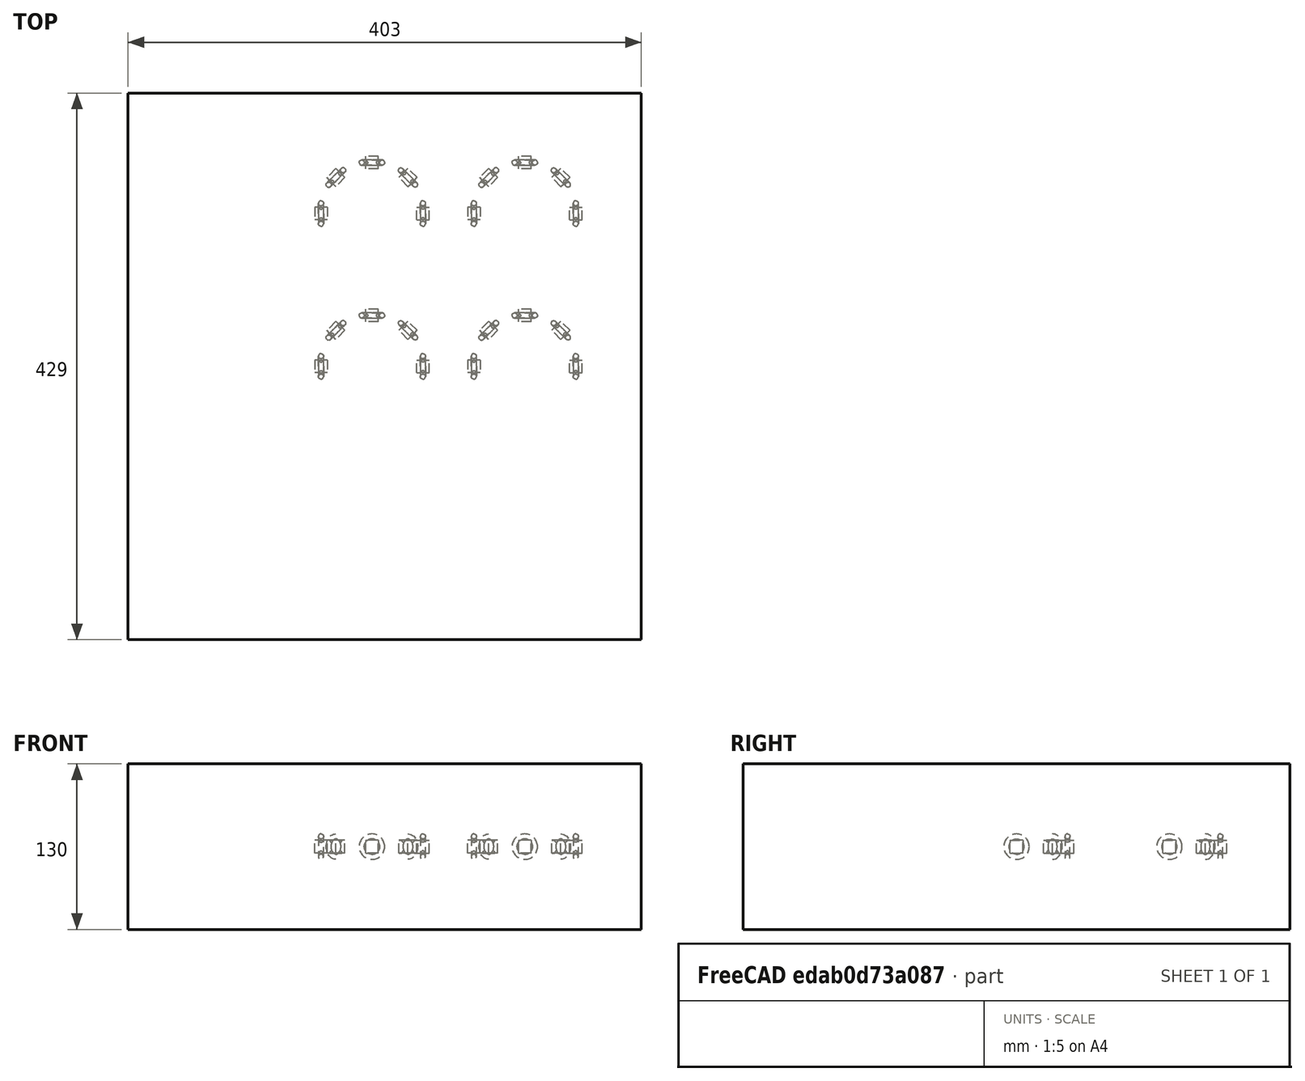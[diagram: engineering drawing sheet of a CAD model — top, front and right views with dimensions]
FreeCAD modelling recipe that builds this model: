
FCSTD DOCUMENT  (FreeCAD 1.0R39109 (Git))
Label: array-of-array-of-solid-offcenter
License: All rights reserved
objects: App::DocumentObjectGroupPython×1251, Part::FeaturePython×5, App::Part×2, Part::MultiFuse×1
note: 5 computed .brp shape members not serialized (recipe doc carries the construction recipe); baked Part::Feature solids carry a one-line shape summary decoded from their .brp

FEATURE [App::DocumentObjectGroupPython] HALFPI  # scripted group (container) (typed FeaturePython)
  name = HALFPI
  value = pi/2.
FEATURE [App::DocumentObjectGroupPython] PI  # scripted group (container) (typed FeaturePython)
  name = PI
  value = 1.*pi
FEATURE [App::DocumentObjectGroupPython] TWOPI  # scripted group (container) (typed FeaturePython)
  name = TWOPI
  value = 2.*pi
FEATURE [App::DocumentObjectGroupPython] Constants  # scripted group (container) (typed FeaturePython)
  Group = -> [HALFPI,PI,TWOPI]
FEATURE [App::DocumentObjectGroupPython] Variables  # scripted group (container) (typed FeaturePython)
FEATURE [App::DocumentObjectGroupPython] Quantities  # scripted group (container) (typed FeaturePython)
FEATURE [App::DocumentObjectGroupPython] Isotopes  # scripted group (container) (typed FeaturePython)
FEATURE [App::DocumentObjectGroupPython] Elements  # scripted group (container) (typed FeaturePython)
FEATURE [App::DocumentObjectGroupPython] Matrix  # scripted group (container) (typed FeaturePython)
FEATURE [App::DocumentObjectGroupPython] Surfaces  # scripted group (container) (typed FeaturePython)
FEATURE [App::DocumentObjectGroupPython] Opticals  # scripted group (container) (typed FeaturePython)
  Group = -> [Matrix,Surfaces]
FEATURE [App::DocumentObjectGroupPython] G4Isotopes  # scripted group (container) (typed FeaturePython)
FEATURE [App::DocumentObjectGroupPython] H_element  # scripted group (container) (typed FeaturePython)
  Z = 1
  atom_value = 1.008
  formula = H
  name = H_element
FEATURE [App::DocumentObjectGroupPython] He_element  # scripted group (container) (typed FeaturePython)
  Z = 2
  atom_value = 4.0026
  formula = He
  name = He_element
FEATURE [App::DocumentObjectGroupPython] Li_element  # scripted group (container) (typed FeaturePython)
  Z = 3
  atom_value = 6.94
  formula = Li
  name = Li_element
FEATURE [App::DocumentObjectGroupPython] Be_element  # scripted group (container) (typed FeaturePython)
  Z = 4
  atom_value = 9.01218
  formula = Be
  name = Be_element
FEATURE [App::DocumentObjectGroupPython] B_element  # scripted group (container) (typed FeaturePython)
  Z = 5
  atom_value = 10.81
  formula = B
  name = B_element
FEATURE [App::DocumentObjectGroupPython] C_element  # scripted group (container) (typed FeaturePython)
  Z = 6
  atom_value = 12.011
  formula = C
  name = C_element
FEATURE [App::DocumentObjectGroupPython] N_element  # scripted group (container) (typed FeaturePython)
  Z = 7
  atom_value = 14.007
  formula = N
  name = N_element
FEATURE [App::DocumentObjectGroupPython] O_element  # scripted group (container) (typed FeaturePython)
  Z = 8
  atom_value = 15.999
  formula = O
  name = O_element
FEATURE [App::DocumentObjectGroupPython] F_element  # scripted group (container) (typed FeaturePython)
  Z = 9
  atom_value = 18.9984
  formula = F
  name = F_element
FEATURE [App::DocumentObjectGroupPython] Ne_element  # scripted group (container) (typed FeaturePython)
  Z = 10
  atom_value = 20.1797
  formula = Ne
  name = Ne_element
FEATURE [App::DocumentObjectGroupPython] Na_element  # scripted group (container) (typed FeaturePython)
  Z = 11
  atom_value = 22.9898
  formula = Na
  name = Na_element
FEATURE [App::DocumentObjectGroupPython] Mg_element  # scripted group (container) (typed FeaturePython)
  Z = 12
  atom_value = 24.305
  formula = Mg
  name = Mg_element
FEATURE [App::DocumentObjectGroupPython] Al_element  # scripted group (container) (typed FeaturePython)
  Z = 13
  atom_value = 26.9815
  formula = Al
  name = Al_element
FEATURE [App::DocumentObjectGroupPython] Si_element  # scripted group (container) (typed FeaturePython)
  Z = 14
  atom_value = 28.085
  formula = Si
  name = Si_element
FEATURE [App::DocumentObjectGroupPython] P_element  # scripted group (container) (typed FeaturePython)
  Z = 15
  atom_value = 30.9738
  formula = P
  name = P_element
FEATURE [App::DocumentObjectGroupPython] S_element  # scripted group (container) (typed FeaturePython)
  Z = 16
  atom_value = 32.06
  formula = S
  name = S_element
FEATURE [App::DocumentObjectGroupPython] Cl_element  # scripted group (container) (typed FeaturePython)
  Z = 17
  atom_value = 35.45
  formula = Cl
  name = Cl_element
FEATURE [App::DocumentObjectGroupPython] Ar_element  # scripted group (container) (typed FeaturePython)
  Z = 18
  atom_value = 39.95
  formula = Ar
  name = Ar_element
FEATURE [App::DocumentObjectGroupPython] K_element  # scripted group (container) (typed FeaturePython)
  Z = 19
  atom_value = 39.0983
  formula = K
  name = K_element
FEATURE [App::DocumentObjectGroupPython] Ca_element  # scripted group (container) (typed FeaturePython)
  Z = 20
  atom_value = 40.078
  formula = Ca
  name = Ca_element
FEATURE [App::DocumentObjectGroupPython] Sc_element  # scripted group (container) (typed FeaturePython)
  Z = 21
  atom_value = 44.9559
  formula = Sc
  name = Sc_element
FEATURE [App::DocumentObjectGroupPython] Ti_element  # scripted group (container) (typed FeaturePython)
  Z = 22
  atom_value = 47.867
  formula = Ti
  name = Ti_element
FEATURE [App::DocumentObjectGroupPython] V_element  # scripted group (container) (typed FeaturePython)
  Z = 23
  atom_value = 50.9415
  formula = V
  name = V_element
FEATURE [App::DocumentObjectGroupPython] Cr_element  # scripted group (container) (typed FeaturePython)
  Z = 24
  atom_value = 51.9961
  formula = Cr
  name = Cr_element
FEATURE [App::DocumentObjectGroupPython] Mn_element  # scripted group (container) (typed FeaturePython)
  Z = 25
  atom_value = 54.938
  formula = Mn
  name = Mn_element
FEATURE [App::DocumentObjectGroupPython] Fe_element  # scripted group (container) (typed FeaturePython)
  Z = 26
  atom_value = 55.845
  formula = Fe
  name = Fe_element
FEATURE [App::DocumentObjectGroupPython] Co_element  # scripted group (container) (typed FeaturePython)
  Z = 27
  atom_value = 58.9332
  formula = Co
  name = Co_element
FEATURE [App::DocumentObjectGroupPython] Ni_element  # scripted group (container) (typed FeaturePython)
  Z = 28
  atom_value = 58.6934
  formula = Ni
  name = Ni_element
FEATURE [App::DocumentObjectGroupPython] Cu_element  # scripted group (container) (typed FeaturePython)
  Z = 29
  atom_value = 63.546
  formula = Cu
  name = Cu_element
FEATURE [App::DocumentObjectGroupPython] Zn_element  # scripted group (container) (typed FeaturePython)
  Z = 30
  atom_value = 65.38
  formula = Zn
  name = Zn_element
FEATURE [App::DocumentObjectGroupPython] Ga_element  # scripted group (container) (typed FeaturePython)
  Z = 31
  atom_value = 69.723
  formula = Ga
  name = Ga_element
FEATURE [App::DocumentObjectGroupPython] Ge_element  # scripted group (container) (typed FeaturePython)
  Z = 32
  atom_value = 72.63
  formula = Ge
  name = Ge_element
FEATURE [App::DocumentObjectGroupPython] As_element  # scripted group (container) (typed FeaturePython)
  Z = 33
  atom_value = 74.9216
  formula = As
  name = As_element
FEATURE [App::DocumentObjectGroupPython] Se_element  # scripted group (container) (typed FeaturePython)
  Z = 34
  atom_value = 78.971
  formula = Se
  name = Se_element
FEATURE [App::DocumentObjectGroupPython] Br_element  # scripted group (container) (typed FeaturePython)
  Z = 35
  atom_value = 79.904
  formula = Br
  name = Br_element
FEATURE [App::DocumentObjectGroupPython] Kr_element  # scripted group (container) (typed FeaturePython)
  Z = 36
  atom_value = 83.798
  formula = Kr
  name = Kr_element
FEATURE [App::DocumentObjectGroupPython] Rb_element  # scripted group (container) (typed FeaturePython)
  Z = 37
  atom_value = 85.4678
  formula = Rb
  name = Rb_element
FEATURE [App::DocumentObjectGroupPython] Sr_element  # scripted group (container) (typed FeaturePython)
  Z = 38
  atom_value = 87.62
  formula = Sr
  name = Sr_element
FEATURE [App::DocumentObjectGroupPython] Y_element  # scripted group (container) (typed FeaturePython)
  Z = 39
  atom_value = 88.9058
  formula = Y
  name = Y_element
FEATURE [App::DocumentObjectGroupPython] Zr_element  # scripted group (container) (typed FeaturePython)
  Z = 40
  atom_value = 91.224
  formula = Zr
  name = Zr_element
FEATURE [App::DocumentObjectGroupPython] Nb_element  # scripted group (container) (typed FeaturePython)
  Z = 41
  atom_value = 92.9064
  formula = Nb
  name = Nb_element
FEATURE [App::DocumentObjectGroupPython] Mo_element  # scripted group (container) (typed FeaturePython)
  Z = 42
  atom_value = 95.95
  formula = Mo
  name = Mo_element
FEATURE [App::DocumentObjectGroupPython] Tc_element  # scripted group (container) (typed FeaturePython)
  Z = 43
  atom_value = 97
  formula = Tc
  name = Tc_element
FEATURE [App::DocumentObjectGroupPython] Ru_element  # scripted group (container) (typed FeaturePython)
  Z = 44
  atom_value = 101.07
  formula = Ru
  name = Ru_element
FEATURE [App::DocumentObjectGroupPython] Rh_element  # scripted group (container) (typed FeaturePython)
  Z = 45
  atom_value = 102.905
  formula = Rh
  name = Rh_element
FEATURE [App::DocumentObjectGroupPython] Pd_element  # scripted group (container) (typed FeaturePython)
  Z = 46
  atom_value = 106.42
  formula = Pd
  name = Pd_element
FEATURE [App::DocumentObjectGroupPython] Ag_element  # scripted group (container) (typed FeaturePython)
  Z = 47
  atom_value = 107.868
  formula = Ag
  name = Ag_element
FEATURE [App::DocumentObjectGroupPython] Cd_element  # scripted group (container) (typed FeaturePython)
  Z = 48
  atom_value = 112.414
  formula = Cd
  name = Cd_element
FEATURE [App::DocumentObjectGroupPython] In_element  # scripted group (container) (typed FeaturePython)
  Z = 49
  atom_value = 114.818
  formula = In
  name = In_element
FEATURE [App::DocumentObjectGroupPython] Sn_element  # scripted group (container) (typed FeaturePython)
  Z = 50
  atom_value = 118.71
  formula = Sn
  name = Sn_element
FEATURE [App::DocumentObjectGroupPython] Sb_element  # scripted group (container) (typed FeaturePython)
  Z = 51
  atom_value = 121.76
  formula = Sb
  name = Sb_element
FEATURE [App::DocumentObjectGroupPython] Te_element  # scripted group (container) (typed FeaturePython)
  Z = 52
  atom_value = 127.6
  formula = Te
  name = Te_element
FEATURE [App::DocumentObjectGroupPython] I_element  # scripted group (container) (typed FeaturePython)
  Z = 53
  atom_value = 126.904
  formula = I
  name = I_element
FEATURE [App::DocumentObjectGroupPython] Xe_element  # scripted group (container) (typed FeaturePython)
  Z = 54
  atom_value = 131.293
  formula = Xe
  name = Xe_element
FEATURE [App::DocumentObjectGroupPython] Cs_element  # scripted group (container) (typed FeaturePython)
  Z = 55
  atom_value = 132.905
  formula = Cs
  name = Cs_element
FEATURE [App::DocumentObjectGroupPython] Ba_element  # scripted group (container) (typed FeaturePython)
  Z = 56
  atom_value = 137.327
  formula = Ba
  name = Ba_element
FEATURE [App::DocumentObjectGroupPython] La_element  # scripted group (container) (typed FeaturePython)
  Z = 57
  atom_value = 138.905
  formula = La
  name = La_element
FEATURE [App::DocumentObjectGroupPython] Ce_element  # scripted group (container) (typed FeaturePython)
  Z = 58
  atom_value = 140.116
  formula = Ce
  name = Ce_element
FEATURE [App::DocumentObjectGroupPython] Pr_element  # scripted group (container) (typed FeaturePython)
  Z = 59
  atom_value = 140.908
  formula = Pr
  name = Pr_element
FEATURE [App::DocumentObjectGroupPython] Nd_element  # scripted group (container) (typed FeaturePython)
  Z = 60
  atom_value = 144.242
  formula = Nd
  name = Nd_element
FEATURE [App::DocumentObjectGroupPython] Pm_element  # scripted group (container) (typed FeaturePython)
  Z = 61
  atom_value = 145
  formula = Pm
  name = Pm_element
FEATURE [App::DocumentObjectGroupPython] Sm_element  # scripted group (container) (typed FeaturePython)
  Z = 62
  atom_value = 150.36
  formula = Sm
  name = Sm_element
FEATURE [App::DocumentObjectGroupPython] Eu_element  # scripted group (container) (typed FeaturePython)
  Z = 63
  atom_value = 151.964
  formula = Eu
  name = Eu_element
FEATURE [App::DocumentObjectGroupPython] Gd_element  # scripted group (container) (typed FeaturePython)
  Z = 64
  atom_value = 157.25
  formula = Gd
  name = Gd_element
FEATURE [App::DocumentObjectGroupPython] Tb_element  # scripted group (container) (typed FeaturePython)
  Z = 65
  atom_value = 158.925
  formula = Tb
  name = Tb_element
FEATURE [App::DocumentObjectGroupPython] Dy_element  # scripted group (container) (typed FeaturePython)
  Z = 66
  atom_value = 162.5
  formula = Dy
  name = Dy_element
FEATURE [App::DocumentObjectGroupPython] Ho_element  # scripted group (container) (typed FeaturePython)
  Z = 67
  atom_value = 164.93
  formula = Ho
  name = Ho_element
FEATURE [App::DocumentObjectGroupPython] Er_element  # scripted group (container) (typed FeaturePython)
  Z = 68
  atom_value = 167.259
  formula = Er
  name = Er_element
FEATURE [App::DocumentObjectGroupPython] Tm_element  # scripted group (container) (typed FeaturePython)
  Z = 69
  atom_value = 168.934
  formula = Tm
  name = Tm_element
FEATURE [App::DocumentObjectGroupPython] Yb_element  # scripted group (container) (typed FeaturePython)
  Z = 70
  atom_value = 173.045
  formula = Yb
  name = Yb_element
FEATURE [App::DocumentObjectGroupPython] Lu_element  # scripted group (container) (typed FeaturePython)
  Z = 71
  atom_value = 174.967
  formula = Lu
  name = Lu_element
FEATURE [App::DocumentObjectGroupPython] Hf_element  # scripted group (container) (typed FeaturePython)
  Z = 72
  atom_value = 178.49
  formula = Hf
  name = Hf_element
FEATURE [App::DocumentObjectGroupPython] Ta_element  # scripted group (container) (typed FeaturePython)
  Z = 73
  atom_value = 180.948
  formula = Ta
  name = Ta_element
FEATURE [App::DocumentObjectGroupPython] W_element  # scripted group (container) (typed FeaturePython)
  Z = 74
  atom_value = 183.84
  formula = W
  name = W_element
FEATURE [App::DocumentObjectGroupPython] Re_element  # scripted group (container) (typed FeaturePython)
  Z = 75
  atom_value = 186.207
  formula = Re
  name = Re_element
FEATURE [App::DocumentObjectGroupPython] Os_element  # scripted group (container) (typed FeaturePython)
  Z = 76
  atom_value = 190.23
  formula = Os
  name = Os_element
FEATURE [App::DocumentObjectGroupPython] Ir_element  # scripted group (container) (typed FeaturePython)
  Z = 77
  atom_value = 192.217
  formula = Ir
  name = Ir_element
FEATURE [App::DocumentObjectGroupPython] Pt_element  # scripted group (container) (typed FeaturePython)
  Z = 78
  atom_value = 195.084
  formula = Pt
  name = Pt_element
FEATURE [App::DocumentObjectGroupPython] Au_element  # scripted group (container) (typed FeaturePython)
  Z = 79
  atom_value = 196.967
  formula = Au
  name = Au_element
FEATURE [App::DocumentObjectGroupPython] Hg_element  # scripted group (container) (typed FeaturePython)
  Z = 80
  atom_value = 200.592
  formula = Hg
  name = Hg_element
FEATURE [App::DocumentObjectGroupPython] Tl_element  # scripted group (container) (typed FeaturePython)
  Z = 81
  atom_value = 204.38
  formula = Tl
  name = Tl_element
FEATURE [App::DocumentObjectGroupPython] Pb_element  # scripted group (container) (typed FeaturePython)
  Z = 82
  atom_value = 207.2
  formula = Pb
  name = Pb_element
FEATURE [App::DocumentObjectGroupPython] Bi_element  # scripted group (container) (typed FeaturePython)
  Z = 83
  atom_value = 208.98
  formula = Bi
  name = Bi_element
FEATURE [App::DocumentObjectGroupPython] Po_element  # scripted group (container) (typed FeaturePython)
  Z = 84
  atom_value = 209
  formula = Po
  name = Po_element
FEATURE [App::DocumentObjectGroupPython] At_element  # scripted group (container) (typed FeaturePython)
  Z = 85
  atom_value = 210
  formula = At
  name = At_element
FEATURE [App::DocumentObjectGroupPython] Rn_element  # scripted group (container) (typed FeaturePython)
  Z = 86
  atom_value = 222
  formula = Rn
  name = Rn_element
FEATURE [App::DocumentObjectGroupPython] Fr_element  # scripted group (container) (typed FeaturePython)
  Z = 87
  atom_value = 223
  formula = Fr
  name = Fr_element
FEATURE [App::DocumentObjectGroupPython] Ra_element  # scripted group (container) (typed FeaturePython)
  Z = 88
  atom_value = 226
  formula = Ra
  name = Ra_element
FEATURE [App::DocumentObjectGroupPython] Ac_element  # scripted group (container) (typed FeaturePython)
  Z = 89
  atom_value = 227
  formula = Ac
  name = Ac_element
FEATURE [App::DocumentObjectGroupPython] Th_element  # scripted group (container) (typed FeaturePython)
  Z = 90
  atom_value = 232.038
  formula = Th
  name = Th_element
FEATURE [App::DocumentObjectGroupPython] Pa_element  # scripted group (container) (typed FeaturePython)
  Z = 91
  atom_value = 231.036
  formula = Pa
  name = Pa_element
FEATURE [App::DocumentObjectGroupPython] U_element  # scripted group (container) (typed FeaturePython)
  Z = 92
  atom_value = 238.029
  formula = U
  name = U_element
FEATURE [App::DocumentObjectGroupPython] Np_element  # scripted group (container) (typed FeaturePython)
  Z = 93
  atom_value = 237
  formula = Np
  name = Np_element
FEATURE [App::DocumentObjectGroupPython] Pu_element  # scripted group (container) (typed FeaturePython)
  Z = 94
  atom_value = 244
  formula = Pu
  name = Pu_element
FEATURE [App::DocumentObjectGroupPython] Am_element  # scripted group (container) (typed FeaturePython)
  Z = 95
  atom_value = 243
  formula = Am
  name = Am_element
FEATURE [App::DocumentObjectGroupPython] Cm_element  # scripted group (container) (typed FeaturePython)
  Z = 96
  atom_value = 247
  formula = Cm
  name = Cm_element
FEATURE [App::DocumentObjectGroupPython] Bk_element  # scripted group (container) (typed FeaturePython)
  Z = 97
  atom_value = 247
  formula = Bk
  name = Bk_element
FEATURE [App::DocumentObjectGroupPython] Cf_element  # scripted group (container) (typed FeaturePython)
  Z = 98
  atom_value = 251
  formula = Cf
  name = Cf_element
FEATURE [App::DocumentObjectGroupPython] G4Elements  # scripted group (container) (typed FeaturePython)
  Group = -> [H_element,He_element,Li_element,Be_element,B_element,C_element,N_element,O_element,F_element,Ne_element,Na_element,Mg_element,Al_element,Si_element,P_element,S_element,Cl_element,Ar_element,K_element,Ca_element,Sc_element,Ti_element,V_element,Cr_element,Mn_element,Fe_element,Co_element,Ni_element,Cu_element,Zn_element,Ga_element,Ge_element,As_element,Se_element,Br_element,Kr_element,Rb_element,+61 more]
FEATURE [App::DocumentObjectGroupPython] H_element001  label="H_element : 0.101"  # scripted group (container) (typed FeaturePython)
  n = 0.101327
FEATURE [App::DocumentObjectGroupPython] C_element001  label="C_element : 0.775"  # scripted group (container) (typed FeaturePython)
  n = 0.7755
FEATURE [App::DocumentObjectGroupPython] N_element001  label="N_element : 0.035"  # scripted group (container) (typed FeaturePython)
  n = 0.035057
FEATURE [App::DocumentObjectGroupPython] O_element001  label="O_element : 0.052"  # scripted group (container) (typed FeaturePython)
  n = 0.0523159
FEATURE [App::DocumentObjectGroupPython] F_element001  label="F_element : 0.017"  # scripted group (container) (typed FeaturePython)
  n = 0.017422
FEATURE [App::DocumentObjectGroupPython] Ca_element001  label="Ca_element : 0.018"  # scripted group (container) (typed FeaturePython)
  n = 0.018378
FEATURE [App::DocumentObjectGroupPython] G4_A_150_TISSUE  label="G4_A-150_TISSUE"  # scripted group (container) (typed FeaturePython)
  Dunit = g/cm3
  Dvalue = 1.127
  Group = -> [H_element001,C_element001,N_element001,O_element001,F_element001,Ca_element001]
  conduct = 2
  density = 1
  expand = 3
  formula = G4_A-150_TISSUE
  name = G4_A-150_TISSUE
  specific = 4
FEATURE [App::DocumentObjectGroupPython] C_element002  label="C_element : 3"  # scripted group (container) (typed FeaturePython)
  n = 3
  ref = C_element
FEATURE [App::DocumentObjectGroupPython] H_element002  label="H_element : 6"  # scripted group (container) (typed FeaturePython)
  n = 6
  ref = H_element
FEATURE [App::DocumentObjectGroupPython] O_element002  label="O_element : 1"  # scripted group (container) (typed FeaturePython)
  n = 1
  ref = O_element
FEATURE [App::DocumentObjectGroupPython] G4_ACETONE  # scripted group (container) (typed FeaturePython)
  Dunit = g/cm3
  Dvalue = 0.7899
  Group = -> [C_element002,H_element002,O_element002]
  conduct = 2
  density = 1
  expand = 3
  formula = G4_ACETONE
  name = G4_ACETONE
  specific = 4
FEATURE [App::DocumentObjectGroupPython] C_element003  label="C_element : 2"  # scripted group (container) (typed FeaturePython)
  n = 2
  ref = C_element
FEATURE [App::DocumentObjectGroupPython] H_element003  label="H_element : 2"  # scripted group (container) (typed FeaturePython)
  n = 2
  ref = H_element
FEATURE [App::DocumentObjectGroupPython] G4_ACETYLENE  # scripted group (container) (typed FeaturePython)
  Dunit = g/cm3
  Dvalue = 0.0010967
  Group = -> [C_element003,H_element003]
  conduct = 2
  density = 1
  expand = 3
  formula = G4_ACETYLENE
  name = G4_ACETYLENE
  specific = 4
FEATURE [App::DocumentObjectGroupPython] C_element004  label="C_element : 5"  # scripted group (container) (typed FeaturePython)
  n = 5
  ref = C_element
FEATURE [App::DocumentObjectGroupPython] H_element004  label="H_element : 5"  # scripted group (container) (typed FeaturePython)
  n = 5
  ref = H_element
FEATURE [App::DocumentObjectGroupPython] N_element002  label="N_element : 5"  # scripted group (container) (typed FeaturePython)
  n = 5
  ref = N_element
FEATURE [App::DocumentObjectGroupPython] G4_ADENINE  # scripted group (container) (typed FeaturePython)
  Dunit = g/cm3
  Dvalue = 1.6
  Group = -> [C_element004,H_element004,N_element002]
  conduct = 2
  density = 1
  expand = 3
  formula = G4_ADENINE
  name = G4_ADENINE
  specific = 4
FEATURE [App::DocumentObjectGroupPython] H_element005  label="H_element : 0.114"  # scripted group (container) (typed FeaturePython)
  n = 0.114
FEATURE [App::DocumentObjectGroupPython] C_element005  label="C_element : 0.598"  # scripted group (container) (typed FeaturePython)
  n = 0.598
FEATURE [App::DocumentObjectGroupPython] N_element003  label="N_element : 0.007"  # scripted group (container) (typed FeaturePython)
  n = 0.007
FEATURE [App::DocumentObjectGroupPython] O_element003  label="O_element : 0.278"  # scripted group (container) (typed FeaturePython)
  n = 0.278
FEATURE [App::DocumentObjectGroupPython] Na_element001  label="Na_element : 0.001"  # scripted group (container) (typed FeaturePython)
  n = 0.001
FEATURE [App::DocumentObjectGroupPython] S_element001  label="S_element : 0.001"  # scripted group (container) (typed FeaturePython)
  n = 0.001
FEATURE [App::DocumentObjectGroupPython] Cl_element001  label="Cl_element : 0.001"  # scripted group (container) (typed FeaturePython)
  n = 0.001
FEATURE [App::DocumentObjectGroupPython] G4_ADIPOSE_TISSUE_ICRP  # scripted group (container) (typed FeaturePython)
  Dunit = g/cm3
  Dvalue = 0.95
  Group = -> [H_element005,C_element005,N_element003,O_element003,Na_element001,S_element001,Cl_element001]
  conduct = 2
  density = 1
  expand = 3
  formula = G4_ADIPOSE_TISSUE_ICRP
  name = G4_ADIPOSE_TISSUE_ICRP
  specific = 4
FEATURE [App::DocumentObjectGroupPython] C_element006  label="C_element : 0.000"  # scripted group (container) (typed FeaturePython)
  n = 0.000124
FEATURE [App::DocumentObjectGroupPython] N_element004  label="N_element : 0.755"  # scripted group (container) (typed FeaturePython)
  n = 0.755268
FEATURE [App::DocumentObjectGroupPython] O_element004  label="O_element : 0.232"  # scripted group (container) (typed FeaturePython)
  n = 0.231781
FEATURE [App::DocumentObjectGroupPython] Ar_element001  label="Ar_element : 0.013"  # scripted group (container) (typed FeaturePython)
  n = 0.012827
FEATURE [App::DocumentObjectGroupPython] G4_AIR  # scripted group (container) (typed FeaturePython)
  Dunit = g/cm3
  Dvalue = 0.00120479
  Group = -> [C_element006,N_element004,O_element004,Ar_element001]
  conduct = 2
  density = 1
  expand = 3
  formula = G4_AIR
  name = G4_AIR
  specific = 4
FEATURE [App::DocumentObjectGroupPython] C_element007  label="C_element : 006"  # scripted group (container) (typed FeaturePython)
  n = 3
  ref = C_element
FEATURE [App::DocumentObjectGroupPython] H_element006  label="H_element : 7"  # scripted group (container) (typed FeaturePython)
  n = 7
  ref = H_element
FEATURE [App::DocumentObjectGroupPython] N_element005  label="N_element : 1"  # scripted group (container) (typed FeaturePython)
  n = 1
  ref = N_element
FEATURE [App::DocumentObjectGroupPython] O_element005  label="O_element : 2"  # scripted group (container) (typed FeaturePython)
  n = 2
  ref = O_element
FEATURE [App::DocumentObjectGroupPython] G4_ALANINE  # scripted group (container) (typed FeaturePython)
  Dunit = g/cm3
  Dvalue = 1.42
  Group = -> [C_element007,H_element006,N_element005,O_element005]
  conduct = 2
  density = 1
  expand = 3
  formula = G4_ALANINE
  name = G4_ALANINE
  specific = 4
FEATURE [App::DocumentObjectGroupPython] Al_element001  label="Al_element : 2"  # scripted group (container) (typed FeaturePython)
  n = 2
  ref = Al_element
FEATURE [App::DocumentObjectGroupPython] O_element006  label="O_element : 3"  # scripted group (container) (typed FeaturePython)
  n = 3
  ref = O_element
FEATURE [App::DocumentObjectGroupPython] G4_ALUMINUM_OXIDE  # scripted group (container) (typed FeaturePython)
  Dunit = g/cm3
  Dvalue = 3.97
  Group = -> [Al_element001,O_element006]
  conduct = 2
  density = 1
  expand = 3
  formula = G4_ALUMINUM_OXIDE
  name = G4_ALUMINUM_OXIDE
  specific = 4
FEATURE [App::DocumentObjectGroupPython] H_element007  label="H_element : 0.106"  # scripted group (container) (typed FeaturePython)
  n = 0.10593
FEATURE [App::DocumentObjectGroupPython] C_element008  label="C_element : 0.789"  # scripted group (container) (typed FeaturePython)
  n = 0.788974
FEATURE [App::DocumentObjectGroupPython] O_element007  label="O_element : 0.105"  # scripted group (container) (typed FeaturePython)
  n = 0.105096
FEATURE [App::DocumentObjectGroupPython] G4_AMBER  # scripted group (container) (typed FeaturePython)
  Dunit = g/cm3
  Dvalue = 1.1
  Group = -> [H_element007,C_element008,O_element007]
  conduct = 2
  density = 1
  expand = 3
  formula = G4_AMBER
  name = G4_AMBER
  specific = 4
FEATURE [App::DocumentObjectGroupPython] N_element006  label="N_element : 006"  # scripted group (container) (typed FeaturePython)
  n = 1
  ref = N_element
FEATURE [App::DocumentObjectGroupPython] H_element008  label="H_element : 3"  # scripted group (container) (typed FeaturePython)
  n = 3
  ref = H_element
FEATURE [App::DocumentObjectGroupPython] G4_AMMONIA  # scripted group (container) (typed FeaturePython)
  Dunit = g/cm3
  Dvalue = 0.000826019
  Group = -> [N_element006,H_element008]
  conduct = 2
  density = 1
  expand = 3
  formula = G4_AMMONIA
  name = G4_AMMONIA
  specific = 4
FEATURE [App::DocumentObjectGroupPython] C_element009  label="C_element : 6"  # scripted group (container) (typed FeaturePython)
  n = 6
  ref = C_element
FEATURE [App::DocumentObjectGroupPython] H_element009  label="H_element : 008"  # scripted group (container) (typed FeaturePython)
  n = 7
  ref = H_element
FEATURE [App::DocumentObjectGroupPython] N_element007  label="N_element : 007"  # scripted group (container) (typed FeaturePython)
  n = 1
  ref = N_element
FEATURE [App::DocumentObjectGroupPython] G4_ANILINE  # scripted group (container) (typed FeaturePython)
  Dunit = g/cm3
  Dvalue = 1.0235
  Group = -> [C_element009,H_element009,N_element007]
  conduct = 2
  density = 1
  expand = 3
  formula = G4_ANILINE
  name = G4_ANILINE
  specific = 4
FEATURE [App::DocumentObjectGroupPython] C_element010  label="C_element : 14"  # scripted group (container) (typed FeaturePython)
  n = 14
  ref = C_element
FEATURE [App::DocumentObjectGroupPython] H_element010  label="H_element : 10"  # scripted group (container) (typed FeaturePython)
  n = 10
  ref = H_element
FEATURE [App::DocumentObjectGroupPython] G4_ANTHRACENE  # scripted group (container) (typed FeaturePython)
  Dunit = g/cm3
  Dvalue = 1.283
  Group = -> [C_element010,H_element010]
  conduct = 2
  density = 1
  expand = 3
  formula = G4_ANTHRACENE
  name = G4_ANTHRACENE
  specific = 4
FEATURE [App::DocumentObjectGroupPython] H_element011  label="H_element : 0.065"  # scripted group (container) (typed FeaturePython)
  n = 0.0654709
FEATURE [App::DocumentObjectGroupPython] C_element011  label="C_element : 0.537"  # scripted group (container) (typed FeaturePython)
  n = 0.536944
FEATURE [App::DocumentObjectGroupPython] N_element008  label="N_element : 0.021"  # scripted group (container) (typed FeaturePython)
  n = 0.0215
FEATURE [App::DocumentObjectGroupPython] O_element008  label="O_element : 0.032"  # scripted group (container) (typed FeaturePython)
  n = 0.032085
FEATURE [App::DocumentObjectGroupPython] F_element002  label="F_element : 0.167"  # scripted group (container) (typed FeaturePython)
  n = 0.167411
FEATURE [App::DocumentObjectGroupPython] Ca_element002  label="Ca_element : 0.177"  # scripted group (container) (typed FeaturePython)
  n = 0.176589
FEATURE [App::DocumentObjectGroupPython] G4_B_100_BONE  label="G4_B-100_BONE"  # scripted group (container) (typed FeaturePython)
  Dunit = g/cm3
  Dvalue = 1.45
  Group = -> [H_element011,C_element011,N_element008,O_element008,F_element002,Ca_element002]
  conduct = 2
  density = 1
  expand = 3
  formula = G4_B-100_BONE
  name = G4_B-100_BONE
  specific = 4
FEATURE [App::DocumentObjectGroupPython] H_element012  label="H_element : 0.057"  # scripted group (container) (typed FeaturePython)
  n = 0.057441
FEATURE [App::DocumentObjectGroupPython] C_element012  label="C_element : 0.790"  # scripted group (container) (typed FeaturePython)
  n = 0.774591
FEATURE [App::DocumentObjectGroupPython] O_element009  label="O_element : 0.168"  # scripted group (container) (typed FeaturePython)
  n = 0.167968
FEATURE [App::DocumentObjectGroupPython] G4_BAKELITE  # scripted group (container) (typed FeaturePython)
  Dunit = g/cm3
  Dvalue = 1.25
  Group = -> [H_element012,C_element012,O_element009]
  conduct = 2
  density = 1
  expand = 3
  formula = G4_BAKELITE
  name = G4_BAKELITE
  specific = 4
FEATURE [App::DocumentObjectGroupPython] Ba_element001  label="Ba_element : 1"  # scripted group (container) (typed FeaturePython)
  n = 1
  ref = Ba_element
FEATURE [App::DocumentObjectGroupPython] F_element003  label="F_element : 2"  # scripted group (container) (typed FeaturePython)
  n = 2
  ref = F_element
FEATURE [App::DocumentObjectGroupPython] G4_BARIUM_FLUORIDE  # scripted group (container) (typed FeaturePython)
  Dunit = g/cm3
  Dvalue = 4.89
  Group = -> [Ba_element001,F_element003]
  conduct = 2
  density = 1
  expand = 3
  formula = G4_BARIUM_FLUORIDE
  name = G4_BARIUM_FLUORIDE
  specific = 4
FEATURE [App::DocumentObjectGroupPython] Ba_element002  label="Ba_element : 002"  # scripted group (container) (typed FeaturePython)
  n = 1
  ref = Ba_element
FEATURE [App::DocumentObjectGroupPython] S_element002  label="S_element : 1"  # scripted group (container) (typed FeaturePython)
  n = 1
  ref = S_element
FEATURE [App::DocumentObjectGroupPython] O_element010  label="O_element : 4"  # scripted group (container) (typed FeaturePython)
  n = 4
  ref = O_element
FEATURE [App::DocumentObjectGroupPython] G4_BARIUM_SULFATE  # scripted group (container) (typed FeaturePython)
  Dunit = g/cm3
  Dvalue = 4.5
  Group = -> [Ba_element002,S_element002,O_element010]
  conduct = 2
  density = 1
  expand = 3
  formula = G4_BARIUM_SULFATE
  name = G4_BARIUM_SULFATE
  specific = 4
FEATURE [App::DocumentObjectGroupPython] C_element013  label="C_element : 007"  # scripted group (container) (typed FeaturePython)
  n = 6
  ref = C_element
FEATURE [App::DocumentObjectGroupPython] H_element013  label="H_element : 009"  # scripted group (container) (typed FeaturePython)
  n = 6
  ref = H_element
FEATURE [App::DocumentObjectGroupPython] G4_BENZENE  # scripted group (container) (typed FeaturePython)
  Dunit = g/cm3
  Dvalue = 0.87865
  Group = -> [C_element013,H_element013]
  conduct = 2
  density = 1
  expand = 3
  formula = G4_BENZENE
  name = G4_BENZENE
  specific = 4
FEATURE [App::DocumentObjectGroupPython] Be_element001  label="Be_element : 1"  # scripted group (container) (typed FeaturePython)
  n = 1
  ref = Be_element
FEATURE [App::DocumentObjectGroupPython] O_element011  label="O_element : 005"  # scripted group (container) (typed FeaturePython)
  n = 1
  ref = O_element
FEATURE [App::DocumentObjectGroupPython] G4_BERYLLIUM_OXIDE  # scripted group (container) (typed FeaturePython)
  Dunit = g/cm3
  Dvalue = 3.01
  Group = -> [Be_element001,O_element011]
  conduct = 2
  density = 1
  expand = 3
  formula = G4_BERYLLIUM_OXIDE
  name = G4_BERYLLIUM_OXIDE
  specific = 4
FEATURE [App::DocumentObjectGroupPython] Bi_element001  label="Bi_element : 4"  # scripted group (container) (typed FeaturePython)
  n = 4
  ref = Bi_element
FEATURE [App::DocumentObjectGroupPython] Ge_element001  label="Ge_element : 3"  # scripted group (container) (typed FeaturePython)
  n = 3
  ref = Ge_element
FEATURE [App::DocumentObjectGroupPython] O_element012  label="O_element : 12"  # scripted group (container) (typed FeaturePython)
  n = 12
  ref = O_element
FEATURE [App::DocumentObjectGroupPython] G4_BGO  # scripted group (container) (typed FeaturePython)
  Dunit = g/cm3
  Dvalue = 7.13
  Group = -> [Bi_element001,Ge_element001,O_element012]
  conduct = 2
  density = 1
  expand = 3
  formula = G4_BGO
  name = G4_BGO
  specific = 4
FEATURE [App::DocumentObjectGroupPython] H_element014  label="H_element : 0.102"  # scripted group (container) (typed FeaturePython)
  n = 0.102
FEATURE [App::DocumentObjectGroupPython] C_element014  label="C_element : 0.110"  # scripted group (container) (typed FeaturePython)
  n = 0.11
FEATURE [App::DocumentObjectGroupPython] N_element009  label="N_element : 0.033"  # scripted group (container) (typed FeaturePython)
  n = 0.033
FEATURE [App::DocumentObjectGroupPython] O_element013  label="O_element : 0.745"  # scripted group (container) (typed FeaturePython)
  n = 0.745
FEATURE [App::DocumentObjectGroupPython] Na_element002  label="Na_element : 0.002"  # scripted group (container) (typed FeaturePython)
  n = 0.001
FEATURE [App::DocumentObjectGroupPython] P_element001  label="P_element : 0.001"  # scripted group (container) (typed FeaturePython)
  n = 0.001
FEATURE [App::DocumentObjectGroupPython] S_element003  label="S_element : 0.002"  # scripted group (container) (typed FeaturePython)
  n = 0.002
FEATURE [App::DocumentObjectGroupPython] Cl_element002  label="Cl_element : 0.003"  # scripted group (container) (typed FeaturePython)
  n = 0.003
FEATURE [App::DocumentObjectGroupPython] K_element001  label="K_element : 0.002"  # scripted group (container) (typed FeaturePython)
  n = 0.002
FEATURE [App::DocumentObjectGroupPython] Fe_element001  label="Fe_element : 0.001"  # scripted group (container) (typed FeaturePython)
  n = 0.001
FEATURE [App::DocumentObjectGroupPython] G4_BLOOD_ICRP  # scripted group (container) (typed FeaturePython)
  Dunit = g/cm3
  Dvalue = 1.06
  Group = -> [H_element014,C_element014,N_element009,O_element013,Na_element002,P_element001,S_element003,Cl_element002,K_element001,Fe_element001]
  conduct = 2
  density = 1
  expand = 3
  formula = G4_BLOOD_ICRP
  name = G4_BLOOD_ICRP
  specific = 4
FEATURE [App::DocumentObjectGroupPython] H_element015  label="H_element : 0.064"  # scripted group (container) (typed FeaturePython)
  n = 0.064
FEATURE [App::DocumentObjectGroupPython] C_element015  label="C_element : 0.278"  # scripted group (container) (typed FeaturePython)
  n = 0.278
FEATURE [App::DocumentObjectGroupPython] N_element010  label="N_element : 0.027"  # scripted group (container) (typed FeaturePython)
  n = 0.027
FEATURE [App::DocumentObjectGroupPython] O_element014  label="O_element : 0.410"  # scripted group (container) (typed FeaturePython)
  n = 0.41
FEATURE [App::DocumentObjectGroupPython] Mg_element001  label="Mg_element : 0.002"  # scripted group (container) (typed FeaturePython)
  n = 0.002
FEATURE [App::DocumentObjectGroupPython] P_element002  label="P_element : 0.070"  # scripted group (container) (typed FeaturePython)
  n = 0.07
FEATURE [App::DocumentObjectGroupPython] S_element004  label="S_element : 0.003"  # scripted group (container) (typed FeaturePython)
  n = 0.002
FEATURE [App::DocumentObjectGroupPython] Ca_element003  label="Ca_element : 0.147"  # scripted group (container) (typed FeaturePython)
  n = 0.147
FEATURE [App::DocumentObjectGroupPython] G4_BONE_COMPACT_ICRU  # scripted group (container) (typed FeaturePython)
  Dunit = g/cm3
  Dvalue = 1.85
  Group = -> [H_element015,C_element015,N_element010,O_element014,Mg_element001,P_element002,S_element004,Ca_element003]
  conduct = 2
  density = 1
  expand = 3
  formula = G4_BONE_COMPACT_ICRU
  name = G4_BONE_COMPACT_ICRU
  specific = 4
FEATURE [App::DocumentObjectGroupPython] H_element016  label="H_element : 0.034"  # scripted group (container) (typed FeaturePython)
  n = 0.034
FEATURE [App::DocumentObjectGroupPython] C_element016  label="C_element : 0.155"  # scripted group (container) (typed FeaturePython)
  n = 0.155
FEATURE [App::DocumentObjectGroupPython] N_element011  label="N_element : 0.042"  # scripted group (container) (typed FeaturePython)
  n = 0.042
FEATURE [App::DocumentObjectGroupPython] O_element015  label="O_element : 0.435"  # scripted group (container) (typed FeaturePython)
  n = 0.435
FEATURE [App::DocumentObjectGroupPython] Na_element003  label="Na_element : 0.003"  # scripted group (container) (typed FeaturePython)
  n = 0.001
FEATURE [App::DocumentObjectGroupPython] Mg_element002  label="Mg_element : 0.003"  # scripted group (container) (typed FeaturePython)
  n = 0.002
FEATURE [App::DocumentObjectGroupPython] P_element003  label="P_element : 0.103"  # scripted group (container) (typed FeaturePython)
  n = 0.103
FEATURE [App::DocumentObjectGroupPython] S_element005  label="S_element : 0.004"  # scripted group (container) (typed FeaturePython)
  n = 0.003
FEATURE [App::DocumentObjectGroupPython] Ca_element004  label="Ca_element : 0.225"  # scripted group (container) (typed FeaturePython)
  n = 0.225
FEATURE [App::DocumentObjectGroupPython] G4_BONE_CORTICAL_ICRP  # scripted group (container) (typed FeaturePython)
  Dunit = g/cm3
  Dvalue = 1.92
  Group = -> [H_element016,C_element016,N_element011,O_element015,Na_element003,Mg_element002,P_element003,S_element005,Ca_element004]
  conduct = 2
  density = 1
  expand = 3
  formula = G4_BONE_CORTICAL_ICRP
  name = G4_BONE_CORTICAL_ICRP
  specific = 4
FEATURE [App::DocumentObjectGroupPython] B_element001  label="B_element : 4"  # scripted group (container) (typed FeaturePython)
  n = 4
  ref = B_element
FEATURE [App::DocumentObjectGroupPython] C_element017  label="C_element : 1"  # scripted group (container) (typed FeaturePython)
  n = 1
  ref = C_element
FEATURE [App::DocumentObjectGroupPython] G4_BORON_CARBIDE  # scripted group (container) (typed FeaturePython)
  Dunit = g/cm3
  Dvalue = 2.52
  Group = -> [B_element001,C_element017]
  conduct = 2
  density = 1
  expand = 3
  formula = G4_BORON_CARBIDE
  name = G4_BORON_CARBIDE
  specific = 4
FEATURE [App::DocumentObjectGroupPython] B_element002  label="B_element : 2"  # scripted group (container) (typed FeaturePython)
  n = 2
  ref = B_element
FEATURE [App::DocumentObjectGroupPython] O_element016  label="O_element : 006"  # scripted group (container) (typed FeaturePython)
  n = 3
  ref = O_element
FEATURE [App::DocumentObjectGroupPython] G4_BORON_OXIDE  # scripted group (container) (typed FeaturePython)
  Dunit = g/cm3
  Dvalue = 1.812
  Group = -> [B_element002,O_element016]
  conduct = 2
  density = 1
  expand = 3
  formula = G4_BORON_OXIDE
  name = G4_BORON_OXIDE
  specific = 4
FEATURE [App::DocumentObjectGroupPython] H_element017  label="H_element : 0.107"  # scripted group (container) (typed FeaturePython)
  n = 0.107
FEATURE [App::DocumentObjectGroupPython] C_element018  label="C_element : 0.145"  # scripted group (container) (typed FeaturePython)
  n = 0.145
FEATURE [App::DocumentObjectGroupPython] N_element012  label="N_element : 0.022"  # scripted group (container) (typed FeaturePython)
  n = 0.022
FEATURE [App::DocumentObjectGroupPython] O_element017  label="O_element : 0.712"  # scripted group (container) (typed FeaturePython)
  n = 0.712
FEATURE [App::DocumentObjectGroupPython] Na_element004  label="Na_element : 0.004"  # scripted group (container) (typed FeaturePython)
  n = 0.002
FEATURE [App::DocumentObjectGroupPython] P_element004  label="P_element : 0.004"  # scripted group (container) (typed FeaturePython)
  n = 0.004
FEATURE [App::DocumentObjectGroupPython] S_element006  label="S_element : 0.005"  # scripted group (container) (typed FeaturePython)
  n = 0.002
FEATURE [App::DocumentObjectGroupPython] Cl_element003  label="Cl_element : 0.004"  # scripted group (container) (typed FeaturePython)
  n = 0.003
FEATURE [App::DocumentObjectGroupPython] K_element002  label="K_element : 0.003"  # scripted group (container) (typed FeaturePython)
  n = 0.003
FEATURE [App::DocumentObjectGroupPython] G4_BRAIN_ICRP  # scripted group (container) (typed FeaturePython)
  Dunit = g/cm3
  Dvalue = 1.04
  Group = -> [H_element017,C_element018,N_element012,O_element017,Na_element004,P_element004,S_element006,Cl_element003,K_element002]
  conduct = 2
  density = 1
  expand = 3
  formula = G4_BRAIN_ICRP
  name = G4_BRAIN_ICRP
  specific = 4
FEATURE [App::DocumentObjectGroupPython] C_element019  label="C_element : 4"  # scripted group (container) (typed FeaturePython)
  n = 4
  ref = C_element
FEATURE [App::DocumentObjectGroupPython] H_element018  label="H_element : 010"  # scripted group (container) (typed FeaturePython)
  n = 10
  ref = H_element
FEATURE [App::DocumentObjectGroupPython] G4_BUTANE  # scripted group (container) (typed FeaturePython)
  Dunit = g/cm3
  Dvalue = 0.00249343
  Group = -> [C_element019,H_element018]
  conduct = 2
  density = 1
  expand = 3
  formula = G4_BUTANE
  name = G4_BUTANE
  specific = 4
FEATURE [App::DocumentObjectGroupPython] C_element020  label="C_element : 008"  # scripted group (container) (typed FeaturePython)
  n = 4
  ref = C_element
FEATURE [App::DocumentObjectGroupPython] H_element019  label="H_element : 011"  # scripted group (container) (typed FeaturePython)
  n = 10
  ref = H_element
FEATURE [App::DocumentObjectGroupPython] O_element018  label="O_element : 007"  # scripted group (container) (typed FeaturePython)
  n = 1
  ref = O_element
FEATURE [App::DocumentObjectGroupPython] G4_N_BUTYL_ALCOHOL  label="G4_N-BUTYL_ALCOHOL"  # scripted group (container) (typed FeaturePython)
  Dunit = g/cm3
  Dvalue = 0.8098
  Group = -> [C_element020,H_element019,O_element018]
  conduct = 2
  density = 1
  expand = 3
  formula = G4_N-BUTYL_ALCOHOL
  name = G4_N-BUTYL_ALCOHOL
  specific = 4
FEATURE [App::DocumentObjectGroupPython] H_element020  label="H_element : 0.025"  # scripted group (container) (typed FeaturePython)
  n = 0.02468
FEATURE [App::DocumentObjectGroupPython] C_element021  label="C_element : 0.502"  # scripted group (container) (typed FeaturePython)
  n = 0.501611
FEATURE [App::DocumentObjectGroupPython] O_element019  label="O_element : 0.005"  # scripted group (container) (typed FeaturePython)
  n = 0.004527
FEATURE [App::DocumentObjectGroupPython] F_element004  label="F_element : 0.465"  # scripted group (container) (typed FeaturePython)
  n = 0.465209
FEATURE [App::DocumentObjectGroupPython] Si_element001  label="Si_element : 0.004"  # scripted group (container) (typed FeaturePython)
  n = 0.003973
FEATURE [App::DocumentObjectGroupPython] G4_C_552  label="G4_C-552"  # scripted group (container) (typed FeaturePython)
  Dunit = g/cm3
  Dvalue = 1.76
  Group = -> [H_element020,C_element021,O_element019,F_element004,Si_element001]
  conduct = 2
  density = 1
  expand = 3
  formula = G4_C-552
  name = G4_C-552
  specific = 4
FEATURE [App::DocumentObjectGroupPython] Cd_element001  label="Cd_element : 1"  # scripted group (container) (typed FeaturePython)
  n = 1
  ref = Cd_element
FEATURE [App::DocumentObjectGroupPython] Te_element001  label="Te_element : 1"  # scripted group (container) (typed FeaturePython)
  n = 1
  ref = Te_element
FEATURE [App::DocumentObjectGroupPython] G4_CADMIUM_TELLURIDE  # scripted group (container) (typed FeaturePython)
  Dunit = g/cm3
  Dvalue = 6.2
  Group = -> [Cd_element001,Te_element001]
  conduct = 2
  density = 1
  expand = 3
  formula = G4_CADMIUM_TELLURIDE
  name = G4_CADMIUM_TELLURIDE
  specific = 4
FEATURE [App::DocumentObjectGroupPython] Cd_element002  label="Cd_element : 002"  # scripted group (container) (typed FeaturePython)
  n = 1
  ref = Cd_element
FEATURE [App::DocumentObjectGroupPython] W_element001  label="W_element : 1"  # scripted group (container) (typed FeaturePython)
  n = 1
  ref = W_element
FEATURE [App::DocumentObjectGroupPython] O_element020  label="O_element : 008"  # scripted group (container) (typed FeaturePython)
  n = 4
  ref = O_element
FEATURE [App::DocumentObjectGroupPython] G4_CADMIUM_TUNGSTATE  # scripted group (container) (typed FeaturePython)
  Dunit = g/cm3
  Dvalue = 7.9
  Group = -> [Cd_element002,W_element001,O_element020]
  conduct = 2
  density = 1
  expand = 3
  formula = G4_CADMIUM_TUNGSTATE
  name = G4_CADMIUM_TUNGSTATE
  specific = 4
FEATURE [App::DocumentObjectGroupPython] Ca_element005  label="Ca_element : 1"  # scripted group (container) (typed FeaturePython)
  n = 1
  ref = Ca_element
FEATURE [App::DocumentObjectGroupPython] C_element022  label="C_element : 009"  # scripted group (container) (typed FeaturePython)
  n = 1
  ref = C_element
FEATURE [App::DocumentObjectGroupPython] O_element021  label="O_element : 009"  # scripted group (container) (typed FeaturePython)
  n = 3
  ref = O_element
FEATURE [App::DocumentObjectGroupPython] G4_CALCIUM_CARBONATE  # scripted group (container) (typed FeaturePython)
  Dunit = g/cm3
  Dvalue = 2.8
  Group = -> [Ca_element005,C_element022,O_element021]
  conduct = 2
  density = 1
  expand = 3
  formula = G4_CALCIUM_CARBONATE
  name = G4_CALCIUM_CARBONATE
  specific = 4
FEATURE [App::DocumentObjectGroupPython] Ca_element006  label="Ca_element : 002"  # scripted group (container) (typed FeaturePython)
  n = 1
  ref = Ca_element
FEATURE [App::DocumentObjectGroupPython] F_element005  label="F_element : 003"  # scripted group (container) (typed FeaturePython)
  n = 2
  ref = F_element
FEATURE [App::DocumentObjectGroupPython] G4_CALCIUM_FLUORIDE  # scripted group (container) (typed FeaturePython)
  Dunit = g/cm3
  Dvalue = 3.18
  Group = -> [Ca_element006,F_element005]
  conduct = 2
  density = 1
  expand = 3
  formula = G4_CALCIUM_FLUORIDE
  name = G4_CALCIUM_FLUORIDE
  specific = 4
FEATURE [App::DocumentObjectGroupPython] Ca_element007  label="Ca_element : 003"  # scripted group (container) (typed FeaturePython)
  n = 1
  ref = Ca_element
FEATURE [App::DocumentObjectGroupPython] O_element022  label="O_element : 010"  # scripted group (container) (typed FeaturePython)
  n = 1
  ref = O_element
FEATURE [App::DocumentObjectGroupPython] G4_CALCIUM_OXIDE  # scripted group (container) (typed FeaturePython)
  Dunit = g/cm3
  Dvalue = 3.3
  Group = -> [Ca_element007,O_element022]
  conduct = 2
  density = 1
  expand = 3
  formula = G4_CALCIUM_OXIDE
  name = G4_CALCIUM_OXIDE
  specific = 4
FEATURE [App::DocumentObjectGroupPython] Ca_element008  label="Ca_element : 004"  # scripted group (container) (typed FeaturePython)
  n = 1
  ref = Ca_element
FEATURE [App::DocumentObjectGroupPython] S_element007  label="S_element : 002"  # scripted group (container) (typed FeaturePython)
  n = 1
  ref = S_element
FEATURE [App::DocumentObjectGroupPython] O_element023  label="O_element : 011"  # scripted group (container) (typed FeaturePython)
  n = 4
  ref = O_element
FEATURE [App::DocumentObjectGroupPython] G4_CALCIUM_SULFATE  # scripted group (container) (typed FeaturePython)
  Dunit = g/cm3
  Dvalue = 2.96
  Group = -> [Ca_element008,S_element007,O_element023]
  conduct = 2
  density = 1
  expand = 3
  formula = G4_CALCIUM_SULFATE
  name = G4_CALCIUM_SULFATE
  specific = 4
FEATURE [App::DocumentObjectGroupPython] Ca_element009  label="Ca_element : 005"  # scripted group (container) (typed FeaturePython)
  n = 1
  ref = Ca_element
FEATURE [App::DocumentObjectGroupPython] W_element002  label="W_element : 002"  # scripted group (container) (typed FeaturePython)
  n = 1
  ref = W_element
FEATURE [App::DocumentObjectGroupPython] O_element024  label="O_element : 012"  # scripted group (container) (typed FeaturePython)
  n = 4
  ref = O_element
FEATURE [App::DocumentObjectGroupPython] G4_CALCIUM_TUNGSTATE  # scripted group (container) (typed FeaturePython)
  Dunit = g/cm3
  Dvalue = 6.062
  Group = -> [Ca_element009,W_element002,O_element024]
  conduct = 2
  density = 1
  expand = 3
  formula = G4_CALCIUM_TUNGSTATE
  name = G4_CALCIUM_TUNGSTATE
  specific = 4
FEATURE [App::DocumentObjectGroupPython] C_element023  label="C_element : 010"  # scripted group (container) (typed FeaturePython)
  n = 1
  ref = C_element
FEATURE [App::DocumentObjectGroupPython] O_element025  label="O_element : 013"  # scripted group (container) (typed FeaturePython)
  n = 2
  ref = O_element
FEATURE [App::DocumentObjectGroupPython] G4_CARBON_DIOXIDE  # scripted group (container) (typed FeaturePython)
  Dunit = g/cm3
  Dvalue = 0.00184212
  Group = -> [C_element023,O_element025]
  conduct = 2
  density = 1
  expand = 3
  formula = G4_CARBON_DIOXIDE
  name = G4_CARBON_DIOXIDE
  specific = 4
FEATURE [App::DocumentObjectGroupPython] C_element024  label="C_element : 011"  # scripted group (container) (typed FeaturePython)
  n = 1
  ref = C_element
FEATURE [App::DocumentObjectGroupPython] Cl_element004  label="Cl_element : 4"  # scripted group (container) (typed FeaturePython)
  n = 4
  ref = Cl_element
FEATURE [App::DocumentObjectGroupPython] G4_CARBON_TETRACHLORIDE  # scripted group (container) (typed FeaturePython)
  Dunit = g/cm3
  Dvalue = 1.594
  Group = -> [C_element024,Cl_element004]
  conduct = 2
  density = 1
  expand = 3
  formula = G4_CARBON_TETRACHLORIDE
  name = G4_CARBON_TETRACHLORIDE
  specific = 4
FEATURE [App::DocumentObjectGroupPython] C_element025  label="C_element : 012"  # scripted group (container) (typed FeaturePython)
  n = 6
  ref = C_element
FEATURE [App::DocumentObjectGroupPython] H_element021  label="H_element : 012"  # scripted group (container) (typed FeaturePython)
  n = 10
  ref = H_element
FEATURE [App::DocumentObjectGroupPython] O_element026  label="O_element : 5"  # scripted group (container) (typed FeaturePython)
  n = 5
  ref = O_element
FEATURE [App::DocumentObjectGroupPython] G4_CELLULOSE_CELLOPHANE  # scripted group (container) (typed FeaturePython)
  Dunit = g/cm3
  Dvalue = 1.42
  Group = -> [C_element025,H_element021,O_element026]
  conduct = 2
  density = 1
  expand = 3
  formula = G4_CELLULOSE_CELLOPHANE
  name = G4_CELLULOSE_CELLOPHANE
  specific = 4
FEATURE [App::DocumentObjectGroupPython] H_element022  label="H_element : 0.067"  # scripted group (container) (typed FeaturePython)
  n = 0.067125
FEATURE [App::DocumentObjectGroupPython] C_element026  label="C_element : 0.545"  # scripted group (container) (typed FeaturePython)
  n = 0.545403
FEATURE [App::DocumentObjectGroupPython] O_element027  label="O_element : 0.387"  # scripted group (container) (typed FeaturePython)
  n = 0.387472
FEATURE [App::DocumentObjectGroupPython] G4_CELLULOSE_BUTYRATE  # scripted group (container) (typed FeaturePython)
  Dunit = g/cm3
  Dvalue = 1.2
  Group = -> [H_element022,C_element026,O_element027]
  conduct = 2
  density = 1
  expand = 3
  formula = G4_CELLULOSE_BUTYRATE
  name = G4_CELLULOSE_BUTYRATE
  specific = 4
FEATURE [App::DocumentObjectGroupPython] H_element023  label="H_element : 0.029"  # scripted group (container) (typed FeaturePython)
  n = 0.029216
FEATURE [App::DocumentObjectGroupPython] C_element027  label="C_element : 0.271"  # scripted group (container) (typed FeaturePython)
  n = 0.271296
FEATURE [App::DocumentObjectGroupPython] N_element013  label="N_element : 0.121"  # scripted group (container) (typed FeaturePython)
  n = 0.121276
FEATURE [App::DocumentObjectGroupPython] O_element028  label="O_element : 0.578"  # scripted group (container) (typed FeaturePython)
  n = 0.578212
FEATURE [App::DocumentObjectGroupPython] G4_CELLULOSE_NITRATE  # scripted group (container) (typed FeaturePython)
  Dunit = g/cm3
  Dvalue = 1.49
  Group = -> [H_element023,C_element027,N_element013,O_element028]
  conduct = 2
  density = 1
  expand = 3
  formula = G4_CELLULOSE_NITRATE
  name = G4_CELLULOSE_NITRATE
  specific = 4
FEATURE [App::DocumentObjectGroupPython] H_element024  label="H_element : 0.108"  # scripted group (container) (typed FeaturePython)
  n = 0.107596
FEATURE [App::DocumentObjectGroupPython] N_element014  label="N_element : 0.001"  # scripted group (container) (typed FeaturePython)
  n = 0.0008
FEATURE [App::DocumentObjectGroupPython] O_element029  label="O_element : 0.875"  # scripted group (container) (typed FeaturePython)
  n = 0.874976
FEATURE [App::DocumentObjectGroupPython] S_element008  label="S_element : 0.015"  # scripted group (container) (typed FeaturePython)
  n = 0.014627
FEATURE [App::DocumentObjectGroupPython] Ce_element001  label="Ce_element : 0.002"  # scripted group (container) (typed FeaturePython)
  n = 0.002001
FEATURE [App::DocumentObjectGroupPython] G4_CERIC_SULFATE  # scripted group (container) (typed FeaturePython)
  Dunit = g/cm3
  Dvalue = 1.03
  Group = -> [H_element024,N_element014,O_element029,S_element008,Ce_element001]
  conduct = 2
  density = 1
  expand = 3
  formula = G4_CERIC_SULFATE
  name = G4_CERIC_SULFATE
  specific = 4
FEATURE [App::DocumentObjectGroupPython] Cs_element001  label="Cs_element : 1"  # scripted group (container) (typed FeaturePython)
  n = 1
  ref = Cs_element
FEATURE [App::DocumentObjectGroupPython] F_element006  label="F_element : 1"  # scripted group (container) (typed FeaturePython)
  n = 1
  ref = F_element
FEATURE [App::DocumentObjectGroupPython] G4_CESIUM_FLUORIDE  # scripted group (container) (typed FeaturePython)
  Dunit = g/cm3
  Dvalue = 4.115
  Group = -> [Cs_element001,F_element006]
  conduct = 2
  density = 1
  expand = 3
  formula = G4_CESIUM_FLUORIDE
  name = G4_CESIUM_FLUORIDE
  specific = 4
FEATURE [App::DocumentObjectGroupPython] Cs_element002  label="Cs_element : 002"  # scripted group (container) (typed FeaturePython)
  n = 1
  ref = Cs_element
FEATURE [App::DocumentObjectGroupPython] I_element001  label="I_element : 1"  # scripted group (container) (typed FeaturePython)
  n = 1
  ref = I_element
FEATURE [App::DocumentObjectGroupPython] G4_CESIUM_IODIDE  # scripted group (container) (typed FeaturePython)
  Dunit = g/cm3
  Dvalue = 4.51
  Group = -> [Cs_element002,I_element001]
  conduct = 2
  density = 1
  expand = 3
  formula = G4_CESIUM_IODIDE
  name = G4_CESIUM_IODIDE
  specific = 4
FEATURE [App::DocumentObjectGroupPython] C_element028  label="C_element : 013"  # scripted group (container) (typed FeaturePython)
  n = 6
  ref = C_element
FEATURE [App::DocumentObjectGroupPython] H_element025  label="H_element : 013"  # scripted group (container) (typed FeaturePython)
  n = 5
  ref = H_element
FEATURE [App::DocumentObjectGroupPython] Cl_element005  label="Cl_element : 1"  # scripted group (container) (typed FeaturePython)
  n = 1
  ref = Cl_element
FEATURE [App::DocumentObjectGroupPython] G4_CHLOROBENZENE  # scripted group (container) (typed FeaturePython)
  Dunit = g/cm3
  Dvalue = 1.1058
  Group = -> [C_element028,H_element025,Cl_element005]
  conduct = 2
  density = 1
  expand = 3
  formula = G4_CHLOROBENZENE
  name = G4_CHLOROBENZENE
  specific = 4
FEATURE [App::DocumentObjectGroupPython] C_element029  label="C_element : 014"  # scripted group (container) (typed FeaturePython)
  n = 1
  ref = C_element
FEATURE [App::DocumentObjectGroupPython] H_element026  label="H_element : 1"  # scripted group (container) (typed FeaturePython)
  n = 1
  ref = H_element
FEATURE [App::DocumentObjectGroupPython] Cl_element006  label="Cl_element : 3"  # scripted group (container) (typed FeaturePython)
  n = 3
  ref = Cl_element
FEATURE [App::DocumentObjectGroupPython] G4_CHLOROFORM  # scripted group (container) (typed FeaturePython)
  Dunit = g/cm3
  Dvalue = 1.4832
  Group = -> [C_element029,H_element026,Cl_element006]
  conduct = 2
  density = 1
  expand = 3
  formula = G4_CHLOROFORM
  name = G4_CHLOROFORM
  specific = 4
FEATURE [App::DocumentObjectGroupPython] H_element027  label="H_element : 0.010"  # scripted group (container) (typed FeaturePython)
  n = 0.01
FEATURE [App::DocumentObjectGroupPython] C_element030  label="C_element : 0.001"  # scripted group (container) (typed FeaturePython)
  n = 0.001
FEATURE [App::DocumentObjectGroupPython] O_element030  label="O_element : 0.529"  # scripted group (container) (typed FeaturePython)
  n = 0.529107
FEATURE [App::DocumentObjectGroupPython] Na_element005  label="Na_element : 0.016"  # scripted group (container) (typed FeaturePython)
  n = 0.016
FEATURE [App::DocumentObjectGroupPython] Mg_element003  label="Mg_element : 0.004"  # scripted group (container) (typed FeaturePython)
  n = 0.002
FEATURE [App::DocumentObjectGroupPython] Al_element002  label="Al_element : 0.034"  # scripted group (container) (typed FeaturePython)
  n = 0.033872
FEATURE [App::DocumentObjectGroupPython] Si_element002  label="Si_element : 0.337"  # scripted group (container) (typed FeaturePython)
  n = 0.337021
FEATURE [App::DocumentObjectGroupPython] K_element003  label="K_element : 0.013"  # scripted group (container) (typed FeaturePython)
  n = 0.013
FEATURE [App::DocumentObjectGroupPython] Ca_element010  label="Ca_element : 0.044"  # scripted group (container) (typed FeaturePython)
  n = 0.044
FEATURE [App::DocumentObjectGroupPython] Fe_element002  label="Fe_element : 0.014"  # scripted group (container) (typed FeaturePython)
  n = 0.014
FEATURE [App::DocumentObjectGroupPython] G4_CONCRETE  # scripted group (container) (typed FeaturePython)
  Dunit = g/cm3
  Dvalue = 2.3
  Group = -> [H_element027,C_element030,O_element030,Na_element005,Mg_element003,Al_element002,Si_element002,K_element003,Ca_element010,Fe_element002]
  conduct = 2
  density = 1
  expand = 3
  formula = G4_CONCRETE
  name = G4_CONCRETE
  specific = 4
FEATURE [App::DocumentObjectGroupPython] C_element031  label="C_element : 015"  # scripted group (container) (typed FeaturePython)
  n = 6
  ref = C_element
FEATURE [App::DocumentObjectGroupPython] H_element028  label="H_element : 12"  # scripted group (container) (typed FeaturePython)
  n = 12
  ref = H_element
FEATURE [App::DocumentObjectGroupPython] G4_CYCLOHEXANE  # scripted group (container) (typed FeaturePython)
  Dunit = g/cm3
  Dvalue = 0.779
  Group = -> [C_element031,H_element028]
  conduct = 2
  density = 1
  expand = 3
  formula = G4_CYCLOHEXANE
  name = G4_CYCLOHEXANE
  specific = 4
FEATURE [App::DocumentObjectGroupPython] C_element032  label="C_element : 016"  # scripted group (container) (typed FeaturePython)
  n = 6
  ref = C_element
FEATURE [App::DocumentObjectGroupPython] H_element029  label="H_element : 4"  # scripted group (container) (typed FeaturePython)
  n = 4
  ref = H_element
FEATURE [App::DocumentObjectGroupPython] Cl_element007  label="Cl_element : 2"  # scripted group (container) (typed FeaturePython)
  n = 2
  ref = Cl_element
FEATURE [App::DocumentObjectGroupPython] G4_1_2_DICHLOROBENZENE  label="G4_1.2-DICHLOROBENZENE"  # scripted group (container) (typed FeaturePython)
  Dunit = g/cm3
  Dvalue = 1.3048
  Group = -> [C_element032,H_element029,Cl_element007]
  conduct = 2
  density = 1
  expand = 3
  formula = G4_1.2-DICHLOROBENZENE
  name = G4_1.2-DICHLOROBENZENE
  specific = 4
FEATURE [App::DocumentObjectGroupPython] C_element033  label="C_element : 017"  # scripted group (container) (typed FeaturePython)
  n = 4
  ref = C_element
FEATURE [App::DocumentObjectGroupPython] H_element030  label="H_element : 8"  # scripted group (container) (typed FeaturePython)
  n = 8
  ref = H_element
FEATURE [App::DocumentObjectGroupPython] O_element031  label="O_element : 014"  # scripted group (container) (typed FeaturePython)
  n = 1
  ref = O_element
FEATURE [App::DocumentObjectGroupPython] Cl_element008  label="Cl_element : 005"  # scripted group (container) (typed FeaturePython)
  n = 2
  ref = Cl_element
FEATURE [App::DocumentObjectGroupPython] G4_DICHLORODIETHYL_ETHER  # scripted group (container) (typed FeaturePython)
  Dunit = g/cm3
  Dvalue = 1.2199
  Group = -> [C_element033,H_element030,O_element031,Cl_element008]
  conduct = 2
  density = 1
  expand = 3
  formula = G4_DICHLORODIETHYL_ETHER
  name = G4_DICHLORODIETHYL_ETHER
  specific = 4
FEATURE [App::DocumentObjectGroupPython] C_element034  label="C_element : 018"  # scripted group (container) (typed FeaturePython)
  n = 2
  ref = C_element
FEATURE [App::DocumentObjectGroupPython] H_element031  label="H_element : 014"  # scripted group (container) (typed FeaturePython)
  n = 4
  ref = H_element
FEATURE [App::DocumentObjectGroupPython] Cl_element009  label="Cl_element : 006"  # scripted group (container) (typed FeaturePython)
  n = 2
  ref = Cl_element
FEATURE [App::DocumentObjectGroupPython] G4_1_2_DICHLOROETHANE  label="G4_1.2-DICHLOROETHANE"  # scripted group (container) (typed FeaturePython)
  Dunit = g/cm3
  Dvalue = 1.2351
  Group = -> [C_element034,H_element031,Cl_element009]
  conduct = 2
  density = 1
  expand = 3
  formula = G4_1.2-DICHLOROETHANE
  name = G4_1.2-DICHLOROETHANE
  specific = 4
FEATURE [App::DocumentObjectGroupPython] C_element035  label="C_element : 019"  # scripted group (container) (typed FeaturePython)
  n = 4
  ref = C_element
FEATURE [App::DocumentObjectGroupPython] H_element032  label="H_element : 015"  # scripted group (container) (typed FeaturePython)
  n = 10
  ref = H_element
FEATURE [App::DocumentObjectGroupPython] O_element032  label="O_element : 015"  # scripted group (container) (typed FeaturePython)
  n = 1
  ref = O_element
FEATURE [App::DocumentObjectGroupPython] G4_DIETHYL_ETHER  # scripted group (container) (typed FeaturePython)
  Dunit = g/cm3
  Dvalue = 0.71378
  Group = -> [C_element035,H_element032,O_element032]
  conduct = 2
  density = 1
  expand = 3
  formula = G4_DIETHYL_ETHER
  name = G4_DIETHYL_ETHER
  specific = 4
FEATURE [App::DocumentObjectGroupPython] C_element036  label="C_element : 020"  # scripted group (container) (typed FeaturePython)
  n = 3
  ref = C_element
FEATURE [App::DocumentObjectGroupPython] H_element033  label="H_element : 016"  # scripted group (container) (typed FeaturePython)
  n = 7
  ref = H_element
FEATURE [App::DocumentObjectGroupPython] N_element015  label="N_element : 008"  # scripted group (container) (typed FeaturePython)
  n = 1
  ref = N_element
FEATURE [App::DocumentObjectGroupPython] O_element033  label="O_element : 016"  # scripted group (container) (typed FeaturePython)
  n = 1
  ref = O_element
FEATURE [App::DocumentObjectGroupPython] G4_N_N_DIMETHYL_FORMAMIDE  label="G4_N.N-DIMETHYL_FORMAMIDE"  # scripted group (container) (typed FeaturePython)
  Dunit = g/cm3
  Dvalue = 0.9487
  Group = -> [C_element036,H_element033,N_element015,O_element033]
  conduct = 2
  density = 1
  expand = 3
  formula = G4_N.N-DIMETHYL_FORMAMIDE
  name = G4_N.N-DIMETHYL_FORMAMIDE
  specific = 4
FEATURE [App::DocumentObjectGroupPython] C_element037  label="C_element : 021"  # scripted group (container) (typed FeaturePython)
  n = 2
  ref = C_element
FEATURE [App::DocumentObjectGroupPython] H_element034  label="H_element : 017"  # scripted group (container) (typed FeaturePython)
  n = 6
  ref = H_element
FEATURE [App::DocumentObjectGroupPython] O_element034  label="O_element : 017"  # scripted group (container) (typed FeaturePython)
  n = 1
  ref = O_element
FEATURE [App::DocumentObjectGroupPython] S_element009  label="S_element : 003"  # scripted group (container) (typed FeaturePython)
  n = 1
  ref = S_element
FEATURE [App::DocumentObjectGroupPython] G4_DIMETHYL_SULFOXIDE  # scripted group (container) (typed FeaturePython)
  Dunit = g/cm3
  Dvalue = 1.1014
  Group = -> [C_element037,H_element034,O_element034,S_element009]
  conduct = 2
  density = 1
  expand = 3
  formula = G4_DIMETHYL_SULFOXIDE
  name = G4_DIMETHYL_SULFOXIDE
  specific = 4
FEATURE [App::DocumentObjectGroupPython] C_element038  label="C_element : 022"  # scripted group (container) (typed FeaturePython)
  n = 2
  ref = C_element
FEATURE [App::DocumentObjectGroupPython] H_element035  label="H_element : 018"  # scripted group (container) (typed FeaturePython)
  n = 6
  ref = H_element
FEATURE [App::DocumentObjectGroupPython] G4_ETHANE  # scripted group (container) (typed FeaturePython)
  Dunit = g/cm3
  Dvalue = 0.00125324
  Group = -> [C_element038,H_element035]
  conduct = 2
  density = 1
  expand = 3
  formula = G4_ETHANE
  name = G4_ETHANE
  specific = 4
FEATURE [App::DocumentObjectGroupPython] C_element039  label="C_element : 023"  # scripted group (container) (typed FeaturePython)
  n = 2
  ref = C_element
FEATURE [App::DocumentObjectGroupPython] H_element036  label="H_element : 019"  # scripted group (container) (typed FeaturePython)
  n = 6
  ref = H_element
FEATURE [App::DocumentObjectGroupPython] O_element035  label="O_element : 018"  # scripted group (container) (typed FeaturePython)
  n = 1
  ref = O_element
FEATURE [App::DocumentObjectGroupPython] G4_ETHYL_ALCOHOL  # scripted group (container) (typed FeaturePython)
  Dunit = g/cm3
  Dvalue = 0.7893
  Group = -> [C_element039,H_element036,O_element035]
  conduct = 2
  density = 1
  expand = 3
  formula = G4_ETHYL_ALCOHOL
  name = G4_ETHYL_ALCOHOL
  specific = 4
FEATURE [App::DocumentObjectGroupPython] H_element037  label="H_element : 0.090"  # scripted group (container) (typed FeaturePython)
  n = 0.090027
FEATURE [App::DocumentObjectGroupPython] C_element040  label="C_element : 0.585"  # scripted group (container) (typed FeaturePython)
  n = 0.585182
FEATURE [App::DocumentObjectGroupPython] O_element036  label="O_element : 0.325"  # scripted group (container) (typed FeaturePython)
  n = 0.324791
FEATURE [App::DocumentObjectGroupPython] G4_ETHYL_CELLULOSE  # scripted group (container) (typed FeaturePython)
  Dunit = g/cm3
  Dvalue = 1.13
  Group = -> [H_element037,C_element040,O_element036]
  conduct = 2
  density = 1
  expand = 3
  formula = G4_ETHYL_CELLULOSE
  name = G4_ETHYL_CELLULOSE
  specific = 4
FEATURE [App::DocumentObjectGroupPython] C_element041  label="C_element : 024"  # scripted group (container) (typed FeaturePython)
  n = 2
  ref = C_element
FEATURE [App::DocumentObjectGroupPython] H_element038  label="H_element : 020"  # scripted group (container) (typed FeaturePython)
  n = 4
  ref = H_element
FEATURE [App::DocumentObjectGroupPython] G4_ETHYLENE  # scripted group (container) (typed FeaturePython)
  Dunit = g/cm3
  Dvalue = 0.00117497
  Group = -> [C_element041,H_element038]
  conduct = 2
  density = 1
  expand = 3
  formula = G4_ETHYLENE
  name = G4_ETHYLENE
  specific = 4
FEATURE [App::DocumentObjectGroupPython] H_element039  label="H_element : 0.096"  # scripted group (container) (typed FeaturePython)
  n = 0.096
FEATURE [App::DocumentObjectGroupPython] C_element042  label="C_element : 0.195"  # scripted group (container) (typed FeaturePython)
  n = 0.195
FEATURE [App::DocumentObjectGroupPython] N_element016  label="N_element : 0.057"  # scripted group (container) (typed FeaturePython)
  n = 0.057
FEATURE [App::DocumentObjectGroupPython] O_element037  label="O_element : 0.646"  # scripted group (container) (typed FeaturePython)
  n = 0.646
FEATURE [App::DocumentObjectGroupPython] Na_element006  label="Na_element : 0.017"  # scripted group (container) (typed FeaturePython)
  n = 0.001
FEATURE [App::DocumentObjectGroupPython] P_element005  label="P_element : 0.104"  # scripted group (container) (typed FeaturePython)
  n = 0.001
FEATURE [App::DocumentObjectGroupPython] S_element010  label="S_element : 0.016"  # scripted group (container) (typed FeaturePython)
  n = 0.003
FEATURE [App::DocumentObjectGroupPython] Cl_element010  label="Cl_element : 0.005"  # scripted group (container) (typed FeaturePython)
  n = 0.001
FEATURE [App::DocumentObjectGroupPython] G4_EYE_LENS_ICRP  # scripted group (container) (typed FeaturePython)
  Dunit = g/cm3
  Dvalue = 1.07
  Group = -> [H_element039,C_element042,N_element016,O_element037,Na_element006,P_element005,S_element010,Cl_element010]
  conduct = 2
  density = 1
  expand = 3
  formula = G4_EYE_LENS_ICRP
  name = G4_EYE_LENS_ICRP
  specific = 4
FEATURE [App::DocumentObjectGroupPython] Fe_element003  label="Fe_element : 2"  # scripted group (container) (typed FeaturePython)
  n = 2
  ref = Fe_element
FEATURE [App::DocumentObjectGroupPython] O_element038  label="O_element : 019"  # scripted group (container) (typed FeaturePython)
  n = 3
  ref = O_element
FEATURE [App::DocumentObjectGroupPython] G4_FERRIC_OXIDE  # scripted group (container) (typed FeaturePython)
  Dunit = g/cm3
  Dvalue = 5.2
  Group = -> [Fe_element003,O_element038]
  conduct = 2
  density = 1
  expand = 3
  formula = G4_FERRIC_OXIDE
  name = G4_FERRIC_OXIDE
  specific = 4
FEATURE [App::DocumentObjectGroupPython] Fe_element004  label="Fe_element : 1"  # scripted group (container) (typed FeaturePython)
  n = 1
  ref = Fe_element
FEATURE [App::DocumentObjectGroupPython] B_element003  label="B_element : 1"  # scripted group (container) (typed FeaturePython)
  n = 1
  ref = B_element
FEATURE [App::DocumentObjectGroupPython] G4_FERROBORIDE  # scripted group (container) (typed FeaturePython)
  Dunit = g/cm3
  Dvalue = 7.15
  Group = -> [Fe_element004,B_element003]
  conduct = 2
  density = 1
  expand = 3
  formula = G4_FERROBORIDE
  name = G4_FERROBORIDE
  specific = 4
FEATURE [App::DocumentObjectGroupPython] Fe_element005  label="Fe_element : 003"  # scripted group (container) (typed FeaturePython)
  n = 1
  ref = Fe_element
FEATURE [App::DocumentObjectGroupPython] O_element039  label="O_element : 020"  # scripted group (container) (typed FeaturePython)
  n = 1
  ref = O_element
FEATURE [App::DocumentObjectGroupPython] G4_FERROUS_OXIDE  # scripted group (container) (typed FeaturePython)
  Dunit = g/cm3
  Dvalue = 5.7
  Group = -> [Fe_element005,O_element039]
  conduct = 2
  density = 1
  expand = 3
  formula = G4_FERROUS_OXIDE
  name = G4_FERROUS_OXIDE
  specific = 4
FEATURE [App::DocumentObjectGroupPython] H_element040  label="H_element : 0.115"  # scripted group (container) (typed FeaturePython)
  n = 0.108259
FEATURE [App::DocumentObjectGroupPython] N_element017  label="N_element : 0.000"  # scripted group (container) (typed FeaturePython)
  n = 2.7e-05
FEATURE [App::DocumentObjectGroupPython] O_element040  label="O_element : 0.879"  # scripted group (container) (typed FeaturePython)
  n = 0.878636
FEATURE [App::DocumentObjectGroupPython] Na_element007  label="Na_element : 0.000"  # scripted group (container) (typed FeaturePython)
  n = 2.2e-05
FEATURE [App::DocumentObjectGroupPython] S_element011  label="S_element : 0.013"  # scripted group (container) (typed FeaturePython)
  n = 0.012968
FEATURE [App::DocumentObjectGroupPython] Cl_element011  label="Cl_element : 0.000"  # scripted group (container) (typed FeaturePython)
  n = 3.4e-05
FEATURE [App::DocumentObjectGroupPython] Fe_element006  label="Fe_element : 0.000"  # scripted group (container) (typed FeaturePython)
  n = 5.4e-05
FEATURE [App::DocumentObjectGroupPython] G4_FERROUS_SULFATE  # scripted group (container) (typed FeaturePython)
  Dunit = g/cm3
  Dvalue = 1.024
  Group = -> [H_element040,N_element017,O_element040,Na_element007,S_element011,Cl_element011,Fe_element006]
  conduct = 2
  density = 1
  expand = 3
  formula = G4_FERROUS_SULFATE
  name = G4_FERROUS_SULFATE
  specific = 4
FEATURE [App::DocumentObjectGroupPython] C_element043  label="C_element : 0.099"  # scripted group (container) (typed FeaturePython)
  n = 0.099335
FEATURE [App::DocumentObjectGroupPython] F_element007  label="F_element : 0.314"  # scripted group (container) (typed FeaturePython)
  n = 0.314247
FEATURE [App::DocumentObjectGroupPython] Cl_element012  label="Cl_element : 0.586"  # scripted group (container) (typed FeaturePython)
  n = 0.586418
FEATURE [App::DocumentObjectGroupPython] G4_FREON_12  label="G4_FREON-12"  # scripted group (container) (typed FeaturePython)
  Dunit = g/cm3
  Dvalue = 1.12
  Group = -> [C_element043,F_element007,Cl_element012]
  conduct = 2
  density = 1
  expand = 3
  formula = G4_FREON-12
  name = G4_FREON-12
  specific = 4
FEATURE [App::DocumentObjectGroupPython] C_element044  label="C_element : 0.057"  # scripted group (container) (typed FeaturePython)
  n = 0.057245
FEATURE [App::DocumentObjectGroupPython] F_element008  label="F_element : 0.181"  # scripted group (container) (typed FeaturePython)
  n = 0.181096
FEATURE [App::DocumentObjectGroupPython] Br_element001  label="Br_element : 0.762"  # scripted group (container) (typed FeaturePython)
  n = 0.761659
FEATURE [App::DocumentObjectGroupPython] G4_FREON_12B2  label="G4_FREON-12B2"  # scripted group (container) (typed FeaturePython)
  Dunit = g/cm3
  Dvalue = 1.8
  Group = -> [C_element044,F_element008,Br_element001]
  conduct = 2
  density = 1
  expand = 3
  formula = G4_FREON-12B2
  name = G4_FREON-12B2
  specific = 4
FEATURE [App::DocumentObjectGroupPython] C_element045  label="C_element : 0.115"  # scripted group (container) (typed FeaturePython)
  n = 0.114983
FEATURE [App::DocumentObjectGroupPython] F_element009  label="F_element : 0.546"  # scripted group (container) (typed FeaturePython)
  n = 0.545621
FEATURE [App::DocumentObjectGroupPython] Cl_element013  label="Cl_element : 0.339"  # scripted group (container) (typed FeaturePython)
  n = 0.339396
FEATURE [App::DocumentObjectGroupPython] G4_FREON_13  label="G4_FREON-13"  # scripted group (container) (typed FeaturePython)
  Dunit = g/cm3
  Dvalue = 0.95
  Group = -> [C_element045,F_element009,Cl_element013]
  conduct = 2
  density = 1
  expand = 3
  formula = G4_FREON-13
  name = G4_FREON-13
  specific = 4
FEATURE [App::DocumentObjectGroupPython] C_element046  label="C_element : 025"  # scripted group (container) (typed FeaturePython)
  n = 1
  ref = C_element
FEATURE [App::DocumentObjectGroupPython] F_element010  label="F_element : 3"  # scripted group (container) (typed FeaturePython)
  n = 3
  ref = F_element
FEATURE [App::DocumentObjectGroupPython] Br_element002  label="Br_element : 1"  # scripted group (container) (typed FeaturePython)
  n = 1
  ref = Br_element
FEATURE [App::DocumentObjectGroupPython] G4_FREON_13B1  label="G4_FREON-13B1"  # scripted group (container) (typed FeaturePython)
  Dunit = g/cm3
  Dvalue = 1.5
  Group = -> [C_element046,F_element010,Br_element002]
  conduct = 2
  density = 1
  expand = 3
  formula = G4_FREON-13B1
  name = G4_FREON-13B1
  specific = 4
FEATURE [App::DocumentObjectGroupPython] C_element047  label="C_element : 0.061"  # scripted group (container) (typed FeaturePython)
  n = 0.061309
FEATURE [App::DocumentObjectGroupPython] F_element011  label="F_element : 0.291"  # scripted group (container) (typed FeaturePython)
  n = 0.290924
FEATURE [App::DocumentObjectGroupPython] I_element002  label="I_element : 0.648"  # scripted group (container) (typed FeaturePython)
  n = 0.647767
FEATURE [App::DocumentObjectGroupPython] G4_FREON_13I1  label="G4_FREON-13I1"  # scripted group (container) (typed FeaturePython)
  Dunit = g/cm3
  Dvalue = 1.8
  Group = -> [C_element047,F_element011,I_element002]
  conduct = 2
  density = 1
  expand = 3
  formula = G4_FREON-13I1
  name = G4_FREON-13I1
  specific = 4
FEATURE [App::DocumentObjectGroupPython] Gd_element001  label="Gd_element : 2"  # scripted group (container) (typed FeaturePython)
  n = 2
  ref = Gd_element
FEATURE [App::DocumentObjectGroupPython] O_element041  label="O_element : 021"  # scripted group (container) (typed FeaturePython)
  n = 2
  ref = O_element
FEATURE [App::DocumentObjectGroupPython] S_element012  label="S_element : 004"  # scripted group (container) (typed FeaturePython)
  n = 1
  ref = S_element
FEATURE [App::DocumentObjectGroupPython] G4_GADOLINIUM_OXYSULFIDE  # scripted group (container) (typed FeaturePython)
  Dunit = g/cm3
  Dvalue = 7.44
  Group = -> [Gd_element001,O_element041,S_element012]
  conduct = 2
  density = 1
  expand = 3
  formula = G4_GADOLINIUM_OXYSULFIDE
  name = G4_GADOLINIUM_OXYSULFIDE
  specific = 4
FEATURE [App::DocumentObjectGroupPython] Ga_element001  label="Ga_element : 1"  # scripted group (container) (typed FeaturePython)
  n = 1
  ref = Ga_element
FEATURE [App::DocumentObjectGroupPython] As_element001  label="As_element : 1"  # scripted group (container) (typed FeaturePython)
  n = 1
  ref = As_element
FEATURE [App::DocumentObjectGroupPython] G4_GALLIUM_ARSENIDE  # scripted group (container) (typed FeaturePython)
  Dunit = g/cm3
  Dvalue = 5.31
  Group = -> [Ga_element001,As_element001]
  conduct = 2
  density = 1
  expand = 3
  formula = G4_GALLIUM_ARSENIDE
  name = G4_GALLIUM_ARSENIDE
  specific = 4
FEATURE [App::DocumentObjectGroupPython] H_element041  label="H_element : 0.081"  # scripted group (container) (typed FeaturePython)
  n = 0.08118
FEATURE [App::DocumentObjectGroupPython] C_element048  label="C_element : 0.416"  # scripted group (container) (typed FeaturePython)
  n = 0.41606
FEATURE [App::DocumentObjectGroupPython] N_element018  label="N_element : 0.111"  # scripted group (container) (typed FeaturePython)
  n = 0.11124
FEATURE [App::DocumentObjectGroupPython] O_element042  label="O_element : 0.381"  # scripted group (container) (typed FeaturePython)
  n = 0.38064
FEATURE [App::DocumentObjectGroupPython] S_element013  label="S_element : 0.011"  # scripted group (container) (typed FeaturePython)
  n = 0.01088
FEATURE [App::DocumentObjectGroupPython] G4_GEL_PHOTO_EMULSION  # scripted group (container) (typed FeaturePython)
  Dunit = g/cm3
  Dvalue = 1.2914
  Group = -> [H_element041,C_element048,N_element018,O_element042,S_element013]
  conduct = 2
  density = 1
  expand = 3
  formula = G4_GEL_PHOTO_EMULSION
  name = G4_GEL_PHOTO_EMULSION
  specific = 4
FEATURE [App::DocumentObjectGroupPython] B_element004  label="B_element : 0.040"  # scripted group (container) (typed FeaturePython)
  n = 0.0400639
FEATURE [App::DocumentObjectGroupPython] O_element043  label="O_element : 0.540"  # scripted group (container) (typed FeaturePython)
  n = 0.539561
FEATURE [App::DocumentObjectGroupPython] Na_element008  label="Na_element : 0.028"  # scripted group (container) (typed FeaturePython)
  n = 0.0281909
FEATURE [App::DocumentObjectGroupPython] Al_element003  label="Al_element : 0.012"  # scripted group (container) (typed FeaturePython)
  n = 0.011644
FEATURE [App::DocumentObjectGroupPython] Si_element003  label="Si_element : 0.377"  # scripted group (container) (typed FeaturePython)
  n = 0.377219
FEATURE [App::DocumentObjectGroupPython] K_element004  label="K_element : 0.014"  # scripted group (container) (typed FeaturePython)
  n = 0.00332099
FEATURE [App::DocumentObjectGroupPython] G4_Pyrex_Glass  # scripted group (container) (typed FeaturePython)
  Dunit = g/cm3
  Dvalue = 2.23
  Group = -> [B_element004,O_element043,Na_element008,Al_element003,Si_element003,K_element004]
  conduct = 2
  density = 1
  expand = 3
  formula = G4_Pyrex_Glass
  name = G4_Pyrex_Glass
  specific = 4
FEATURE [App::DocumentObjectGroupPython] O_element044  label="O_element : 0.156"  # scripted group (container) (typed FeaturePython)
  n = 0.156453
FEATURE [App::DocumentObjectGroupPython] Si_element004  label="Si_element : 0.081"  # scripted group (container) (typed FeaturePython)
  n = 0.080866
FEATURE [App::DocumentObjectGroupPython] Ti_element001  label="Ti_element : 0.008"  # scripted group (container) (typed FeaturePython)
  n = 0.008092
FEATURE [App::DocumentObjectGroupPython] As_element002  label="As_element : 0.003"  # scripted group (container) (typed FeaturePython)
  n = 0.002651
FEATURE [App::DocumentObjectGroupPython] Pb_element001  label="Pb_element : 0.752"  # scripted group (container) (typed FeaturePython)
  n = 0.751938
FEATURE [App::DocumentObjectGroupPython] G4_GLASS_LEAD  # scripted group (container) (typed FeaturePython)
  Dunit = g/cm3
  Dvalue = 6.22
  Group = -> [O_element044,Si_element004,Ti_element001,As_element002,Pb_element001]
  conduct = 2
  density = 1
  expand = 3
  formula = G4_GLASS_LEAD
  name = G4_GLASS_LEAD
  specific = 4
FEATURE [App::DocumentObjectGroupPython] O_element045  label="O_element : 0.460"  # scripted group (container) (typed FeaturePython)
  n = 0.4598
FEATURE [App::DocumentObjectGroupPython] Na_element009  label="Na_element : 0.096"  # scripted group (container) (typed FeaturePython)
  n = 0.0964411
FEATURE [App::DocumentObjectGroupPython] Si_element005  label="Si_element : 0.378"  # scripted group (container) (typed FeaturePython)
  n = 0.336553
FEATURE [App::DocumentObjectGroupPython] Ca_element011  label="Ca_element : 0.107"  # scripted group (container) (typed FeaturePython)
  n = 0.107205
FEATURE [App::DocumentObjectGroupPython] G4_GLASS_PLATE  # scripted group (container) (typed FeaturePython)
  Dunit = g/cm3
  Dvalue = 2.4
  Group = -> [O_element045,Na_element009,Si_element005,Ca_element011]
  conduct = 2
  density = 1
  expand = 3
  formula = G4_GLASS_PLATE
  name = G4_GLASS_PLATE
  specific = 4
FEATURE [App::DocumentObjectGroupPython] C_element049  label="C_element : 026"  # scripted group (container) (typed FeaturePython)
  n = 5
  ref = C_element
FEATURE [App::DocumentObjectGroupPython] H_element042  label="H_element : 021"  # scripted group (container) (typed FeaturePython)
  n = 10
  ref = H_element
FEATURE [App::DocumentObjectGroupPython] N_element019  label="N_element : 2"  # scripted group (container) (typed FeaturePython)
  n = 2
  ref = N_element
FEATURE [App::DocumentObjectGroupPython] O_element046  label="O_element : 022"  # scripted group (container) (typed FeaturePython)
  n = 3
  ref = O_element
FEATURE [App::DocumentObjectGroupPython] G4_GLUTAMINE  # scripted group (container) (typed FeaturePython)
  Dunit = g/cm3
  Dvalue = 1.46
  Group = -> [C_element049,H_element042,N_element019,O_element046]
  conduct = 2
  density = 1
  expand = 3
  formula = G4_GLUTAMINE
  name = G4_GLUTAMINE
  specific = 4
FEATURE [App::DocumentObjectGroupPython] C_element050  label="C_element : 027"  # scripted group (container) (typed FeaturePython)
  n = 3
  ref = C_element
FEATURE [App::DocumentObjectGroupPython] H_element043  label="H_element : 022"  # scripted group (container) (typed FeaturePython)
  n = 8
  ref = H_element
FEATURE [App::DocumentObjectGroupPython] O_element047  label="O_element : 023"  # scripted group (container) (typed FeaturePython)
  n = 3
  ref = O_element
FEATURE [App::DocumentObjectGroupPython] G4_GLYCEROL  # scripted group (container) (typed FeaturePython)
  Dunit = g/cm3
  Dvalue = 1.2613
  Group = -> [C_element050,H_element043,O_element047]
  conduct = 2
  density = 1
  expand = 3
  formula = G4_GLYCEROL
  name = G4_GLYCEROL
  specific = 4
FEATURE [App::DocumentObjectGroupPython] C_element051  label="C_element : 028"  # scripted group (container) (typed FeaturePython)
  n = 5
  ref = C_element
FEATURE [App::DocumentObjectGroupPython] H_element044  label="H_element : 023"  # scripted group (container) (typed FeaturePython)
  n = 5
  ref = H_element
FEATURE [App::DocumentObjectGroupPython] N_element020  label="N_element : 009"  # scripted group (container) (typed FeaturePython)
  n = 5
  ref = N_element
FEATURE [App::DocumentObjectGroupPython] O_element048  label="O_element : 024"  # scripted group (container) (typed FeaturePython)
  n = 1
  ref = O_element
FEATURE [App::DocumentObjectGroupPython] G4_GUANINE  # scripted group (container) (typed FeaturePython)
  Dunit = g/cm3
  Dvalue = 2.2
  Group = -> [C_element051,H_element044,N_element020,O_element048]
  conduct = 2
  density = 1
  expand = 3
  formula = G4_GUANINE
  name = G4_GUANINE
  specific = 4
FEATURE [App::DocumentObjectGroupPython] Ca_element012  label="Ca_element : 006"  # scripted group (container) (typed FeaturePython)
  n = 1
  ref = Ca_element
FEATURE [App::DocumentObjectGroupPython] S_element014  label="S_element : 005"  # scripted group (container) (typed FeaturePython)
  n = 1
  ref = S_element
FEATURE [App::DocumentObjectGroupPython] O_element049  label="O_element : 6"  # scripted group (container) (typed FeaturePython)
  n = 6
  ref = O_element
FEATURE [App::DocumentObjectGroupPython] H_element045  label="H_element : 024"  # scripted group (container) (typed FeaturePython)
  n = 4
  ref = H_element
FEATURE [App::DocumentObjectGroupPython] G4_GYPSUM  # scripted group (container) (typed FeaturePython)
  Dunit = g/cm3
  Dvalue = 2.32
  Group = -> [Ca_element012,S_element014,O_element049,H_element045]
  conduct = 2
  density = 1
  expand = 3
  formula = G4_GYPSUM
  name = G4_GYPSUM
  specific = 4
FEATURE [App::DocumentObjectGroupPython] C_element052  label="C_element : 7"  # scripted group (container) (typed FeaturePython)
  n = 7
  ref = C_element
FEATURE [App::DocumentObjectGroupPython] H_element046  label="H_element : 16"  # scripted group (container) (typed FeaturePython)
  n = 16
  ref = H_element
FEATURE [App::DocumentObjectGroupPython] G4_N_HEPTANE  label="G4_N-HEPTANE"  # scripted group (container) (typed FeaturePython)
  Dunit = g/cm3
  Dvalue = 0.68376
  Group = -> [C_element052,H_element046]
  conduct = 2
  density = 1
  expand = 3
  formula = G4_N-HEPTANE
  name = G4_N-HEPTANE
  specific = 4
FEATURE [App::DocumentObjectGroupPython] C_element053  label="C_element : 029"  # scripted group (container) (typed FeaturePython)
  n = 6
  ref = C_element
FEATURE [App::DocumentObjectGroupPython] H_element047  label="H_element : 14"  # scripted group (container) (typed FeaturePython)
  n = 14
  ref = H_element
FEATURE [App::DocumentObjectGroupPython] G4_N_HEXANE  label="G4_N-HEXANE"  # scripted group (container) (typed FeaturePython)
  Dunit = g/cm3
  Dvalue = 0.6603
  Group = -> [C_element053,H_element047]
  conduct = 2
  density = 1
  expand = 3
  formula = G4_N-HEXANE
  name = G4_N-HEXANE
  specific = 4
FEATURE [App::DocumentObjectGroupPython] C_element054  label="C_element : 22"  # scripted group (container) (typed FeaturePython)
  n = 22
  ref = C_element
FEATURE [App::DocumentObjectGroupPython] H_element048  label="H_element : 025"  # scripted group (container) (typed FeaturePython)
  n = 10
  ref = H_element
FEATURE [App::DocumentObjectGroupPython] N_element021  label="N_element : 010"  # scripted group (container) (typed FeaturePython)
  n = 2
  ref = N_element
FEATURE [App::DocumentObjectGroupPython] O_element050  label="O_element : 025"  # scripted group (container) (typed FeaturePython)
  n = 5
  ref = O_element
FEATURE [App::DocumentObjectGroupPython] G4_KAPTON  # scripted group (container) (typed FeaturePython)
  Dunit = g/cm3
  Dvalue = 1.42
  Group = -> [C_element054,H_element048,N_element021,O_element050]
  conduct = 2
  density = 1
  expand = 3
  formula = G4_KAPTON
  name = G4_KAPTON
  specific = 4
FEATURE [App::DocumentObjectGroupPython] La_element001  label="La_element : 1"  # scripted group (container) (typed FeaturePython)
  n = 1
  ref = La_element
FEATURE [App::DocumentObjectGroupPython] Br_element003  label="Br_element : 002"  # scripted group (container) (typed FeaturePython)
  n = 1
  ref = Br_element
FEATURE [App::DocumentObjectGroupPython] O_element051  label="O_element : 026"  # scripted group (container) (typed FeaturePython)
  n = 1
  ref = O_element
FEATURE [App::DocumentObjectGroupPython] G4_LANTHANUM_OXYBROMIDE  # scripted group (container) (typed FeaturePython)
  Dunit = g/cm3
  Dvalue = 6.28
  Group = -> [La_element001,Br_element003,O_element051]
  conduct = 2
  density = 1
  expand = 3
  formula = G4_LANTHANUM_OXYBROMIDE
  name = G4_LANTHANUM_OXYBROMIDE
  specific = 4
FEATURE [App::DocumentObjectGroupPython] La_element002  label="La_element : 2"  # scripted group (container) (typed FeaturePython)
  n = 2
  ref = La_element
FEATURE [App::DocumentObjectGroupPython] O_element052  label="O_element : 027"  # scripted group (container) (typed FeaturePython)
  n = 2
  ref = O_element
FEATURE [App::DocumentObjectGroupPython] S_element015  label="S_element : 006"  # scripted group (container) (typed FeaturePython)
  n = 1
  ref = S_element
FEATURE [App::DocumentObjectGroupPython] G4_LANTHANUM_OXYSULFIDE  # scripted group (container) (typed FeaturePython)
  Dunit = g/cm3
  Dvalue = 5.86
  Group = -> [La_element002,O_element052,S_element015]
  conduct = 2
  density = 1
  expand = 3
  formula = G4_LANTHANUM_OXYSULFIDE
  name = G4_LANTHANUM_OXYSULFIDE
  specific = 4
FEATURE [App::DocumentObjectGroupPython] O_element053  label="O_element : 0.072"  # scripted group (container) (typed FeaturePython)
  n = 0.071682
FEATURE [App::DocumentObjectGroupPython] Pb_element002  label="Pb_element : 0.928"  # scripted group (container) (typed FeaturePython)
  n = 0.928318
FEATURE [App::DocumentObjectGroupPython] G4_LEAD_OXIDE  # scripted group (container) (typed FeaturePython)
  Dunit = g/cm3
  Dvalue = 9.53
  Group = -> [O_element053,Pb_element002]
  conduct = 2
  density = 1
  expand = 3
  formula = G4_LEAD_OXIDE
  name = G4_LEAD_OXIDE
  specific = 4
FEATURE [App::DocumentObjectGroupPython] Li_element001  label="Li_element : 1"  # scripted group (container) (typed FeaturePython)
  n = 1
  ref = Li_element
FEATURE [App::DocumentObjectGroupPython] N_element022  label="N_element : 011"  # scripted group (container) (typed FeaturePython)
  n = 1
  ref = N_element
FEATURE [App::DocumentObjectGroupPython] H_element049  label="H_element : 026"  # scripted group (container) (typed FeaturePython)
  n = 2
  ref = H_element
FEATURE [App::DocumentObjectGroupPython] G4_LITHIUM_AMIDE  # scripted group (container) (typed FeaturePython)
  Dunit = g/cm3
  Dvalue = 1.178
  Group = -> [Li_element001,N_element022,H_element049]
  conduct = 2
  density = 1
  expand = 3
  formula = G4_LITHIUM_AMIDE
  name = G4_LITHIUM_AMIDE
  specific = 4
FEATURE [App::DocumentObjectGroupPython] Li_element002  label="Li_element : 2"  # scripted group (container) (typed FeaturePython)
  n = 2
  ref = Li_element
FEATURE [App::DocumentObjectGroupPython] C_element055  label="C_element : 030"  # scripted group (container) (typed FeaturePython)
  n = 1
  ref = C_element
FEATURE [App::DocumentObjectGroupPython] O_element054  label="O_element : 028"  # scripted group (container) (typed FeaturePython)
  n = 3
  ref = O_element
FEATURE [App::DocumentObjectGroupPython] G4_LITHIUM_CARBONATE  # scripted group (container) (typed FeaturePython)
  Dunit = g/cm3
  Dvalue = 2.11
  Group = -> [Li_element002,C_element055,O_element054]
  conduct = 2
  density = 1
  expand = 3
  formula = G4_LITHIUM_CARBONATE
  name = G4_LITHIUM_CARBONATE
  specific = 4
FEATURE [App::DocumentObjectGroupPython] Li_element003  label="Li_element : 003"  # scripted group (container) (typed FeaturePython)
  n = 1
  ref = Li_element
FEATURE [App::DocumentObjectGroupPython] F_element012  label="F_element : 004"  # scripted group (container) (typed FeaturePython)
  n = 1
  ref = F_element
FEATURE [App::DocumentObjectGroupPython] G4_LITHIUM_FLUORIDE  # scripted group (container) (typed FeaturePython)
  Dunit = g/cm3
  Dvalue = 2.635
  Group = -> [Li_element003,F_element012]
  conduct = 2
  density = 1
  expand = 3
  formula = G4_LITHIUM_FLUORIDE
  name = G4_LITHIUM_FLUORIDE
  specific = 4
FEATURE [App::DocumentObjectGroupPython] Li_element004  label="Li_element : 004"  # scripted group (container) (typed FeaturePython)
  n = 1
  ref = Li_element
FEATURE [App::DocumentObjectGroupPython] H_element050  label="H_element : 027"  # scripted group (container) (typed FeaturePython)
  n = 1
  ref = H_element
FEATURE [App::DocumentObjectGroupPython] G4_LITHIUM_HYDRIDE  # scripted group (container) (typed FeaturePython)
  Dunit = g/cm3
  Dvalue = 0.82
  Group = -> [Li_element004,H_element050]
  conduct = 2
  density = 1
  expand = 3
  formula = G4_LITHIUM_HYDRIDE
  name = G4_LITHIUM_HYDRIDE
  specific = 4
FEATURE [App::DocumentObjectGroupPython] Li_element005  label="Li_element : 005"  # scripted group (container) (typed FeaturePython)
  n = 1
  ref = Li_element
FEATURE [App::DocumentObjectGroupPython] I_element003  label="I_element : 002"  # scripted group (container) (typed FeaturePython)
  n = 1
  ref = I_element
FEATURE [App::DocumentObjectGroupPython] G4_LITHIUM_IODIDE  # scripted group (container) (typed FeaturePython)
  Dunit = g/cm3
  Dvalue = 3.494
  Group = -> [Li_element005,I_element003]
  conduct = 2
  density = 1
  expand = 3
  formula = G4_LITHIUM_IODIDE
  name = G4_LITHIUM_IODIDE
  specific = 4
FEATURE [App::DocumentObjectGroupPython] Li_element006  label="Li_element : 006"  # scripted group (container) (typed FeaturePython)
  n = 2
  ref = Li_element
FEATURE [App::DocumentObjectGroupPython] O_element055  label="O_element : 029"  # scripted group (container) (typed FeaturePython)
  n = 1
  ref = O_element
FEATURE [App::DocumentObjectGroupPython] G4_LITHIUM_OXIDE  # scripted group (container) (typed FeaturePython)
  Dunit = g/cm3
  Dvalue = 2.013
  Group = -> [Li_element006,O_element055]
  conduct = 2
  density = 1
  expand = 3
  formula = G4_LITHIUM_OXIDE
  name = G4_LITHIUM_OXIDE
  specific = 4
FEATURE [App::DocumentObjectGroupPython] Li_element007  label="Li_element : 007"  # scripted group (container) (typed FeaturePython)
  n = 2
  ref = Li_element
FEATURE [App::DocumentObjectGroupPython] B_element005  label="B_element : 005"  # scripted group (container) (typed FeaturePython)
  n = 4
  ref = B_element
FEATURE [App::DocumentObjectGroupPython] O_element056  label="O_element : 7"  # scripted group (container) (typed FeaturePython)
  n = 7
  ref = O_element
FEATURE [App::DocumentObjectGroupPython] G4_LITHIUM_TETRABORATE  # scripted group (container) (typed FeaturePython)
  Dunit = g/cm3
  Dvalue = 2.44
  Group = -> [Li_element007,B_element005,O_element056]
  conduct = 2
  density = 1
  expand = 3
  formula = G4_LITHIUM_TETRABORATE
  name = G4_LITHIUM_TETRABORATE
  specific = 4
FEATURE [App::DocumentObjectGroupPython] H_element051  label="H_element : 0.105"  # scripted group (container) (typed FeaturePython)
  n = 0.105
FEATURE [App::DocumentObjectGroupPython] C_element056  label="C_element : 0.083"  # scripted group (container) (typed FeaturePython)
  n = 0.083
FEATURE [App::DocumentObjectGroupPython] N_element023  label="N_element : 0.023"  # scripted group (container) (typed FeaturePython)
  n = 0.023
FEATURE [App::DocumentObjectGroupPython] O_element057  label="O_element : 0.779"  # scripted group (container) (typed FeaturePython)
  n = 0.779
FEATURE [App::DocumentObjectGroupPython] Na_element010  label="Na_element : 0.097"  # scripted group (container) (typed FeaturePython)
  n = 0.002
FEATURE [App::DocumentObjectGroupPython] P_element006  label="P_element : 0.105"  # scripted group (container) (typed FeaturePython)
  n = 0.001
FEATURE [App::DocumentObjectGroupPython] S_element016  label="S_element : 0.017"  # scripted group (container) (typed FeaturePython)
  n = 0.002
FEATURE [App::DocumentObjectGroupPython] Cl_element014  label="Cl_element : 0.587"  # scripted group (container) (typed FeaturePython)
  n = 0.003
FEATURE [App::DocumentObjectGroupPython] K_element005  label="K_element : 0.015"  # scripted group (container) (typed FeaturePython)
  n = 0.002
FEATURE [App::DocumentObjectGroupPython] G4_LUNG_ICRP  # scripted group (container) (typed FeaturePython)
  Dunit = g/cm3
  Dvalue = 1.04
  Group = -> [H_element051,C_element056,N_element023,O_element057,Na_element010,P_element006,S_element016,Cl_element014,K_element005]
  conduct = 2
  density = 1
  expand = 3
  formula = G4_LUNG_ICRP
  name = G4_LUNG_ICRP
  specific = 4
FEATURE [App::DocumentObjectGroupPython] H_element052  label="H_element : 0.116"  # scripted group (container) (typed FeaturePython)
  n = 0.114318
FEATURE [App::DocumentObjectGroupPython] C_element057  label="C_element : 0.656"  # scripted group (container) (typed FeaturePython)
  n = 0.655824
FEATURE [App::DocumentObjectGroupPython] O_element058  label="O_element : 0.092"  # scripted group (container) (typed FeaturePython)
  n = 0.0921831
FEATURE [App::DocumentObjectGroupPython] Mg_element004  label="Mg_element : 0.135"  # scripted group (container) (typed FeaturePython)
  n = 0.134792
FEATURE [App::DocumentObjectGroupPython] Ca_element013  label="Ca_element : 0.003"  # scripted group (container) (typed FeaturePython)
  n = 0.002883
FEATURE [App::DocumentObjectGroupPython] G4_M3_WAX  # scripted group (container) (typed FeaturePython)
  Dunit = g/cm3
  Dvalue = 1.05
  Group = -> [H_element052,C_element057,O_element058,Mg_element004,Ca_element013]
  conduct = 2
  density = 1
  expand = 3
  formula = G4_M3_WAX
  name = G4_M3_WAX
  specific = 4
FEATURE [App::DocumentObjectGroupPython] Mg_element005  label="Mg_element : 1"  # scripted group (container) (typed FeaturePython)
  n = 1
  ref = Mg_element
FEATURE [App::DocumentObjectGroupPython] C_element058  label="C_element : 031"  # scripted group (container) (typed FeaturePython)
  n = 1
  ref = C_element
FEATURE [App::DocumentObjectGroupPython] O_element059  label="O_element : 030"  # scripted group (container) (typed FeaturePython)
  n = 3
  ref = O_element
FEATURE [App::DocumentObjectGroupPython] G4_MAGNESIUM_CARBONATE  # scripted group (container) (typed FeaturePython)
  Dunit = g/cm3
  Dvalue = 2.958
  Group = -> [Mg_element005,C_element058,O_element059]
  conduct = 2
  density = 1
  expand = 3
  formula = G4_MAGNESIUM_CARBONATE
  name = G4_MAGNESIUM_CARBONATE
  specific = 4
FEATURE [App::DocumentObjectGroupPython] Mg_element006  label="Mg_element : 002"  # scripted group (container) (typed FeaturePython)
  n = 1
  ref = Mg_element
FEATURE [App::DocumentObjectGroupPython] F_element013  label="F_element : 005"  # scripted group (container) (typed FeaturePython)
  n = 2
  ref = F_element
FEATURE [App::DocumentObjectGroupPython] G4_MAGNESIUM_FLUORIDE  # scripted group (container) (typed FeaturePython)
  Dunit = g/cm3
  Dvalue = 3
  Group = -> [Mg_element006,F_element013]
  conduct = 2
  density = 1
  expand = 3
  formula = G4_MAGNESIUM_FLUORIDE
  name = G4_MAGNESIUM_FLUORIDE
  specific = 4
FEATURE [App::DocumentObjectGroupPython] Mg_element007  label="Mg_element : 003"  # scripted group (container) (typed FeaturePython)
  n = 1
  ref = Mg_element
FEATURE [App::DocumentObjectGroupPython] O_element060  label="O_element : 031"  # scripted group (container) (typed FeaturePython)
  n = 1
  ref = O_element
FEATURE [App::DocumentObjectGroupPython] G4_MAGNESIUM_OXIDE  # scripted group (container) (typed FeaturePython)
  Dunit = g/cm3
  Dvalue = 3.58
  Group = -> [Mg_element007,O_element060]
  conduct = 2
  density = 1
  expand = 3
  formula = G4_MAGNESIUM_OXIDE
  name = G4_MAGNESIUM_OXIDE
  specific = 4
FEATURE [App::DocumentObjectGroupPython] Mg_element008  label="Mg_element : 004"  # scripted group (container) (typed FeaturePython)
  n = 1
  ref = Mg_element
FEATURE [App::DocumentObjectGroupPython] B_element006  label="B_element : 006"  # scripted group (container) (typed FeaturePython)
  n = 4
  ref = B_element
FEATURE [App::DocumentObjectGroupPython] O_element061  label="O_element : 032"  # scripted group (container) (typed FeaturePython)
  n = 7
  ref = O_element
FEATURE [App::DocumentObjectGroupPython] G4_MAGNESIUM_TETRABORATE  # scripted group (container) (typed FeaturePython)
  Dunit = g/cm3
  Dvalue = 2.53
  Group = -> [Mg_element008,B_element006,O_element061]
  conduct = 2
  density = 1
  expand = 3
  formula = G4_MAGNESIUM_TETRABORATE
  name = G4_MAGNESIUM_TETRABORATE
  specific = 4
FEATURE [App::DocumentObjectGroupPython] Hg_element001  label="Hg_element : 1"  # scripted group (container) (typed FeaturePython)
  n = 1
  ref = Hg_element
FEATURE [App::DocumentObjectGroupPython] I_element004  label="I_element : 2"  # scripted group (container) (typed FeaturePython)
  n = 2
  ref = I_element
FEATURE [App::DocumentObjectGroupPython] G4_MERCURIC_IODIDE  # scripted group (container) (typed FeaturePython)
  Dunit = g/cm3
  Dvalue = 6.36
  Group = -> [Hg_element001,I_element004]
  conduct = 2
  density = 1
  expand = 3
  formula = G4_MERCURIC_IODIDE
  name = G4_MERCURIC_IODIDE
  specific = 4
FEATURE [App::DocumentObjectGroupPython] C_element059  label="C_element : 032"  # scripted group (container) (typed FeaturePython)
  n = 1
  ref = C_element
FEATURE [App::DocumentObjectGroupPython] H_element053  label="H_element : 028"  # scripted group (container) (typed FeaturePython)
  n = 4
  ref = H_element
FEATURE [App::DocumentObjectGroupPython] G4_METHANE  # scripted group (container) (typed FeaturePython)
  Dunit = g/cm3
  Dvalue = 0.000667151
  Group = -> [C_element059,H_element053]
  conduct = 2
  density = 1
  expand = 3
  formula = G4_METHANE
  name = G4_METHANE
  specific = 4
FEATURE [App::DocumentObjectGroupPython] C_element060  label="C_element : 033"  # scripted group (container) (typed FeaturePython)
  n = 1
  ref = C_element
FEATURE [App::DocumentObjectGroupPython] H_element054  label="H_element : 029"  # scripted group (container) (typed FeaturePython)
  n = 4
  ref = H_element
FEATURE [App::DocumentObjectGroupPython] O_element062  label="O_element : 033"  # scripted group (container) (typed FeaturePython)
  n = 1
  ref = O_element
FEATURE [App::DocumentObjectGroupPython] G4_METHANOL  # scripted group (container) (typed FeaturePython)
  Dunit = g/cm3
  Dvalue = 0.7914
  Group = -> [C_element060,H_element054,O_element062]
  conduct = 2
  density = 1
  expand = 3
  formula = G4_METHANOL
  name = G4_METHANOL
  specific = 4
FEATURE [App::DocumentObjectGroupPython] H_element055  label="H_element : 0.134"  # scripted group (container) (typed FeaturePython)
  n = 0.13404
FEATURE [App::DocumentObjectGroupPython] C_element061  label="C_element : 0.778"  # scripted group (container) (typed FeaturePython)
  n = 0.77796
FEATURE [App::DocumentObjectGroupPython] O_element063  label="O_element : 0.035"  # scripted group (container) (typed FeaturePython)
  n = 0.03502
FEATURE [App::DocumentObjectGroupPython] Mg_element009  label="Mg_element : 0.039"  # scripted group (container) (typed FeaturePython)
  n = 0.038594
FEATURE [App::DocumentObjectGroupPython] Ti_element002  label="Ti_element : 0.014"  # scripted group (container) (typed FeaturePython)
  n = 0.014386
FEATURE [App::DocumentObjectGroupPython] G4_MIX_D_WAX  # scripted group (container) (typed FeaturePython)
  Dunit = g/cm3
  Dvalue = 0.99
  Group = -> [H_element055,C_element061,O_element063,Mg_element009,Ti_element002]
  conduct = 2
  density = 1
  expand = 3
  formula = G4_MIX_D_WAX
  name = G4_MIX_D_WAX
  specific = 4
FEATURE [App::DocumentObjectGroupPython] H_element056  label="H_element : 0.135"  # scripted group (container) (typed FeaturePython)
  n = 0.081192
FEATURE [App::DocumentObjectGroupPython] C_element062  label="C_element : 0.583"  # scripted group (container) (typed FeaturePython)
  n = 0.583442
FEATURE [App::DocumentObjectGroupPython] N_element024  label="N_element : 0.018"  # scripted group (container) (typed FeaturePython)
  n = 0.017798
FEATURE [App::DocumentObjectGroupPython] O_element064  label="O_element : 0.186"  # scripted group (container) (typed FeaturePython)
  n = 0.186381
FEATURE [App::DocumentObjectGroupPython] Mg_element010  label="Mg_element : 0.130"  # scripted group (container) (typed FeaturePython)
  n = 0.130287
FEATURE [App::DocumentObjectGroupPython] Cl_element015  label="Cl_element : 0.588"  # scripted group (container) (typed FeaturePython)
  n = 0.0009
FEATURE [App::DocumentObjectGroupPython] G4_MS20_TISSUE  # scripted group (container) (typed FeaturePython)
  Dunit = g/cm3
  Dvalue = 1
  Group = -> [H_element056,C_element062,N_element024,O_element064,Mg_element010,Cl_element015]
  conduct = 2
  density = 1
  expand = 3
  formula = G4_MS20_TISSUE
  name = G4_MS20_TISSUE
  specific = 4
FEATURE [App::DocumentObjectGroupPython] H_element057  label="H_element : 0.136"  # scripted group (container) (typed FeaturePython)
  n = 0.102
FEATURE [App::DocumentObjectGroupPython] C_element063  label="C_element : 0.143"  # scripted group (container) (typed FeaturePython)
  n = 0.143
FEATURE [App::DocumentObjectGroupPython] N_element025  label="N_element : 0.034"  # scripted group (container) (typed FeaturePython)
  n = 0.034
FEATURE [App::DocumentObjectGroupPython] O_element065  label="O_element : 0.710"  # scripted group (container) (typed FeaturePython)
  n = 0.71
FEATURE [App::DocumentObjectGroupPython] Na_element011  label="Na_element : 0.098"  # scripted group (container) (typed FeaturePython)
  n = 0.001
FEATURE [App::DocumentObjectGroupPython] P_element007  label="P_element : 0.002"  # scripted group (container) (typed FeaturePython)
  n = 0.002
FEATURE [App::DocumentObjectGroupPython] S_element017  label="S_element : 0.018"  # scripted group (container) (typed FeaturePython)
  n = 0.003
FEATURE [App::DocumentObjectGroupPython] Cl_element016  label="Cl_element : 0.589"  # scripted group (container) (typed FeaturePython)
  n = 0.001
FEATURE [App::DocumentObjectGroupPython] K_element006  label="K_element : 0.004"  # scripted group (container) (typed FeaturePython)
  n = 0.004
FEATURE [App::DocumentObjectGroupPython] G4_MUSCLE_SKELETAL_ICRP  # scripted group (container) (typed FeaturePython)
  Dunit = g/cm3
  Dvalue = 1.05
  Group = -> [H_element057,C_element063,N_element025,O_element065,Na_element011,P_element007,S_element017,Cl_element016,K_element006]
  conduct = 2
  density = 1
  expand = 3
  formula = G4_MUSCLE_SKELETAL_ICRP
  name = G4_MUSCLE_SKELETAL_ICRP
  specific = 4
FEATURE [App::DocumentObjectGroupPython] H_element058  label="H_element : 0.137"  # scripted group (container) (typed FeaturePython)
  n = 0.102102
FEATURE [App::DocumentObjectGroupPython] C_element064  label="C_element : 0.123"  # scripted group (container) (typed FeaturePython)
  n = 0.123123
FEATURE [App::DocumentObjectGroupPython] N_element026  label="N_element : 0.756"  # scripted group (container) (typed FeaturePython)
  n = 0.035035
FEATURE [App::DocumentObjectGroupPython] O_element066  label="O_element : 0.730"  # scripted group (container) (typed FeaturePython)
  n = 0.72973
FEATURE [App::DocumentObjectGroupPython] Na_element012  label="Na_element : 0.099"  # scripted group (container) (typed FeaturePython)
  n = 0.001001
FEATURE [App::DocumentObjectGroupPython] P_element008  label="P_element : 0.106"  # scripted group (container) (typed FeaturePython)
  n = 0.002002
FEATURE [App::DocumentObjectGroupPython] S_element018  label="S_element : 0.019"  # scripted group (container) (typed FeaturePython)
  n = 0.004004
FEATURE [App::DocumentObjectGroupPython] K_element007  label="K_element : 0.016"  # scripted group (container) (typed FeaturePython)
  n = 0.003003
FEATURE [App::DocumentObjectGroupPython] G4_MUSCLE_STRIATED_ICRU  # scripted group (container) (typed FeaturePython)
  Dunit = g/cm3
  Dvalue = 1.04
  Group = -> [H_element058,C_element064,N_element026,O_element066,Na_element012,P_element008,S_element018,K_element007]
  conduct = 2
  density = 1
  expand = 3
  formula = G4_MUSCLE_STRIATED_ICRU
  name = G4_MUSCLE_STRIATED_ICRU
  specific = 4
FEATURE [App::DocumentObjectGroupPython] H_element059  label="H_element : 0.098"  # scripted group (container) (typed FeaturePython)
  n = 0.0982341
FEATURE [App::DocumentObjectGroupPython] C_element065  label="C_element : 0.156"  # scripted group (container) (typed FeaturePython)
  n = 0.156214
FEATURE [App::DocumentObjectGroupPython] N_element027  label="N_element : 0.757"  # scripted group (container) (typed FeaturePython)
  n = 0.035451
FEATURE [App::DocumentObjectGroupPython] O_element067  label="O_element : 0.880"  # scripted group (container) (typed FeaturePython)
  n = 0.710101
FEATURE [App::DocumentObjectGroupPython] G4_MUSCLE_WITH_SUCROSE  # scripted group (container) (typed FeaturePython)
  Dunit = g/cm3
  Dvalue = 1.11
  Group = -> [H_element059,C_element065,N_element027,O_element067]
  conduct = 2
  density = 1
  expand = 3
  formula = G4_MUSCLE_WITH_SUCROSE
  name = G4_MUSCLE_WITH_SUCROSE
  specific = 4
FEATURE [App::DocumentObjectGroupPython] H_element060  label="H_element : 0.138"  # scripted group (container) (typed FeaturePython)
  n = 0.101969
FEATURE [App::DocumentObjectGroupPython] C_element066  label="C_element : 0.120"  # scripted group (container) (typed FeaturePython)
  n = 0.120058
FEATURE [App::DocumentObjectGroupPython] N_element028  label="N_element : 0.758"  # scripted group (container) (typed FeaturePython)
  n = 0.035451
FEATURE [App::DocumentObjectGroupPython] O_element068  label="O_element : 0.743"  # scripted group (container) (typed FeaturePython)
  n = 0.742522
FEATURE [App::DocumentObjectGroupPython] G4_MUSCLE_WITHOUT_SUCROSE  # scripted group (container) (typed FeaturePython)
  Dunit = g/cm3
  Dvalue = 1.07
  Group = -> [H_element060,C_element066,N_element028,O_element068]
  conduct = 2
  density = 1
  expand = 3
  formula = G4_MUSCLE_WITHOUT_SUCROSE
  name = G4_MUSCLE_WITHOUT_SUCROSE
  specific = 4
FEATURE [App::DocumentObjectGroupPython] C_element067  label="C_element : 10"  # scripted group (container) (typed FeaturePython)
  n = 10
  ref = C_element
FEATURE [App::DocumentObjectGroupPython] H_element061  label="H_element : 030"  # scripted group (container) (typed FeaturePython)
  n = 8
  ref = H_element
FEATURE [App::DocumentObjectGroupPython] G4_NAPHTHALENE  # scripted group (container) (typed FeaturePython)
  Dunit = g/cm3
  Dvalue = 1.145
  Group = -> [C_element067,H_element061]
  conduct = 2
  density = 1
  expand = 3
  formula = G4_NAPHTHALENE
  name = G4_NAPHTHALENE
  specific = 4
FEATURE [App::DocumentObjectGroupPython] C_element068  label="C_element : 034"  # scripted group (container) (typed FeaturePython)
  n = 6
  ref = C_element
FEATURE [App::DocumentObjectGroupPython] H_element062  label="H_element : 031"  # scripted group (container) (typed FeaturePython)
  n = 5
  ref = H_element
FEATURE [App::DocumentObjectGroupPython] N_element029  label="N_element : 012"  # scripted group (container) (typed FeaturePython)
  n = 1
  ref = N_element
FEATURE [App::DocumentObjectGroupPython] O_element069  label="O_element : 034"  # scripted group (container) (typed FeaturePython)
  n = 2
  ref = O_element
FEATURE [App::DocumentObjectGroupPython] G4_NITROBENZENE  # scripted group (container) (typed FeaturePython)
  Dunit = g/cm3
  Dvalue = 1.19867
  Group = -> [C_element068,H_element062,N_element029,O_element069]
  conduct = 2
  density = 1
  expand = 3
  formula = G4_NITROBENZENE
  name = G4_NITROBENZENE
  specific = 4
FEATURE [App::DocumentObjectGroupPython] N_element030  label="N_element : 013"  # scripted group (container) (typed FeaturePython)
  n = 2
  ref = N_element
FEATURE [App::DocumentObjectGroupPython] O_element070  label="O_element : 035"  # scripted group (container) (typed FeaturePython)
  n = 1
  ref = O_element
FEATURE [App::DocumentObjectGroupPython] G4_NITROUS_OXIDE  # scripted group (container) (typed FeaturePython)
  Dunit = g/cm3
  Dvalue = 0.00183094
  Group = -> [N_element030,O_element070]
  conduct = 2
  density = 1
  expand = 3
  formula = G4_NITROUS_OXIDE
  name = G4_NITROUS_OXIDE
  specific = 4
FEATURE [App::DocumentObjectGroupPython] H_element063  label="H_element : 0.104"  # scripted group (container) (typed FeaturePython)
  n = 0.103509
FEATURE [App::DocumentObjectGroupPython] C_element069  label="C_element : 0.648"  # scripted group (container) (typed FeaturePython)
  n = 0.648416
FEATURE [App::DocumentObjectGroupPython] N_element031  label="N_element : 0.100"  # scripted group (container) (typed FeaturePython)
  n = 0.0995361
FEATURE [App::DocumentObjectGroupPython] O_element071  label="O_element : 0.149"  # scripted group (container) (typed FeaturePython)
  n = 0.148539
FEATURE [App::DocumentObjectGroupPython] G4_NYLON_8062  label="G4_NYLON-8062"  # scripted group (container) (typed FeaturePython)
  Dunit = g/cm3
  Dvalue = 1.08
  Group = -> [H_element063,C_element069,N_element031,O_element071]
  conduct = 2
  density = 1
  expand = 3
  formula = G4_NYLON-8062
  name = G4_NYLON-8062
  specific = 4
FEATURE [App::DocumentObjectGroupPython] C_element070  label="C_element : 035"  # scripted group (container) (typed FeaturePython)
  n = 6
  ref = C_element
FEATURE [App::DocumentObjectGroupPython] H_element064  label="H_element : 11"  # scripted group (container) (typed FeaturePython)
  n = 11
  ref = H_element
FEATURE [App::DocumentObjectGroupPython] N_element032  label="N_element : 014"  # scripted group (container) (typed FeaturePython)
  n = 1
  ref = N_element
FEATURE [App::DocumentObjectGroupPython] O_element072  label="O_element : 036"  # scripted group (container) (typed FeaturePython)
  n = 1
  ref = O_element
FEATURE [App::DocumentObjectGroupPython] G4_NYLON_6_6  label="G4_NYLON-6-6"  # scripted group (container) (typed FeaturePython)
  Dunit = g/cm3
  Dvalue = 1.14
  Group = -> [C_element070,H_element064,N_element032,O_element072]
  conduct = 2
  density = 1
  expand = 3
  formula = G4_NYLON-6-6
  name = G4_NYLON-6-6
  specific = 4
FEATURE [App::DocumentObjectGroupPython] H_element065  label="H_element : 0.139"  # scripted group (container) (typed FeaturePython)
  n = 0.107062
FEATURE [App::DocumentObjectGroupPython] C_element071  label="C_element : 0.680"  # scripted group (container) (typed FeaturePython)
  n = 0.680449
FEATURE [App::DocumentObjectGroupPython] N_element033  label="N_element : 0.099"  # scripted group (container) (typed FeaturePython)
  n = 0.099189
FEATURE [App::DocumentObjectGroupPython] O_element073  label="O_element : 0.113"  # scripted group (container) (typed FeaturePython)
  n = 0.1133
FEATURE [App::DocumentObjectGroupPython] G4_NYLON_6_10  label="G4_NYLON-6-10"  # scripted group (container) (typed FeaturePython)
  Dunit = g/cm3
  Dvalue = 1.14
  Group = -> [H_element065,C_element071,N_element033,O_element073]
  conduct = 2
  density = 1
  expand = 3
  formula = G4_NYLON-6-10
  name = G4_NYLON-6-10
  specific = 4
FEATURE [App::DocumentObjectGroupPython] H_element066  label="H_element : 0.140"  # scripted group (container) (typed FeaturePython)
  n = 0.115476
FEATURE [App::DocumentObjectGroupPython] C_element072  label="C_element : 0.721"  # scripted group (container) (typed FeaturePython)
  n = 0.720818
FEATURE [App::DocumentObjectGroupPython] N_element034  label="N_element : 0.076"  # scripted group (container) (typed FeaturePython)
  n = 0.0764169
FEATURE [App::DocumentObjectGroupPython] O_element074  label="O_element : 0.087"  # scripted group (container) (typed FeaturePython)
  n = 0.0872889
FEATURE [App::DocumentObjectGroupPython] G4_NYLON_11_RILSAN  label="G4_NYLON-11_RILSAN"  # scripted group (container) (typed FeaturePython)
  Dunit = g/cm3
  Dvalue = 1.425
  Group = -> [H_element066,C_element072,N_element034,O_element074]
  conduct = 2
  density = 1
  expand = 3
  formula = G4_NYLON-11_RILSAN
  name = G4_NYLON-11_RILSAN
  specific = 4
FEATURE [App::DocumentObjectGroupPython] C_element073  label="C_element : 8"  # scripted group (container) (typed FeaturePython)
  n = 8
  ref = C_element
FEATURE [App::DocumentObjectGroupPython] H_element067  label="H_element : 18"  # scripted group (container) (typed FeaturePython)
  n = 18
  ref = H_element
FEATURE [App::DocumentObjectGroupPython] G4_OCTANE  # scripted group (container) (typed FeaturePython)
  Dunit = g/cm3
  Dvalue = 0.7026
  Group = -> [C_element073,H_element067]
  conduct = 2
  density = 1
  expand = 3
  formula = G4_OCTANE
  name = G4_OCTANE
  specific = 4
FEATURE [App::DocumentObjectGroupPython] C_element074  label="C_element : 25"  # scripted group (container) (typed FeaturePython)
  n = 25
  ref = C_element
FEATURE [App::DocumentObjectGroupPython] H_element068  label="H_element : 52"  # scripted group (container) (typed FeaturePython)
  n = 52
  ref = H_element
FEATURE [App::DocumentObjectGroupPython] G4_PARAFFIN  # scripted group (container) (typed FeaturePython)
  Dunit = g/cm3
  Dvalue = 0.93
  Group = -> [C_element074,H_element068]
  conduct = 2
  density = 1
  expand = 3
  formula = G4_PARAFFIN
  name = G4_PARAFFIN
  specific = 4
FEATURE [App::DocumentObjectGroupPython] C_element075  label="C_element : 036"  # scripted group (container) (typed FeaturePython)
  n = 5
  ref = C_element
FEATURE [App::DocumentObjectGroupPython] H_element069  label="H_element : 032"  # scripted group (container) (typed FeaturePython)
  n = 12
  ref = H_element
FEATURE [App::DocumentObjectGroupPython] G4_N_PENTANE  label="G4_N-PENTANE"  # scripted group (container) (typed FeaturePython)
  Dunit = g/cm3
  Dvalue = 0.6262
  Group = -> [C_element075,H_element069]
  conduct = 2
  density = 1
  expand = 3
  formula = G4_N-PENTANE
  name = G4_N-PENTANE
  specific = 4
FEATURE [App::DocumentObjectGroupPython] H_element070  label="H_element : 0.014"  # scripted group (container) (typed FeaturePython)
  n = 0.0141
FEATURE [App::DocumentObjectGroupPython] C_element076  label="C_element : 0.072"  # scripted group (container) (typed FeaturePython)
  n = 0.072261
FEATURE [App::DocumentObjectGroupPython] N_element035  label="N_element : 0.019"  # scripted group (container) (typed FeaturePython)
  n = 0.01932
FEATURE [App::DocumentObjectGroupPython] O_element075  label="O_element : 0.066"  # scripted group (container) (typed FeaturePython)
  n = 0.066101
FEATURE [App::DocumentObjectGroupPython] S_element019  label="S_element : 0.020"  # scripted group (container) (typed FeaturePython)
  n = 0.00189
FEATURE [App::DocumentObjectGroupPython] Br_element004  label="Br_element : 0.349"  # scripted group (container) (typed FeaturePython)
  n = 0.349103
FEATURE [App::DocumentObjectGroupPython] Ag_element001  label="Ag_element : 0.474"  # scripted group (container) (typed FeaturePython)
  n = 0.474105
FEATURE [App::DocumentObjectGroupPython] I_element005  label="I_element : 0.003"  # scripted group (container) (typed FeaturePython)
  n = 0.00312
FEATURE [App::DocumentObjectGroupPython] G4_PHOTO_EMULSION  # scripted group (container) (typed FeaturePython)
  Dunit = g/cm3
  Dvalue = 3.815
  Group = -> [H_element070,C_element076,N_element035,O_element075,S_element019,Br_element004,Ag_element001,I_element005]
  conduct = 2
  density = 1
  expand = 3
  formula = G4_PHOTO_EMULSION
  name = G4_PHOTO_EMULSION
  specific = 4
FEATURE [App::DocumentObjectGroupPython] C_element077  label="C_element : 9"  # scripted group (container) (typed FeaturePython)
  n = 9
  ref = C_element
FEATURE [App::DocumentObjectGroupPython] H_element071  label="H_element : 033"  # scripted group (container) (typed FeaturePython)
  n = 10
  ref = H_element
FEATURE [App::DocumentObjectGroupPython] G4_PLASTIC_SC_VINYLTOLUENE  # scripted group (container) (typed FeaturePython)
  Dunit = g/cm3
  Dvalue = 1.032
  Group = -> [C_element077,H_element071]
  conduct = 2
  density = 1
  expand = 3
  formula = G4_PLASTIC_SC_VINYLTOLUENE
  name = G4_PLASTIC_SC_VINYLTOLUENE
  specific = 4
FEATURE [App::DocumentObjectGroupPython] Pu_element001  label="Pu_element : 1"  # scripted group (container) (typed FeaturePython)
  n = 1
  ref = Pu_element
FEATURE [App::DocumentObjectGroupPython] O_element076  label="O_element : 037"  # scripted group (container) (typed FeaturePython)
  n = 2
  ref = O_element
FEATURE [App::DocumentObjectGroupPython] G4_PLUTONIUM_DIOXIDE  # scripted group (container) (typed FeaturePython)
  Dunit = g/cm3
  Dvalue = 11.46
  Group = -> [Pu_element001,O_element076]
  conduct = 2
  density = 1
  expand = 3
  formula = G4_PLUTONIUM_DIOXIDE
  name = G4_PLUTONIUM_DIOXIDE
  specific = 4
FEATURE [App::DocumentObjectGroupPython] C_element078  label="C_element : 037"  # scripted group (container) (typed FeaturePython)
  n = 3
  ref = C_element
FEATURE [App::DocumentObjectGroupPython] H_element072  label="H_element : 034"  # scripted group (container) (typed FeaturePython)
  n = 3
  ref = H_element
FEATURE [App::DocumentObjectGroupPython] N_element036  label="N_element : 015"  # scripted group (container) (typed FeaturePython)
  n = 1
  ref = N_element
FEATURE [App::DocumentObjectGroupPython] G4_POLYACRYLONITRILE  # scripted group (container) (typed FeaturePython)
  Dunit = g/cm3
  Dvalue = 1.17
  Group = -> [C_element078,H_element072,N_element036]
  conduct = 2
  density = 1
  expand = 3
  formula = G4_POLYACRYLONITRILE
  name = G4_POLYACRYLONITRILE
  specific = 4
FEATURE [App::DocumentObjectGroupPython] C_element079  label="C_element : 16"  # scripted group (container) (typed FeaturePython)
  n = 16
  ref = C_element
FEATURE [App::DocumentObjectGroupPython] H_element073  label="H_element : 035"  # scripted group (container) (typed FeaturePython)
  n = 14
  ref = H_element
FEATURE [App::DocumentObjectGroupPython] O_element077  label="O_element : 038"  # scripted group (container) (typed FeaturePython)
  n = 3
  ref = O_element
FEATURE [App::DocumentObjectGroupPython] G4_POLYCARBONATE  # scripted group (container) (typed FeaturePython)
  Dunit = g/cm3
  Dvalue = 1.2
  Group = -> [C_element079,H_element073,O_element077]
  conduct = 2
  density = 1
  expand = 3
  formula = G4_POLYCARBONATE
  name = G4_POLYCARBONATE
  specific = 4
FEATURE [App::DocumentObjectGroupPython] C_element080  label="C_element : 038"  # scripted group (container) (typed FeaturePython)
  n = 8
  ref = C_element
FEATURE [App::DocumentObjectGroupPython] H_element074  label="H_element : 036"  # scripted group (container) (typed FeaturePython)
  n = 7
  ref = H_element
FEATURE [App::DocumentObjectGroupPython] Cl_element017  label="Cl_element : 007"  # scripted group (container) (typed FeaturePython)
  n = 1
  ref = Cl_element
FEATURE [App::DocumentObjectGroupPython] G4_POLYCHLOROSTYRENE  # scripted group (container) (typed FeaturePython)
  Dunit = g/cm3
  Dvalue = 1.3
  Group = -> [C_element080,H_element074,Cl_element017]
  conduct = 2
  density = 1
  expand = 3
  formula = G4_POLYCHLOROSTYRENE
  name = G4_POLYCHLOROSTYRENE
  specific = 4
FEATURE [App::DocumentObjectGroupPython] C_element081  label="C_element : 039"  # scripted group (container) (typed FeaturePython)
  n = 1
  ref = C_element
FEATURE [App::DocumentObjectGroupPython] H_element075  label="H_element : 037"  # scripted group (container) (typed FeaturePython)
  n = 2
  ref = H_element
FEATURE [App::DocumentObjectGroupPython] G4_POLYETHYLENE  # scripted group (container) (typed FeaturePython)
  Dunit = g/cm3
  Dvalue = 0.94
  Group = -> [C_element081,H_element075]
  conduct = 2
  density = 1
  expand = 3
  formula = G4_POLYETHYLENE
  name = G4_POLYETHYLENE
  specific = 4
FEATURE [App::DocumentObjectGroupPython] C_element082  label="C_element : 040"  # scripted group (container) (typed FeaturePython)
  n = 10
  ref = C_element
FEATURE [App::DocumentObjectGroupPython] H_element076  label="H_element : 038"  # scripted group (container) (typed FeaturePython)
  n = 8
  ref = H_element
FEATURE [App::DocumentObjectGroupPython] O_element078  label="O_element : 039"  # scripted group (container) (typed FeaturePython)
  n = 4
  ref = O_element
FEATURE [App::DocumentObjectGroupPython] G4_MYLAR  # scripted group (container) (typed FeaturePython)
  Dunit = g/cm3
  Dvalue = 1.4
  Group = -> [C_element082,H_element076,O_element078]
  conduct = 2
  density = 1
  expand = 3
  formula = G4_MYLAR
  name = G4_MYLAR
  specific = 4
FEATURE [App::DocumentObjectGroupPython] C_element083  label="C_element : 041"  # scripted group (container) (typed FeaturePython)
  n = 5
  ref = C_element
FEATURE [App::DocumentObjectGroupPython] H_element077  label="H_element : 039"  # scripted group (container) (typed FeaturePython)
  n = 8
  ref = H_element
FEATURE [App::DocumentObjectGroupPython] O_element079  label="O_element : 040"  # scripted group (container) (typed FeaturePython)
  n = 2
  ref = O_element
FEATURE [App::DocumentObjectGroupPython] G4_PLEXIGLASS  # scripted group (container) (typed FeaturePython)
  Dunit = g/cm3
  Dvalue = 1.19
  Group = -> [C_element083,H_element077,O_element079]
  conduct = 2
  density = 1
  expand = 3
  formula = G4_PLEXIGLASS
  name = G4_PLEXIGLASS
  specific = 4
FEATURE [App::DocumentObjectGroupPython] C_element084  label="C_element : 042"  # scripted group (container) (typed FeaturePython)
  n = 1
  ref = C_element
FEATURE [App::DocumentObjectGroupPython] H_element078  label="H_element : 040"  # scripted group (container) (typed FeaturePython)
  n = 2
  ref = H_element
FEATURE [App::DocumentObjectGroupPython] O_element080  label="O_element : 041"  # scripted group (container) (typed FeaturePython)
  n = 1
  ref = O_element
FEATURE [App::DocumentObjectGroupPython] G4_POLYOXYMETHYLENE  # scripted group (container) (typed FeaturePython)
  Dunit = g/cm3
  Dvalue = 1.425
  Group = -> [C_element084,H_element078,O_element080]
  conduct = 2
  density = 1
  expand = 3
  formula = G4_POLYOXYMETHYLENE
  name = G4_POLYOXYMETHYLENE
  specific = 4
FEATURE [App::DocumentObjectGroupPython] C_element085  label="C_element : 043"  # scripted group (container) (typed FeaturePython)
  n = 2
  ref = C_element
FEATURE [App::DocumentObjectGroupPython] H_element079  label="H_element : 041"  # scripted group (container) (typed FeaturePython)
  n = 4
  ref = H_element
FEATURE [App::DocumentObjectGroupPython] G4_POLYPROPYLENE  # scripted group (container) (typed FeaturePython)
  Dunit = g/cm3
  Dvalue = 0.9
  Group = -> [C_element085,H_element079]
  conduct = 2
  density = 1
  expand = 3
  formula = G4_POLYPROPYLENE
  name = G4_POLYPROPYLENE
  specific = 4
FEATURE [App::DocumentObjectGroupPython] C_element086  label="C_element : 044"  # scripted group (container) (typed FeaturePython)
  n = 8
  ref = C_element
FEATURE [App::DocumentObjectGroupPython] H_element080  label="H_element : 042"  # scripted group (container) (typed FeaturePython)
  n = 8
  ref = H_element
FEATURE [App::DocumentObjectGroupPython] G4_POLYSTYRENE  # scripted group (container) (typed FeaturePython)
  Dunit = g/cm3
  Dvalue = 1.06
  Group = -> [C_element086,H_element080]
  conduct = 2
  density = 1
  expand = 3
  formula = G4_POLYSTYRENE
  name = G4_POLYSTYRENE
  specific = 4
FEATURE [App::DocumentObjectGroupPython] C_element087  label="C_element : 045"  # scripted group (container) (typed FeaturePython)
  n = 2
  ref = C_element
FEATURE [App::DocumentObjectGroupPython] F_element014  label="F_element : 4"  # scripted group (container) (typed FeaturePython)
  n = 4
  ref = F_element
FEATURE [App::DocumentObjectGroupPython] G4_TEFLON  # scripted group (container) (typed FeaturePython)
  Dunit = g/cm3
  Dvalue = 2.2
  Group = -> [C_element087,F_element014]
  conduct = 2
  density = 1
  expand = 3
  formula = G4_TEFLON
  name = G4_TEFLON
  specific = 4
FEATURE [App::DocumentObjectGroupPython] C_element088  label="C_element : 046"  # scripted group (container) (typed FeaturePython)
  n = 2
  ref = C_element
FEATURE [App::DocumentObjectGroupPython] F_element015  label="F_element : 006"  # scripted group (container) (typed FeaturePython)
  n = 3
  ref = F_element
FEATURE [App::DocumentObjectGroupPython] Cl_element018  label="Cl_element : 008"  # scripted group (container) (typed FeaturePython)
  n = 1
  ref = Cl_element
FEATURE [App::DocumentObjectGroupPython] G4_POLYTRIFLUOROCHLOROETHYLENE  # scripted group (container) (typed FeaturePython)
  Dunit = g/cm3
  Dvalue = 2.1
  Group = -> [C_element088,F_element015,Cl_element018]
  conduct = 2
  density = 1
  expand = 3
  formula = G4_POLYTRIFLUOROCHLOROETHYLENE
  name = G4_POLYTRIFLUOROCHLOROETHYLENE
  specific = 4
FEATURE [App::DocumentObjectGroupPython] C_element089  label="C_element : 047"  # scripted group (container) (typed FeaturePython)
  n = 4
  ref = C_element
FEATURE [App::DocumentObjectGroupPython] H_element081  label="H_element : 043"  # scripted group (container) (typed FeaturePython)
  n = 6
  ref = H_element
FEATURE [App::DocumentObjectGroupPython] O_element081  label="O_element : 042"  # scripted group (container) (typed FeaturePython)
  n = 2
  ref = O_element
FEATURE [App::DocumentObjectGroupPython] G4_POLYVINYL_ACETATE  # scripted group (container) (typed FeaturePython)
  Dunit = g/cm3
  Dvalue = 1.19
  Group = -> [C_element089,H_element081,O_element081]
  conduct = 2
  density = 1
  expand = 3
  formula = G4_POLYVINYL_ACETATE
  name = G4_POLYVINYL_ACETATE
  specific = 4
FEATURE [App::DocumentObjectGroupPython] C_element090  label="C_element : 048"  # scripted group (container) (typed FeaturePython)
  n = 2
  ref = C_element
FEATURE [App::DocumentObjectGroupPython] H_element082  label="H_element : 044"  # scripted group (container) (typed FeaturePython)
  n = 4
  ref = H_element
FEATURE [App::DocumentObjectGroupPython] O_element082  label="O_element : 043"  # scripted group (container) (typed FeaturePython)
  n = 1
  ref = O_element
FEATURE [App::DocumentObjectGroupPython] G4_POLYVINYL_ALCOHOL  # scripted group (container) (typed FeaturePython)
  Dunit = g/cm3
  Dvalue = 1.3
  Group = -> [C_element090,H_element082,O_element082]
  conduct = 2
  density = 1
  expand = 3
  formula = G4_POLYVINYL_ALCOHOL
  name = G4_POLYVINYL_ALCOHOL
  specific = 4
FEATURE [App::DocumentObjectGroupPython] C_element091  label="C_element : 049"  # scripted group (container) (typed FeaturePython)
  n = 8
  ref = C_element
FEATURE [App::DocumentObjectGroupPython] H_element083  label="H_element : 045"  # scripted group (container) (typed FeaturePython)
  n = 14
  ref = H_element
FEATURE [App::DocumentObjectGroupPython] O_element083  label="O_element : 044"  # scripted group (container) (typed FeaturePython)
  n = 2
  ref = O_element
FEATURE [App::DocumentObjectGroupPython] G4_POLYVINYL_BUTYRAL  # scripted group (container) (typed FeaturePython)
  Dunit = g/cm3
  Dvalue = 1.12
  Group = -> [C_element091,H_element083,O_element083]
  conduct = 2
  density = 1
  expand = 3
  formula = G4_POLYVINYL_BUTYRAL
  name = G4_POLYVINYL_BUTYRAL
  specific = 4
FEATURE [App::DocumentObjectGroupPython] C_element092  label="C_element : 050"  # scripted group (container) (typed FeaturePython)
  n = 2
  ref = C_element
FEATURE [App::DocumentObjectGroupPython] H_element084  label="H_element : 046"  # scripted group (container) (typed FeaturePython)
  n = 3
  ref = H_element
FEATURE [App::DocumentObjectGroupPython] Cl_element019  label="Cl_element : 009"  # scripted group (container) (typed FeaturePython)
  n = 1
  ref = Cl_element
FEATURE [App::DocumentObjectGroupPython] G4_POLYVINYL_CHLORIDE  # scripted group (container) (typed FeaturePython)
  Dunit = g/cm3
  Dvalue = 1.3
  Group = -> [C_element092,H_element084,Cl_element019]
  conduct = 2
  density = 1
  expand = 3
  formula = G4_POLYVINYL_CHLORIDE
  name = G4_POLYVINYL_CHLORIDE
  specific = 4
FEATURE [App::DocumentObjectGroupPython] C_element093  label="C_element : 051"  # scripted group (container) (typed FeaturePython)
  n = 2
  ref = C_element
FEATURE [App::DocumentObjectGroupPython] H_element085  label="H_element : 047"  # scripted group (container) (typed FeaturePython)
  n = 2
  ref = H_element
FEATURE [App::DocumentObjectGroupPython] Cl_element020  label="Cl_element : 010"  # scripted group (container) (typed FeaturePython)
  n = 2
  ref = Cl_element
FEATURE [App::DocumentObjectGroupPython] G4_POLYVINYLIDENE_CHLORIDE  # scripted group (container) (typed FeaturePython)
  Dunit = g/cm3
  Dvalue = 1.7
  Group = -> [C_element093,H_element085,Cl_element020]
  conduct = 2
  density = 1
  expand = 3
  formula = G4_POLYVINYLIDENE_CHLORIDE
  name = G4_POLYVINYLIDENE_CHLORIDE
  specific = 4
FEATURE [App::DocumentObjectGroupPython] C_element094  label="C_element : 052"  # scripted group (container) (typed FeaturePython)
  n = 2
  ref = C_element
FEATURE [App::DocumentObjectGroupPython] H_element086  label="H_element : 048"  # scripted group (container) (typed FeaturePython)
  n = 2
  ref = H_element
FEATURE [App::DocumentObjectGroupPython] F_element016  label="F_element : 007"  # scripted group (container) (typed FeaturePython)
  n = 2
  ref = F_element
FEATURE [App::DocumentObjectGroupPython] G4_POLYVINYLIDENE_FLUORIDE  # scripted group (container) (typed FeaturePython)
  Dunit = g/cm3
  Dvalue = 1.76
  Group = -> [C_element094,H_element086,F_element016]
  conduct = 2
  density = 1
  expand = 3
  formula = G4_POLYVINYLIDENE_FLUORIDE
  name = G4_POLYVINYLIDENE_FLUORIDE
  specific = 4
FEATURE [App::DocumentObjectGroupPython] C_element095  label="C_element : 053"  # scripted group (container) (typed FeaturePython)
  n = 6
  ref = C_element
FEATURE [App::DocumentObjectGroupPython] H_element087  label="H_element : 9"  # scripted group (container) (typed FeaturePython)
  n = 9
  ref = H_element
FEATURE [App::DocumentObjectGroupPython] N_element037  label="N_element : 016"  # scripted group (container) (typed FeaturePython)
  n = 1
  ref = N_element
FEATURE [App::DocumentObjectGroupPython] O_element084  label="O_element : 045"  # scripted group (container) (typed FeaturePython)
  n = 1
  ref = O_element
FEATURE [App::DocumentObjectGroupPython] G4_POLYVINYL_PYRROLIDONE  # scripted group (container) (typed FeaturePython)
  Dunit = g/cm3
  Dvalue = 1.25
  Group = -> [C_element095,H_element087,N_element037,O_element084]
  conduct = 2
  density = 1
  expand = 3
  formula = G4_POLYVINYL_PYRROLIDONE
  name = G4_POLYVINYL_PYRROLIDONE
  specific = 4
FEATURE [App::DocumentObjectGroupPython] K_element008  label="K_element : 1"  # scripted group (container) (typed FeaturePython)
  n = 1
  ref = K_element
FEATURE [App::DocumentObjectGroupPython] I_element006  label="I_element : 003"  # scripted group (container) (typed FeaturePython)
  n = 1
  ref = I_element
FEATURE [App::DocumentObjectGroupPython] G4_POTASSIUM_IODIDE  # scripted group (container) (typed FeaturePython)
  Dunit = g/cm3
  Dvalue = 3.13
  Group = -> [K_element008,I_element006]
  conduct = 2
  density = 1
  expand = 3
  formula = G4_POTASSIUM_IODIDE
  name = G4_POTASSIUM_IODIDE
  specific = 4
FEATURE [App::DocumentObjectGroupPython] K_element009  label="K_element : 2"  # scripted group (container) (typed FeaturePython)
  n = 2
  ref = K_element
FEATURE [App::DocumentObjectGroupPython] O_element085  label="O_element : 046"  # scripted group (container) (typed FeaturePython)
  n = 1
  ref = O_element
FEATURE [App::DocumentObjectGroupPython] G4_POTASSIUM_OXIDE  # scripted group (container) (typed FeaturePython)
  Dunit = g/cm3
  Dvalue = 2.32
  Group = -> [K_element009,O_element085]
  conduct = 2
  density = 1
  expand = 3
  formula = G4_POTASSIUM_OXIDE
  name = G4_POTASSIUM_OXIDE
  specific = 4
FEATURE [App::DocumentObjectGroupPython] C_element096  label="C_element : 054"  # scripted group (container) (typed FeaturePython)
  n = 3
  ref = C_element
FEATURE [App::DocumentObjectGroupPython] H_element088  label="H_element : 049"  # scripted group (container) (typed FeaturePython)
  n = 8
  ref = H_element
FEATURE [App::DocumentObjectGroupPython] G4_PROPANE  # scripted group (container) (typed FeaturePython)
  Dunit = g/cm3
  Dvalue = 0.00187939
  Group = -> [C_element096,H_element088]
  conduct = 2
  density = 1
  expand = 3
  formula = G4_PROPANE
  name = G4_PROPANE
  specific = 4
FEATURE [App::DocumentObjectGroupPython] C_element097  label="C_element : 055"  # scripted group (container) (typed FeaturePython)
  n = 3
  ref = C_element
FEATURE [App::DocumentObjectGroupPython] H_element089  label="H_element : 050"  # scripted group (container) (typed FeaturePython)
  n = 8
  ref = H_element
FEATURE [App::DocumentObjectGroupPython] G4_lPROPANE  # scripted group (container) (typed FeaturePython)
  Dunit = g/cm3
  Dvalue = 0.43
  Group = -> [C_element097,H_element089]
  conduct = 2
  density = 1
  expand = 3
  formula = G4_lPROPANE
  name = G4_lPROPANE
  specific = 4
FEATURE [App::DocumentObjectGroupPython] C_element098  label="C_element : 056"  # scripted group (container) (typed FeaturePython)
  n = 3
  ref = C_element
FEATURE [App::DocumentObjectGroupPython] H_element090  label="H_element : 051"  # scripted group (container) (typed FeaturePython)
  n = 8
  ref = H_element
FEATURE [App::DocumentObjectGroupPython] O_element086  label="O_element : 047"  # scripted group (container) (typed FeaturePython)
  n = 1
  ref = O_element
FEATURE [App::DocumentObjectGroupPython] G4_N_PROPYL_ALCOHOL  label="G4_N-PROPYL_ALCOHOL"  # scripted group (container) (typed FeaturePython)
  Dunit = g/cm3
  Dvalue = 0.8035
  Group = -> [C_element098,H_element090,O_element086]
  conduct = 2
  density = 1
  expand = 3
  formula = G4_N-PROPYL_ALCOHOL
  name = G4_N-PROPYL_ALCOHOL
  specific = 4
FEATURE [App::DocumentObjectGroupPython] C_element099  label="C_element : 057"  # scripted group (container) (typed FeaturePython)
  n = 5
  ref = C_element
FEATURE [App::DocumentObjectGroupPython] H_element091  label="H_element : 052"  # scripted group (container) (typed FeaturePython)
  n = 5
  ref = H_element
FEATURE [App::DocumentObjectGroupPython] N_element038  label="N_element : 017"  # scripted group (container) (typed FeaturePython)
  n = 1
  ref = N_element
FEATURE [App::DocumentObjectGroupPython] G4_PYRIDINE  # scripted group (container) (typed FeaturePython)
  Dunit = g/cm3
  Dvalue = 0.9819
  Group = -> [C_element099,H_element091,N_element038]
  conduct = 2
  density = 1
  expand = 3
  formula = G4_PYRIDINE
  name = G4_PYRIDINE
  specific = 4
FEATURE [App::DocumentObjectGroupPython] H_element092  label="H_element : 0.144"  # scripted group (container) (typed FeaturePython)
  n = 0.143711
FEATURE [App::DocumentObjectGroupPython] C_element100  label="C_element : 0.856"  # scripted group (container) (typed FeaturePython)
  n = 0.856289
FEATURE [App::DocumentObjectGroupPython] G4_RUBBER_BUTYL  # scripted group (container) (typed FeaturePython)
  Dunit = g/cm3
  Dvalue = 0.92
  Group = -> [H_element092,C_element100]
  conduct = 2
  density = 1
  expand = 3
  formula = G4_RUBBER_BUTYL
  name = G4_RUBBER_BUTYL
  specific = 4
FEATURE [App::DocumentObjectGroupPython] H_element093  label="H_element : 0.118"  # scripted group (container) (typed FeaturePython)
  n = 0.118371
FEATURE [App::DocumentObjectGroupPython] C_element101  label="C_element : 0.882"  # scripted group (container) (typed FeaturePython)
  n = 0.881629
FEATURE [App::DocumentObjectGroupPython] G4_RUBBER_NATURAL  # scripted group (container) (typed FeaturePython)
  Dunit = g/cm3
  Dvalue = 0.92
  Group = -> [H_element093,C_element101]
  conduct = 2
  density = 1
  expand = 3
  formula = G4_RUBBER_NATURAL
  name = G4_RUBBER_NATURAL
  specific = 4
FEATURE [App::DocumentObjectGroupPython] H_element094  label="H_element : 0.145"  # scripted group (container) (typed FeaturePython)
  n = 0.05692
FEATURE [App::DocumentObjectGroupPython] C_element102  label="C_element : 0.543"  # scripted group (container) (typed FeaturePython)
  n = 0.542646
FEATURE [App::DocumentObjectGroupPython] Cl_element021  label="Cl_element : 0.400"  # scripted group (container) (typed FeaturePython)
  n = 0.400434
FEATURE [App::DocumentObjectGroupPython] G4_RUBBER_NEOPRENE  # scripted group (container) (typed FeaturePython)
  Dunit = g/cm3
  Dvalue = 1.23
  Group = -> [H_element094,C_element102,Cl_element021]
  conduct = 2
  density = 1
  expand = 3
  formula = G4_RUBBER_NEOPRENE
  name = G4_RUBBER_NEOPRENE
  specific = 4
FEATURE [App::DocumentObjectGroupPython] Si_element006  label="Si_element : 1"  # scripted group (container) (typed FeaturePython)
  n = 1
  ref = Si_element
FEATURE [App::DocumentObjectGroupPython] O_element087  label="O_element : 048"  # scripted group (container) (typed FeaturePython)
  n = 2
  ref = O_element
FEATURE [App::DocumentObjectGroupPython] G4_SILICON_DIOXIDE  # scripted group (container) (typed FeaturePython)
  Dunit = g/cm3
  Dvalue = 2.32
  Group = -> [Si_element006,O_element087]
  conduct = 2
  density = 1
  expand = 3
  formula = G4_SILICON_DIOXIDE
  name = G4_SILICON_DIOXIDE
  specific = 4
FEATURE [App::DocumentObjectGroupPython] Ag_element002  label="Ag_element : 1"  # scripted group (container) (typed FeaturePython)
  n = 1
  ref = Ag_element
FEATURE [App::DocumentObjectGroupPython] Br_element005  label="Br_element : 003"  # scripted group (container) (typed FeaturePython)
  n = 1
  ref = Br_element
FEATURE [App::DocumentObjectGroupPython] G4_SILVER_BROMIDE  # scripted group (container) (typed FeaturePython)
  Dunit = g/cm3
  Dvalue = 6.473
  Group = -> [Ag_element002,Br_element005]
  conduct = 2
  density = 1
  expand = 3
  formula = G4_SILVER_BROMIDE
  name = G4_SILVER_BROMIDE
  specific = 4
FEATURE [App::DocumentObjectGroupPython] Ag_element003  label="Ag_element : 002"  # scripted group (container) (typed FeaturePython)
  n = 1
  ref = Ag_element
FEATURE [App::DocumentObjectGroupPython] Cl_element022  label="Cl_element : 011"  # scripted group (container) (typed FeaturePython)
  n = 1
  ref = Cl_element
FEATURE [App::DocumentObjectGroupPython] G4_SILVER_CHLORIDE  # scripted group (container) (typed FeaturePython)
  Dunit = g/cm3
  Dvalue = 5.56
  Group = -> [Ag_element003,Cl_element022]
  conduct = 2
  density = 1
  expand = 3
  formula = G4_SILVER_CHLORIDE
  name = G4_SILVER_CHLORIDE
  specific = 4
FEATURE [App::DocumentObjectGroupPython] Br_element006  label="Br_element : 0.423"  # scripted group (container) (typed FeaturePython)
  n = 0.422895
FEATURE [App::DocumentObjectGroupPython] Ag_element004  label="Ag_element : 0.574"  # scripted group (container) (typed FeaturePython)
  n = 0.573748
FEATURE [App::DocumentObjectGroupPython] I_element007  label="I_element : 0.649"  # scripted group (container) (typed FeaturePython)
  n = 0.003357
FEATURE [App::DocumentObjectGroupPython] G4_SILVER_HALIDES  # scripted group (container) (typed FeaturePython)
  Dunit = g/cm3
  Dvalue = 6.47
  Group = -> [Br_element006,Ag_element004,I_element007]
  conduct = 2
  density = 1
  expand = 3
  formula = G4_SILVER_HALIDES
  name = G4_SILVER_HALIDES
  specific = 4
FEATURE [App::DocumentObjectGroupPython] Ag_element005  label="Ag_element : 003"  # scripted group (container) (typed FeaturePython)
  n = 1
  ref = Ag_element
FEATURE [App::DocumentObjectGroupPython] I_element008  label="I_element : 004"  # scripted group (container) (typed FeaturePython)
  n = 1
  ref = I_element
FEATURE [App::DocumentObjectGroupPython] G4_SILVER_IODIDE  # scripted group (container) (typed FeaturePython)
  Dunit = g/cm3
  Dvalue = 6.01
  Group = -> [Ag_element005,I_element008]
  conduct = 2
  density = 1
  expand = 3
  formula = G4_SILVER_IODIDE
  name = G4_SILVER_IODIDE
  specific = 4
FEATURE [App::DocumentObjectGroupPython] H_element095  label="H_element : 0.100"  # scripted group (container) (typed FeaturePython)
  n = 0.1
FEATURE [App::DocumentObjectGroupPython] C_element103  label="C_element : 0.204"  # scripted group (container) (typed FeaturePython)
  n = 0.204
FEATURE [App::DocumentObjectGroupPython] N_element039  label="N_element : 0.759"  # scripted group (container) (typed FeaturePython)
  n = 0.042
FEATURE [App::DocumentObjectGroupPython] O_element088  label="O_element : 0.645"  # scripted group (container) (typed FeaturePython)
  n = 0.645
FEATURE [App::DocumentObjectGroupPython] Na_element013  label="Na_element : 0.100"  # scripted group (container) (typed FeaturePython)
  n = 0.002
FEATURE [App::DocumentObjectGroupPython] P_element009  label="P_element : 0.107"  # scripted group (container) (typed FeaturePython)
  n = 0.001
FEATURE [App::DocumentObjectGroupPython] S_element020  label="S_element : 0.021"  # scripted group (container) (typed FeaturePython)
  n = 0.002
FEATURE [App::DocumentObjectGroupPython] Cl_element023  label="Cl_element : 0.590"  # scripted group (container) (typed FeaturePython)
  n = 0.003
FEATURE [App::DocumentObjectGroupPython] K_element010  label="K_element : 0.001"  # scripted group (container) (typed FeaturePython)
  n = 0.001
FEATURE [App::DocumentObjectGroupPython] G4_SKIN_ICRP  # scripted group (container) (typed FeaturePython)
  Dunit = g/cm3
  Dvalue = 1.09
  Group = -> [H_element095,C_element103,N_element039,O_element088,Na_element013,P_element009,S_element020,Cl_element023,K_element010]
  conduct = 2
  density = 1
  expand = 3
  formula = G4_SKIN_ICRP
  name = G4_SKIN_ICRP
  specific = 4
FEATURE [App::DocumentObjectGroupPython] Na_element014  label="Na_element : 2"  # scripted group (container) (typed FeaturePython)
  n = 2
  ref = Na_element
FEATURE [App::DocumentObjectGroupPython] C_element104  label="C_element : 058"  # scripted group (container) (typed FeaturePython)
  n = 1
  ref = C_element
FEATURE [App::DocumentObjectGroupPython] O_element089  label="O_element : 049"  # scripted group (container) (typed FeaturePython)
  n = 3
  ref = O_element
FEATURE [App::DocumentObjectGroupPython] G4_SODIUM_CARBONATE  # scripted group (container) (typed FeaturePython)
  Dunit = g/cm3
  Dvalue = 2.532
  Group = -> [Na_element014,C_element104,O_element089]
  conduct = 2
  density = 1
  expand = 3
  formula = G4_SODIUM_CARBONATE
  name = G4_SODIUM_CARBONATE
  specific = 4
FEATURE [App::DocumentObjectGroupPython] Na_element015  label="Na_element : 1"  # scripted group (container) (typed FeaturePython)
  n = 1
  ref = Na_element
FEATURE [App::DocumentObjectGroupPython] I_element009  label="I_element : 005"  # scripted group (container) (typed FeaturePython)
  n = 1
  ref = I_element
FEATURE [App::DocumentObjectGroupPython] G4_SODIUM_IODIDE  # scripted group (container) (typed FeaturePython)
  Dunit = g/cm3
  Dvalue = 3.667
  Group = -> [Na_element015,I_element009]
  conduct = 2
  density = 1
  expand = 3
  formula = G4_SODIUM_IODIDE
  name = G4_SODIUM_IODIDE
  specific = 4
FEATURE [App::DocumentObjectGroupPython] Na_element016  label="Na_element : 003"  # scripted group (container) (typed FeaturePython)
  n = 2
  ref = Na_element
FEATURE [App::DocumentObjectGroupPython] O_element090  label="O_element : 050"  # scripted group (container) (typed FeaturePython)
  n = 1
  ref = O_element
FEATURE [App::DocumentObjectGroupPython] G4_SODIUM_MONOXIDE  # scripted group (container) (typed FeaturePython)
  Dunit = g/cm3
  Dvalue = 2.27
  Group = -> [Na_element016,O_element090]
  conduct = 2
  density = 1
  expand = 3
  formula = G4_SODIUM_MONOXIDE
  name = G4_SODIUM_MONOXIDE
  specific = 4
FEATURE [App::DocumentObjectGroupPython] Na_element017  label="Na_element : 004"  # scripted group (container) (typed FeaturePython)
  n = 1
  ref = Na_element
FEATURE [App::DocumentObjectGroupPython] N_element040  label="N_element : 018"  # scripted group (container) (typed FeaturePython)
  n = 1
  ref = N_element
FEATURE [App::DocumentObjectGroupPython] O_element091  label="O_element : 051"  # scripted group (container) (typed FeaturePython)
  n = 3
  ref = O_element
FEATURE [App::DocumentObjectGroupPython] G4_SODIUM_NITRATE  # scripted group (container) (typed FeaturePython)
  Dunit = g/cm3
  Dvalue = 2.261
  Group = -> [Na_element017,N_element040,O_element091]
  conduct = 2
  density = 1
  expand = 3
  formula = G4_SODIUM_NITRATE
  name = G4_SODIUM_NITRATE
  specific = 4
FEATURE [App::DocumentObjectGroupPython] C_element105  label="C_element : 059"  # scripted group (container) (typed FeaturePython)
  n = 14
  ref = C_element
FEATURE [App::DocumentObjectGroupPython] H_element096  label="H_element : 053"  # scripted group (container) (typed FeaturePython)
  n = 12
  ref = H_element
FEATURE [App::DocumentObjectGroupPython] G4_STILBENE  # scripted group (container) (typed FeaturePython)
  Dunit = g/cm3
  Dvalue = 0.9707
  Group = -> [C_element105,H_element096]
  conduct = 2
  density = 1
  expand = 3
  formula = G4_STILBENE
  name = G4_STILBENE
  specific = 4
FEATURE [App::DocumentObjectGroupPython] C_element106  label="C_element : 12"  # scripted group (container) (typed FeaturePython)
  n = 12
  ref = C_element
FEATURE [App::DocumentObjectGroupPython] H_element097  label="H_element : 22"  # scripted group (container) (typed FeaturePython)
  n = 22
  ref = H_element
FEATURE [App::DocumentObjectGroupPython] O_element092  label="O_element : 11"  # scripted group (container) (typed FeaturePython)
  n = 11
  ref = O_element
FEATURE [App::DocumentObjectGroupPython] G4_SUCROSE  # scripted group (container) (typed FeaturePython)
  Dunit = g/cm3
  Dvalue = 1.5805
  Group = -> [C_element106,H_element097,O_element092]
  conduct = 2
  density = 1
  expand = 3
  formula = G4_SUCROSE
  name = G4_SUCROSE
  specific = 4
FEATURE [App::DocumentObjectGroupPython] C_element107  label="C_element : 18"  # scripted group (container) (typed FeaturePython)
  n = 18
  ref = C_element
FEATURE [App::DocumentObjectGroupPython] H_element098  label="H_element : 054"  # scripted group (container) (typed FeaturePython)
  n = 14
  ref = H_element
FEATURE [App::DocumentObjectGroupPython] G4_TERPHENYL  # scripted group (container) (typed FeaturePython)
  Dunit = g/cm3
  Dvalue = 1.24
  Group = -> [C_element107,H_element098]
  conduct = 2
  density = 1
  expand = 3
  formula = G4_TERPHENYL
  name = G4_TERPHENYL
  specific = 4
FEATURE [App::DocumentObjectGroupPython] H_element099  label="H_element : 0.146"  # scripted group (container) (typed FeaturePython)
  n = 0.106
FEATURE [App::DocumentObjectGroupPython] C_element108  label="C_element : 0.883"  # scripted group (container) (typed FeaturePython)
  n = 0.099
FEATURE [App::DocumentObjectGroupPython] N_element041  label="N_element : 0.020"  # scripted group (container) (typed FeaturePython)
  n = 0.02
FEATURE [App::DocumentObjectGroupPython] O_element093  label="O_element : 0.766"  # scripted group (container) (typed FeaturePython)
  n = 0.766
FEATURE [App::DocumentObjectGroupPython] Na_element018  label="Na_element : 0.101"  # scripted group (container) (typed FeaturePython)
  n = 0.002
FEATURE [App::DocumentObjectGroupPython] P_element010  label="P_element : 0.108"  # scripted group (container) (typed FeaturePython)
  n = 0.001
FEATURE [App::DocumentObjectGroupPython] S_element021  label="S_element : 0.022"  # scripted group (container) (typed FeaturePython)
  n = 0.002
FEATURE [App::DocumentObjectGroupPython] Cl_element024  label="Cl_element : 0.002"  # scripted group (container) (typed FeaturePython)
  n = 0.002
FEATURE [App::DocumentObjectGroupPython] K_element011  label="K_element : 0.017"  # scripted group (container) (typed FeaturePython)
  n = 0.002
FEATURE [App::DocumentObjectGroupPython] G4_TESTIS_ICRP  # scripted group (container) (typed FeaturePython)
  Dunit = g/cm3
  Dvalue = 1.04
  Group = -> [H_element099,C_element108,N_element041,O_element093,Na_element018,P_element010,S_element021,Cl_element024,K_element011]
  conduct = 2
  density = 1
  expand = 3
  formula = G4_TESTIS_ICRP
  name = G4_TESTIS_ICRP
  specific = 4
FEATURE [App::DocumentObjectGroupPython] C_element109  label="C_element : 060"  # scripted group (container) (typed FeaturePython)
  n = 2
  ref = C_element
FEATURE [App::DocumentObjectGroupPython] Cl_element025  label="Cl_element : 012"  # scripted group (container) (typed FeaturePython)
  n = 4
  ref = Cl_element
FEATURE [App::DocumentObjectGroupPython] G4_TETRACHLOROETHYLENE  # scripted group (container) (typed FeaturePython)
  Dunit = g/cm3
  Dvalue = 1.625
  Group = -> [C_element109,Cl_element025]
  conduct = 2
  density = 1
  expand = 3
  formula = G4_TETRACHLOROETHYLENE
  name = G4_TETRACHLOROETHYLENE
  specific = 4
FEATURE [App::DocumentObjectGroupPython] Tl_element001  label="Tl_element : 1"  # scripted group (container) (typed FeaturePython)
  n = 1
  ref = Tl_element
FEATURE [App::DocumentObjectGroupPython] Cl_element026  label="Cl_element : 013"  # scripted group (container) (typed FeaturePython)
  n = 1
  ref = Cl_element
FEATURE [App::DocumentObjectGroupPython] G4_THALLIUM_CHLORIDE  # scripted group (container) (typed FeaturePython)
  Dunit = g/cm3
  Dvalue = 7.004
  Group = -> [Tl_element001,Cl_element026]
  conduct = 2
  density = 1
  expand = 3
  formula = G4_THALLIUM_CHLORIDE
  name = G4_THALLIUM_CHLORIDE
  specific = 4
FEATURE [App::DocumentObjectGroupPython] H_element100  label="H_element : 0.147"  # scripted group (container) (typed FeaturePython)
  n = 0.105
FEATURE [App::DocumentObjectGroupPython] C_element110  label="C_element : 0.256"  # scripted group (container) (typed FeaturePython)
  n = 0.256
FEATURE [App::DocumentObjectGroupPython] N_element042  label="N_element : 0.760"  # scripted group (container) (typed FeaturePython)
  n = 0.027
FEATURE [App::DocumentObjectGroupPython] O_element094  label="O_element : 0.602"  # scripted group (container) (typed FeaturePython)
  n = 0.602
FEATURE [App::DocumentObjectGroupPython] Na_element019  label="Na_element : 0.102"  # scripted group (container) (typed FeaturePython)
  n = 0.001
FEATURE [App::DocumentObjectGroupPython] P_element011  label="P_element : 0.109"  # scripted group (container) (typed FeaturePython)
  n = 0.002
FEATURE [App::DocumentObjectGroupPython] S_element022  label="S_element : 0.023"  # scripted group (container) (typed FeaturePython)
  n = 0.003
FEATURE [App::DocumentObjectGroupPython] Cl_element027  label="Cl_element : 0.591"  # scripted group (container) (typed FeaturePython)
  n = 0.002
FEATURE [App::DocumentObjectGroupPython] K_element012  label="K_element : 0.018"  # scripted group (container) (typed FeaturePython)
  n = 0.002
FEATURE [App::DocumentObjectGroupPython] G4_TISSUE_SOFT_ICRP  # scripted group (container) (typed FeaturePython)
  Dunit = g/cm3
  Dvalue = 1.03
  Group = -> [H_element100,C_element110,N_element042,O_element094,Na_element019,P_element011,S_element022,Cl_element027,K_element012]
  conduct = 2
  density = 1
  expand = 3
  formula = G4_TISSUE_SOFT_ICRP
  name = G4_TISSUE_SOFT_ICRP
  specific = 4
FEATURE [App::DocumentObjectGroupPython] H_element101  label="H_element : 0.148"  # scripted group (container) (typed FeaturePython)
  n = 0.101
FEATURE [App::DocumentObjectGroupPython] C_element111  label="C_element : 0.111"  # scripted group (container) (typed FeaturePython)
  n = 0.111
FEATURE [App::DocumentObjectGroupPython] N_element043  label="N_element : 0.026"  # scripted group (container) (typed FeaturePython)
  n = 0.026
FEATURE [App::DocumentObjectGroupPython] O_element095  label="O_element : 0.762"  # scripted group (container) (typed FeaturePython)
  n = 0.762
FEATURE [App::DocumentObjectGroupPython] G4_TISSUE_SOFT_ICRU_4  label="G4_TISSUE_SOFT_ICRU-4"  # scripted group (container) (typed FeaturePython)
  Dunit = g/cm3
  Dvalue = 1
  Group = -> [H_element101,C_element111,N_element043,O_element095]
  conduct = 2
  density = 1
  expand = 3
  formula = G4_TISSUE_SOFT_ICRU-4
  name = G4_TISSUE_SOFT_ICRU-4
  specific = 4
FEATURE [App::DocumentObjectGroupPython] H_element102  label="H_element : 0.149"  # scripted group (container) (typed FeaturePython)
  n = 0.101869
FEATURE [App::DocumentObjectGroupPython] C_element112  label="C_element : 0.456"  # scripted group (container) (typed FeaturePython)
  n = 0.456179
FEATURE [App::DocumentObjectGroupPython] N_element044  label="N_element : 0.761"  # scripted group (container) (typed FeaturePython)
  n = 0.035172
FEATURE [App::DocumentObjectGroupPython] O_element096  label="O_element : 0.407"  # scripted group (container) (typed FeaturePython)
  n = 0.40678
FEATURE [App::DocumentObjectGroupPython] G4_TISSUE_METHANE  label="G4_TISSUE-METHANE"  # scripted group (container) (typed FeaturePython)
  Dunit = g/cm3
  Dvalue = 0.00106409
  Group = -> [H_element102,C_element112,N_element044,O_element096]
  conduct = 2
  density = 1
  expand = 3
  formula = G4_TISSUE-METHANE
  name = G4_TISSUE-METHANE
  specific = 4
FEATURE [App::DocumentObjectGroupPython] H_element103  label="H_element : 0.103"  # scripted group (container) (typed FeaturePython)
  n = 0.102672
FEATURE [App::DocumentObjectGroupPython] C_element113  label="C_element : 0.569"  # scripted group (container) (typed FeaturePython)
  n = 0.56894
FEATURE [App::DocumentObjectGroupPython] N_element045  label="N_element : 0.762"  # scripted group (container) (typed FeaturePython)
  n = 0.035022
FEATURE [App::DocumentObjectGroupPython] O_element097  label="O_element : 0.293"  # scripted group (container) (typed FeaturePython)
  n = 0.293366
FEATURE [App::DocumentObjectGroupPython] G4_TISSUE_PROPANE  label="G4_TISSUE-PROPANE"  # scripted group (container) (typed FeaturePython)
  Dunit = g/cm3
  Dvalue = 0.00182628
  Group = -> [H_element103,C_element113,N_element045,O_element097]
  conduct = 2
  density = 1
  expand = 3
  formula = G4_TISSUE-PROPANE
  name = G4_TISSUE-PROPANE
  specific = 4
FEATURE [App::DocumentObjectGroupPython] Ti_element003  label="Ti_element : 1"  # scripted group (container) (typed FeaturePython)
  n = 1
  ref = Ti_element
FEATURE [App::DocumentObjectGroupPython] O_element098  label="O_element : 052"  # scripted group (container) (typed FeaturePython)
  n = 2
  ref = O_element
FEATURE [App::DocumentObjectGroupPython] G4_TITANIUM_DIOXIDE  # scripted group (container) (typed FeaturePython)
  Dunit = g/cm3
  Dvalue = 4.26
  Group = -> [Ti_element003,O_element098]
  conduct = 2
  density = 1
  expand = 3
  formula = G4_TITANIUM_DIOXIDE
  name = G4_TITANIUM_DIOXIDE
  specific = 4
FEATURE [App::DocumentObjectGroupPython] C_element114  label="C_element : 061"  # scripted group (container) (typed FeaturePython)
  n = 7
  ref = C_element
FEATURE [App::DocumentObjectGroupPython] H_element104  label="H_element : 055"  # scripted group (container) (typed FeaturePython)
  n = 8
  ref = H_element
FEATURE [App::DocumentObjectGroupPython] G4_TOLUENE  # scripted group (container) (typed FeaturePython)
  Dunit = g/cm3
  Dvalue = 0.8669
  Group = -> [C_element114,H_element104]
  conduct = 2
  density = 1
  expand = 3
  formula = G4_TOLUENE
  name = G4_TOLUENE
  specific = 4
FEATURE [App::DocumentObjectGroupPython] C_element115  label="C_element : 062"  # scripted group (container) (typed FeaturePython)
  n = 2
  ref = C_element
FEATURE [App::DocumentObjectGroupPython] H_element105  label="H_element : 056"  # scripted group (container) (typed FeaturePython)
  n = 1
  ref = H_element
FEATURE [App::DocumentObjectGroupPython] Cl_element028  label="Cl_element : 014"  # scripted group (container) (typed FeaturePython)
  n = 3
  ref = Cl_element
FEATURE [App::DocumentObjectGroupPython] G4_TRICHLOROETHYLENE  # scripted group (container) (typed FeaturePython)
  Dunit = g/cm3
  Dvalue = 1.46
  Group = -> [C_element115,H_element105,Cl_element028]
  conduct = 2
  density = 1
  expand = 3
  formula = G4_TRICHLOROETHYLENE
  name = G4_TRICHLOROETHYLENE
  specific = 4
FEATURE [App::DocumentObjectGroupPython] C_element116  label="C_element : 063"  # scripted group (container) (typed FeaturePython)
  n = 6
  ref = C_element
FEATURE [App::DocumentObjectGroupPython] H_element106  label="H_element : 15"  # scripted group (container) (typed FeaturePython)
  n = 15
  ref = H_element
FEATURE [App::DocumentObjectGroupPython] O_element099  label="O_element : 053"  # scripted group (container) (typed FeaturePython)
  n = 4
  ref = O_element
FEATURE [App::DocumentObjectGroupPython] P_element012  label="P_element : 1"  # scripted group (container) (typed FeaturePython)
  n = 1
  ref = P_element
FEATURE [App::DocumentObjectGroupPython] G4_TRIETHYL_PHOSPHATE  # scripted group (container) (typed FeaturePython)
  Dunit = g/cm3
  Dvalue = 1.07
  Group = -> [C_element116,H_element106,O_element099,P_element012]
  conduct = 2
  density = 1
  expand = 3
  formula = G4_TRIETHYL_PHOSPHATE
  name = G4_TRIETHYL_PHOSPHATE
  specific = 4
FEATURE [App::DocumentObjectGroupPython] W_element003  label="W_element : 003"  # scripted group (container) (typed FeaturePython)
  n = 1
  ref = W_element
FEATURE [App::DocumentObjectGroupPython] F_element017  label="F_element : 6"  # scripted group (container) (typed FeaturePython)
  n = 6
  ref = F_element
FEATURE [App::DocumentObjectGroupPython] G4_TUNGSTEN_HEXAFLUORIDE  # scripted group (container) (typed FeaturePython)
  Dunit = g/cm3
  Dvalue = 2.4
  Group = -> [W_element003,F_element017]
  conduct = 2
  density = 1
  expand = 3
  formula = G4_TUNGSTEN_HEXAFLUORIDE
  name = G4_TUNGSTEN_HEXAFLUORIDE
  specific = 4
FEATURE [App::DocumentObjectGroupPython] U_element001  label="U_element : 1"  # scripted group (container) (typed FeaturePython)
  n = 1
  ref = U_element
FEATURE [App::DocumentObjectGroupPython] C_element117  label="C_element : 064"  # scripted group (container) (typed FeaturePython)
  n = 2
  ref = C_element
FEATURE [App::DocumentObjectGroupPython] G4_URANIUM_DICARBIDE  # scripted group (container) (typed FeaturePython)
  Dunit = g/cm3
  Dvalue = 11.28
  Group = -> [U_element001,C_element117]
  conduct = 2
  density = 1
  expand = 3
  formula = G4_URANIUM_DICARBIDE
  name = G4_URANIUM_DICARBIDE
  specific = 4
FEATURE [App::DocumentObjectGroupPython] U_element002  label="U_element : 002"  # scripted group (container) (typed FeaturePython)
  n = 1
  ref = U_element
FEATURE [App::DocumentObjectGroupPython] C_element118  label="C_element : 065"  # scripted group (container) (typed FeaturePython)
  n = 1
  ref = C_element
FEATURE [App::DocumentObjectGroupPython] G4_URANIUM_MONOCARBIDE  # scripted group (container) (typed FeaturePython)
  Dunit = g/cm3
  Dvalue = 13.63
  Group = -> [U_element002,C_element118]
  conduct = 2
  density = 1
  expand = 3
  formula = G4_URANIUM_MONOCARBIDE
  name = G4_URANIUM_MONOCARBIDE
  specific = 4
FEATURE [App::DocumentObjectGroupPython] U_element003  label="U_element : 003"  # scripted group (container) (typed FeaturePython)
  n = 1
  ref = U_element
FEATURE [App::DocumentObjectGroupPython] O_element100  label="O_element : 054"  # scripted group (container) (typed FeaturePython)
  n = 2
  ref = O_element
FEATURE [App::DocumentObjectGroupPython] G4_URANIUM_OXIDE  # scripted group (container) (typed FeaturePython)
  Dunit = g/cm3
  Dvalue = 10.96
  Group = -> [U_element003,O_element100]
  conduct = 2
  density = 1
  expand = 3
  formula = G4_URANIUM_OXIDE
  name = G4_URANIUM_OXIDE
  specific = 4
FEATURE [App::DocumentObjectGroupPython] C_element119  label="C_element : 066"  # scripted group (container) (typed FeaturePython)
  n = 1
  ref = C_element
FEATURE [App::DocumentObjectGroupPython] H_element107  label="H_element : 057"  # scripted group (container) (typed FeaturePython)
  n = 4
  ref = H_element
FEATURE [App::DocumentObjectGroupPython] N_element046  label="N_element : 019"  # scripted group (container) (typed FeaturePython)
  n = 2
  ref = N_element
FEATURE [App::DocumentObjectGroupPython] O_element101  label="O_element : 055"  # scripted group (container) (typed FeaturePython)
  n = 1
  ref = O_element
FEATURE [App::DocumentObjectGroupPython] G4_UREA  # scripted group (container) (typed FeaturePython)
  Dunit = g/cm3
  Dvalue = 1.323
  Group = -> [C_element119,H_element107,N_element046,O_element101]
  conduct = 2
  density = 1
  expand = 3
  formula = G4_UREA
  name = G4_UREA
  specific = 4
FEATURE [App::DocumentObjectGroupPython] C_element120  label="C_element : 067"  # scripted group (container) (typed FeaturePython)
  n = 5
  ref = C_element
FEATURE [App::DocumentObjectGroupPython] H_element108  label="H_element : 058"  # scripted group (container) (typed FeaturePython)
  n = 11
  ref = H_element
FEATURE [App::DocumentObjectGroupPython] N_element047  label="N_element : 020"  # scripted group (container) (typed FeaturePython)
  n = 1
  ref = N_element
FEATURE [App::DocumentObjectGroupPython] O_element102  label="O_element : 056"  # scripted group (container) (typed FeaturePython)
  n = 2
  ref = O_element
FEATURE [App::DocumentObjectGroupPython] G4_VALINE  # scripted group (container) (typed FeaturePython)
  Dunit = g/cm3
  Dvalue = 1.23
  Group = -> [C_element120,H_element108,N_element047,O_element102]
  conduct = 2
  density = 1
  expand = 3
  formula = G4_VALINE
  name = G4_VALINE
  specific = 4
FEATURE [App::DocumentObjectGroupPython] H_element109  label="H_element : 0.009"  # scripted group (container) (typed FeaturePython)
  n = 0.009417
FEATURE [App::DocumentObjectGroupPython] C_element121  label="C_element : 0.281"  # scripted group (container) (typed FeaturePython)
  n = 0.280555
FEATURE [App::DocumentObjectGroupPython] F_element018  label="F_element : 0.710"  # scripted group (container) (typed FeaturePython)
  n = 0.710028
FEATURE [App::DocumentObjectGroupPython] G4_VITON  # scripted group (container) (typed FeaturePython)
  Dunit = g/cm3
  Dvalue = 1.8
  Group = -> [H_element109,C_element121,F_element018]
  conduct = 2
  density = 1
  expand = 3
  formula = G4_VITON
  name = G4_VITON
  specific = 4
FEATURE [App::DocumentObjectGroupPython] H_element110  label="H_element : 059"  # scripted group (container) (typed FeaturePython)
  n = 2
  ref = H_element
FEATURE [App::DocumentObjectGroupPython] O_element103  label="O_element : 057"  # scripted group (container) (typed FeaturePython)
  n = 1
  ref = O_element
FEATURE [App::DocumentObjectGroupPython] G4_WATER  # scripted group (container) (typed FeaturePython)
  Dunit = g/cm3
  Dvalue = 1
  Group = -> [H_element110,O_element103]
  conduct = 2
  density = 1
  expand = 3
  formula = G4_WATER
  name = G4_WATER
  specific = 4
FEATURE [App::DocumentObjectGroupPython] H_element111  label="H_element : 060"  # scripted group (container) (typed FeaturePython)
  n = 2
  ref = H_element
FEATURE [App::DocumentObjectGroupPython] O_element104  label="O_element : 058"  # scripted group (container) (typed FeaturePython)
  n = 1
  ref = O_element
FEATURE [App::DocumentObjectGroupPython] G4_WATER_VAPOR  # scripted group (container) (typed FeaturePython)
  Dunit = g/cm3
  Dvalue = 0.000756182
  Group = -> [H_element111,O_element104]
  conduct = 2
  density = 1
  expand = 3
  formula = G4_WATER_VAPOR
  name = G4_WATER_VAPOR
  specific = 4
FEATURE [App::DocumentObjectGroupPython] C_element122  label="C_element : 068"  # scripted group (container) (typed FeaturePython)
  n = 8
  ref = C_element
FEATURE [App::DocumentObjectGroupPython] H_element112  label="H_element : 061"  # scripted group (container) (typed FeaturePython)
  n = 10
  ref = H_element
FEATURE [App::DocumentObjectGroupPython] G4_XYLENE  # scripted group (container) (typed FeaturePython)
  Dunit = g/cm3
  Dvalue = 0.87
  Group = -> [C_element122,H_element112]
  conduct = 2
  density = 1
  expand = 3
  formula = G4_XYLENE
  name = G4_XYLENE
  specific = 4
FEATURE [App::DocumentObjectGroupPython] C_element123  label="C_element : 069"  # scripted group (container) (typed FeaturePython)
  n = 1
  ref = C_element
FEATURE [App::DocumentObjectGroupPython] G4_GRAPHITE  # scripted group (container) (typed FeaturePython)
  Dunit = g/cm3
  Dvalue = 2.21
  Group = -> [C_element123]
  conduct = 2
  density = 1
  expand = 3
  formula = G4_GRAPHITE
  name = G4_GRAPHITE
  specific = 4
FEATURE [App::DocumentObjectGroupPython] NIST  # scripted group (container) (typed FeaturePython)
  Group = -> [G4_A_150_TISSUE,G4_ACETONE,G4_ACETYLENE,G4_ADENINE,G4_ADIPOSE_TISSUE_ICRP,G4_AIR,G4_ALANINE,G4_ALUMINUM_OXIDE,G4_AMBER,G4_AMMONIA,G4_ANILINE,G4_ANTHRACENE,G4_B_100_BONE,G4_BAKELITE,G4_BARIUM_FLUORIDE,G4_BARIUM_SULFATE,G4_BENZENE,G4_BERYLLIUM_OXIDE,G4_BGO,G4_BLOOD_ICRP,G4_BONE_COMPACT_ICRU,G4_BONE_CORTICAL_ICRP,G4_BORON_CARBIDE,G4_BORON_OXIDE,G4_BRAIN_ICRP,G4_BUTANE,G4_N_BUTYL_ALCOHOL,G4_C_552,+152 more]
FEATURE [App::DocumentObjectGroupPython] H_element113  label="H_element : 062"  # scripted group (container) (typed FeaturePython)
  n = 1
  ref = H_element
FEATURE [App::DocumentObjectGroupPython] G4_H  # scripted group (container) (typed FeaturePython)
  Dunit = g/cm3
  Dvalue = 8.3748e-05
  Group = -> [H_element113]
  conduct = 2
  density = 1
  expand = 3
  formula = H
  name = G4_H
  specific = 4
FEATURE [App::DocumentObjectGroupPython] He_element001  label="He_element : 1"  # scripted group (container) (typed FeaturePython)
  n = 1
  ref = He_element
FEATURE [App::DocumentObjectGroupPython] G4_He  # scripted group (container) (typed FeaturePython)
  Dunit = g/cm3
  Dvalue = 0.000166322
  Group = -> [He_element001]
  conduct = 2
  density = 1
  expand = 3
  formula = He
  name = G4_He
  specific = 4
FEATURE [App::DocumentObjectGroupPython] Li_element008  label="Li_element : 008"  # scripted group (container) (typed FeaturePython)
  n = 1
  ref = Li_element
FEATURE [App::DocumentObjectGroupPython] G4_Li  # scripted group (container) (typed FeaturePython)
  Dunit = g/cm3
  Dvalue = 0.534
  Group = -> [Li_element008]
  conduct = 2
  density = 1
  expand = 3
  formula = Li
  name = G4_Li
  specific = 4
FEATURE [App::DocumentObjectGroupPython] Be_element002  label="Be_element : 002"  # scripted group (container) (typed FeaturePython)
  n = 1
  ref = Be_element
FEATURE [App::DocumentObjectGroupPython] G4_Be  # scripted group (container) (typed FeaturePython)
  Dunit = g/cm3
  Dvalue = 1.848
  Group = -> [Be_element002]
  conduct = 2
  density = 1
  expand = 3
  formula = Be
  name = G4_Be
  specific = 4
FEATURE [App::DocumentObjectGroupPython] B_element007  label="B_element : 007"  # scripted group (container) (typed FeaturePython)
  n = 1
  ref = B_element
FEATURE [App::DocumentObjectGroupPython] G4_B  # scripted group (container) (typed FeaturePython)
  Dunit = g/cm3
  Dvalue = 2.37
  Group = -> [B_element007]
  conduct = 2
  density = 1
  expand = 3
  formula = B
  name = G4_B
  specific = 4
FEATURE [App::DocumentObjectGroupPython] C_element124  label="C_element : 070"  # scripted group (container) (typed FeaturePython)
  n = 1
  ref = C_element
FEATURE [App::DocumentObjectGroupPython] G4_C  # scripted group (container) (typed FeaturePython)
  Dunit = g/cm3
  Dvalue = 2
  Group = -> [C_element124]
  conduct = 2
  density = 1
  expand = 3
  formula = C
  name = G4_C
  specific = 4
FEATURE [App::DocumentObjectGroupPython] N_element048  label="N_element : 021"  # scripted group (container) (typed FeaturePython)
  n = 1
  ref = N_element
FEATURE [App::DocumentObjectGroupPython] G4_N  # scripted group (container) (typed FeaturePython)
  Dunit = g/cm3
  Dvalue = 0.0011652
  Group = -> [N_element048]
  conduct = 2
  density = 1
  expand = 3
  formula = N
  name = G4_N
  specific = 4
FEATURE [App::DocumentObjectGroupPython] O_element105  label="O_element : 059"  # scripted group (container) (typed FeaturePython)
  n = 1
  ref = O_element
FEATURE [App::DocumentObjectGroupPython] G4_O  # scripted group (container) (typed FeaturePython)
  Dunit = g/cm3
  Dvalue = 0.00133151
  Group = -> [O_element105]
  conduct = 2
  density = 1
  expand = 3
  formula = O
  name = G4_O
  specific = 4
FEATURE [App::DocumentObjectGroupPython] F_element019  label="F_element : 008"  # scripted group (container) (typed FeaturePython)
  n = 1
  ref = F_element
FEATURE [App::DocumentObjectGroupPython] G4_F  # scripted group (container) (typed FeaturePython)
  Dunit = g/cm3
  Dvalue = 0.00158029
  Group = -> [F_element019]
  conduct = 2
  density = 1
  expand = 3
  formula = F
  name = G4_F
  specific = 4
FEATURE [App::DocumentObjectGroupPython] Ne_element001  label="Ne_element : 1"  # scripted group (container) (typed FeaturePython)
  n = 1
  ref = Ne_element
FEATURE [App::DocumentObjectGroupPython] G4_Ne  # scripted group (container) (typed FeaturePython)
  Dunit = g/cm3
  Dvalue = 0.000838505
  Group = -> [Ne_element001]
  conduct = 2
  density = 1
  expand = 3
  formula = Ne
  name = G4_Ne
  specific = 4
FEATURE [App::DocumentObjectGroupPython] Na_element020  label="Na_element : 005"  # scripted group (container) (typed FeaturePython)
  n = 1
  ref = Na_element
FEATURE [App::DocumentObjectGroupPython] G4_Na  # scripted group (container) (typed FeaturePython)
  Dunit = g/cm3
  Dvalue = 0.971
  Group = -> [Na_element020]
  conduct = 2
  density = 1
  expand = 3
  formula = Na
  name = G4_Na
  specific = 4
FEATURE [App::DocumentObjectGroupPython] Mg_element011  label="Mg_element : 005"  # scripted group (container) (typed FeaturePython)
  n = 1
  ref = Mg_element
FEATURE [App::DocumentObjectGroupPython] G4_Mg  # scripted group (container) (typed FeaturePython)
  Dunit = g/cm3
  Dvalue = 1.74
  Group = -> [Mg_element011]
  conduct = 2
  density = 1
  expand = 3
  formula = Mg
  name = G4_Mg
  specific = 4
FEATURE [App::DocumentObjectGroupPython] Al_element004  label="Al_element : 1"  # scripted group (container) (typed FeaturePython)
  n = 1
  ref = Al_element
FEATURE [App::DocumentObjectGroupPython] G4_Al  # scripted group (container) (typed FeaturePython)
  Dunit = g/cm3
  Dvalue = 2.699
  Group = -> [Al_element004]
  conduct = 2
  density = 1
  expand = 3
  formula = Al
  name = G4_Al
  specific = 4
FEATURE [App::DocumentObjectGroupPython] Si_element007  label="Si_element : 002"  # scripted group (container) (typed FeaturePython)
  n = 1
  ref = Si_element
FEATURE [App::DocumentObjectGroupPython] G4_Si  # scripted group (container) (typed FeaturePython)
  Dunit = g/cm3
  Dvalue = 2.33
  Group = -> [Si_element007]
  conduct = 2
  density = 1
  expand = 3
  formula = Si
  name = G4_Si
  specific = 4
FEATURE [App::DocumentObjectGroupPython] P_element013  label="P_element : 002"  # scripted group (container) (typed FeaturePython)
  n = 1
  ref = P_element
FEATURE [App::DocumentObjectGroupPython] G4_P  # scripted group (container) (typed FeaturePython)
  Dunit = g/cm3
  Dvalue = 2.2
  Group = -> [P_element013]
  conduct = 2
  density = 1
  expand = 3
  formula = P
  name = G4_P
  specific = 4
FEATURE [App::DocumentObjectGroupPython] S_element023  label="S_element : 007"  # scripted group (container) (typed FeaturePython)
  n = 1
  ref = S_element
FEATURE [App::DocumentObjectGroupPython] G4_S  # scripted group (container) (typed FeaturePython)
  Dunit = g/cm3
  Dvalue = 2
  Group = -> [S_element023]
  conduct = 2
  density = 1
  expand = 3
  formula = S
  name = G4_S
  specific = 4
FEATURE [App::DocumentObjectGroupPython] Cl_element029  label="Cl_element : 015"  # scripted group (container) (typed FeaturePython)
  n = 1
  ref = Cl_element
FEATURE [App::DocumentObjectGroupPython] G4_Cl  # scripted group (container) (typed FeaturePython)
  Dunit = g/cm3
  Dvalue = 0.00299473
  Group = -> [Cl_element029]
  conduct = 2
  density = 1
  expand = 3
  formula = Cl
  name = G4_Cl
  specific = 4
FEATURE [App::DocumentObjectGroupPython] Ar_element002  label="Ar_element : 1"  # scripted group (container) (typed FeaturePython)
  n = 1
  ref = Ar_element
FEATURE [App::DocumentObjectGroupPython] G4_Ar  # scripted group (container) (typed FeaturePython)
  Dunit = g/cm3
  Dvalue = 0.00166201
  Group = -> [Ar_element002]
  conduct = 2
  density = 1
  expand = 3
  formula = Ar
  name = G4_Ar
  specific = 4
FEATURE [App::DocumentObjectGroupPython] K_element013  label="K_element : 003"  # scripted group (container) (typed FeaturePython)
  n = 1
  ref = K_element
FEATURE [App::DocumentObjectGroupPython] G4_K  # scripted group (container) (typed FeaturePython)
  Dunit = g/cm3
  Dvalue = 0.862
  Group = -> [K_element013]
  conduct = 2
  density = 1
  expand = 3
  formula = K
  name = G4_K
  specific = 4
FEATURE [App::DocumentObjectGroupPython] Ca_element014  label="Ca_element : 007"  # scripted group (container) (typed FeaturePython)
  n = 1
  ref = Ca_element
FEATURE [App::DocumentObjectGroupPython] G4_Ca  # scripted group (container) (typed FeaturePython)
  Dunit = g/cm3
  Dvalue = 1.55
  Group = -> [Ca_element014]
  conduct = 2
  density = 1
  expand = 3
  formula = Ca
  name = G4_Ca
  specific = 4
FEATURE [App::DocumentObjectGroupPython] Sc_element001  label="Sc_element : 1"  # scripted group (container) (typed FeaturePython)
  n = 1
  ref = Sc_element
FEATURE [App::DocumentObjectGroupPython] G4_Sc  # scripted group (container) (typed FeaturePython)
  Dunit = g/cm3
  Dvalue = 2.989
  Group = -> [Sc_element001]
  conduct = 2
  density = 1
  expand = 3
  formula = Sc
  name = G4_Sc
  specific = 4
FEATURE [App::DocumentObjectGroupPython] Ti_element004  label="Ti_element : 002"  # scripted group (container) (typed FeaturePython)
  n = 1
  ref = Ti_element
FEATURE [App::DocumentObjectGroupPython] G4_Ti  # scripted group (container) (typed FeaturePython)
  Dunit = g/cm3
  Dvalue = 4.54
  Group = -> [Ti_element004]
  conduct = 2
  density = 1
  expand = 3
  formula = Ti
  name = G4_Ti
  specific = 4
FEATURE [App::DocumentObjectGroupPython] V_element001  label="V_element : 1"  # scripted group (container) (typed FeaturePython)
  n = 1
  ref = V_element
FEATURE [App::DocumentObjectGroupPython] G4_V  # scripted group (container) (typed FeaturePython)
  Dunit = g/cm3
  Dvalue = 6.11
  Group = -> [V_element001]
  conduct = 2
  density = 1
  expand = 3
  formula = V
  name = G4_V
  specific = 4
FEATURE [App::DocumentObjectGroupPython] Cr_element001  label="Cr_element : 1"  # scripted group (container) (typed FeaturePython)
  n = 1
  ref = Cr_element
FEATURE [App::DocumentObjectGroupPython] G4_Cr  # scripted group (container) (typed FeaturePython)
  Dunit = g/cm3
  Dvalue = 7.18
  Group = -> [Cr_element001]
  conduct = 2
  density = 1
  expand = 3
  formula = Cr
  name = G4_Cr
  specific = 4
FEATURE [App::DocumentObjectGroupPython] Mn_element001  label="Mn_element : 1"  # scripted group (container) (typed FeaturePython)
  n = 1
  ref = Mn_element
FEATURE [App::DocumentObjectGroupPython] G4_Mn  # scripted group (container) (typed FeaturePython)
  Dunit = g/cm3
  Dvalue = 7.44
  Group = -> [Mn_element001]
  conduct = 2
  density = 1
  expand = 3
  formula = Mn
  name = G4_Mn
  specific = 4
FEATURE [App::DocumentObjectGroupPython] Fe_element007  label="Fe_element : 004"  # scripted group (container) (typed FeaturePython)
  n = 1
  ref = Fe_element
FEATURE [App::DocumentObjectGroupPython] G4_Fe  # scripted group (container) (typed FeaturePython)
  Dunit = g/cm3
  Dvalue = 7.874
  Group = -> [Fe_element007]
  conduct = 2
  density = 1
  expand = 3
  formula = Fe
  name = G4_Fe
  specific = 4
FEATURE [App::DocumentObjectGroupPython] Co_element001  label="Co_element : 1"  # scripted group (container) (typed FeaturePython)
  n = 1
  ref = Co_element
FEATURE [App::DocumentObjectGroupPython] G4_Co  # scripted group (container) (typed FeaturePython)
  Dunit = g/cm3
  Dvalue = 8.9
  Group = -> [Co_element001]
  conduct = 2
  density = 1
  expand = 3
  formula = Co
  name = G4_Co
  specific = 4
FEATURE [App::DocumentObjectGroupPython] Ni_element001  label="Ni_element : 1"  # scripted group (container) (typed FeaturePython)
  n = 1
  ref = Ni_element
FEATURE [App::DocumentObjectGroupPython] G4_Ni  # scripted group (container) (typed FeaturePython)
  Dunit = g/cm3
  Dvalue = 8.902
  Group = -> [Ni_element001]
  conduct = 2
  density = 1
  expand = 3
  formula = Ni
  name = G4_Ni
  specific = 4
FEATURE [App::DocumentObjectGroupPython] Cu_element001  label="Cu_element : 1"  # scripted group (container) (typed FeaturePython)
  n = 1
  ref = Cu_element
FEATURE [App::DocumentObjectGroupPython] G4_Cu  # scripted group (container) (typed FeaturePython)
  Dunit = g/cm3
  Dvalue = 8.96
  Group = -> [Cu_element001]
  conduct = 2
  density = 1
  expand = 3
  formula = Cu
  name = G4_Cu
  specific = 4
FEATURE [App::DocumentObjectGroupPython] Zn_element001  label="Zn_element : 1"  # scripted group (container) (typed FeaturePython)
  n = 1
  ref = Zn_element
FEATURE [App::DocumentObjectGroupPython] G4_Zn  # scripted group (container) (typed FeaturePython)
  Dunit = g/cm3
  Dvalue = 7.133
  Group = -> [Zn_element001]
  conduct = 2
  density = 1
  expand = 3
  formula = Zn
  name = G4_Zn
  specific = 4
FEATURE [App::DocumentObjectGroupPython] Ga_element002  label="Ga_element : 002"  # scripted group (container) (typed FeaturePython)
  n = 1
  ref = Ga_element
FEATURE [App::DocumentObjectGroupPython] G4_Ga  # scripted group (container) (typed FeaturePython)
  Dunit = g/cm3
  Dvalue = 5.904
  Group = -> [Ga_element002]
  conduct = 2
  density = 1
  expand = 3
  formula = Ga
  name = G4_Ga
  specific = 4
FEATURE [App::DocumentObjectGroupPython] Ge_element002  label="Ge_element : 1"  # scripted group (container) (typed FeaturePython)
  n = 1
  ref = Ge_element
FEATURE [App::DocumentObjectGroupPython] G4_Ge  # scripted group (container) (typed FeaturePython)
  Dunit = g/cm3
  Dvalue = 5.323
  Group = -> [Ge_element002]
  conduct = 2
  density = 1
  expand = 3
  formula = Ge
  name = G4_Ge
  specific = 4
FEATURE [App::DocumentObjectGroupPython] As_element003  label="As_element : 002"  # scripted group (container) (typed FeaturePython)
  n = 1
  ref = As_element
FEATURE [App::DocumentObjectGroupPython] G4_As  # scripted group (container) (typed FeaturePython)
  Dunit = g/cm3
  Dvalue = 5.73
  Group = -> [As_element003]
  conduct = 2
  density = 1
  expand = 3
  formula = As
  name = G4_As
  specific = 4
FEATURE [App::DocumentObjectGroupPython] Se_element001  label="Se_element : 1"  # scripted group (container) (typed FeaturePython)
  n = 1
  ref = Se_element
FEATURE [App::DocumentObjectGroupPython] G4_Se  # scripted group (container) (typed FeaturePython)
  Dunit = g/cm3
  Dvalue = 4.5
  Group = -> [Se_element001]
  conduct = 2
  density = 1
  expand = 3
  formula = Se
  name = G4_Se
  specific = 4
FEATURE [App::DocumentObjectGroupPython] Br_element007  label="Br_element : 004"  # scripted group (container) (typed FeaturePython)
  n = 1
  ref = Br_element
FEATURE [App::DocumentObjectGroupPython] G4_Br  # scripted group (container) (typed FeaturePython)
  Dunit = g/cm3
  Dvalue = 0.0070721
  Group = -> [Br_element007]
  conduct = 2
  density = 1
  expand = 3
  formula = Br
  name = G4_Br
  specific = 4
FEATURE [App::DocumentObjectGroupPython] Kr_element001  label="Kr_element : 1"  # scripted group (container) (typed FeaturePython)
  n = 1
  ref = Kr_element
FEATURE [App::DocumentObjectGroupPython] G4_Kr  # scripted group (container) (typed FeaturePython)
  Dunit = g/cm3
  Dvalue = 0.00347832
  Group = -> [Kr_element001]
  conduct = 2
  density = 1
  expand = 3
  formula = Kr
  name = G4_Kr
  specific = 4
FEATURE [App::DocumentObjectGroupPython] Rb_element001  label="Rb_element : 1"  # scripted group (container) (typed FeaturePython)
  n = 1
  ref = Rb_element
FEATURE [App::DocumentObjectGroupPython] G4_Rb  # scripted group (container) (typed FeaturePython)
  Dunit = g/cm3
  Dvalue = 1.532
  Group = -> [Rb_element001]
  conduct = 2
  density = 1
  expand = 3
  formula = Rb
  name = G4_Rb
  specific = 4
FEATURE [App::DocumentObjectGroupPython] Sr_element001  label="Sr_element : 1"  # scripted group (container) (typed FeaturePython)
  n = 1
  ref = Sr_element
FEATURE [App::DocumentObjectGroupPython] G4_Sr  # scripted group (container) (typed FeaturePython)
  Dunit = g/cm3
  Dvalue = 2.54
  Group = -> [Sr_element001]
  conduct = 2
  density = 1
  expand = 3
  formula = Sr
  name = G4_Sr
  specific = 4
FEATURE [App::DocumentObjectGroupPython] Y_element001  label="Y_element : 1"  # scripted group (container) (typed FeaturePython)
  n = 1
  ref = Y_element
FEATURE [App::DocumentObjectGroupPython] G4_Y  # scripted group (container) (typed FeaturePython)
  Dunit = g/cm3
  Dvalue = 4.469
  Group = -> [Y_element001]
  conduct = 2
  density = 1
  expand = 3
  formula = Y
  name = G4_Y
  specific = 4
FEATURE [App::DocumentObjectGroupPython] Zr_element001  label="Zr_element : 1"  # scripted group (container) (typed FeaturePython)
  n = 1
  ref = Zr_element
FEATURE [App::DocumentObjectGroupPython] G4_Zr  # scripted group (container) (typed FeaturePython)
  Dunit = g/cm3
  Dvalue = 6.506
  Group = -> [Zr_element001]
  conduct = 2
  density = 1
  expand = 3
  formula = Zr
  name = G4_Zr
  specific = 4
FEATURE [App::DocumentObjectGroupPython] Nb_element001  label="Nb_element : 1"  # scripted group (container) (typed FeaturePython)
  n = 1
  ref = Nb_element
FEATURE [App::DocumentObjectGroupPython] G4_Nb  # scripted group (container) (typed FeaturePython)
  Dunit = g/cm3
  Dvalue = 8.57
  Group = -> [Nb_element001]
  conduct = 2
  density = 1
  expand = 3
  formula = Nb
  name = G4_Nb
  specific = 4
FEATURE [App::DocumentObjectGroupPython] Mo_element001  label="Mo_element : 1"  # scripted group (container) (typed FeaturePython)
  n = 1
  ref = Mo_element
FEATURE [App::DocumentObjectGroupPython] G4_Mo  # scripted group (container) (typed FeaturePython)
  Dunit = g/cm3
  Dvalue = 10.22
  Group = -> [Mo_element001]
  conduct = 2
  density = 1
  expand = 3
  formula = Mo
  name = G4_Mo
  specific = 4
FEATURE [App::DocumentObjectGroupPython] Tc_element001  label="Tc_element : 1"  # scripted group (container) (typed FeaturePython)
  n = 1
  ref = Tc_element
FEATURE [App::DocumentObjectGroupPython] G4_Tc  # scripted group (container) (typed FeaturePython)
  Dunit = g/cm3
  Dvalue = 11.5
  Group = -> [Tc_element001]
  conduct = 2
  density = 1
  expand = 3
  formula = Tc
  name = G4_Tc
  specific = 4
FEATURE [App::DocumentObjectGroupPython] Ru_element001  label="Ru_element : 1"  # scripted group (container) (typed FeaturePython)
  n = 1
  ref = Ru_element
FEATURE [App::DocumentObjectGroupPython] G4_Ru  # scripted group (container) (typed FeaturePython)
  Dunit = g/cm3
  Dvalue = 12.41
  Group = -> [Ru_element001]
  conduct = 2
  density = 1
  expand = 3
  formula = Ru
  name = G4_Ru
  specific = 4
FEATURE [App::DocumentObjectGroupPython] Rh_element001  label="Rh_element : 1"  # scripted group (container) (typed FeaturePython)
  n = 1
  ref = Rh_element
FEATURE [App::DocumentObjectGroupPython] G4_Rh  # scripted group (container) (typed FeaturePython)
  Dunit = g/cm3
  Dvalue = 12.41
  Group = -> [Rh_element001]
  conduct = 2
  density = 1
  expand = 3
  formula = Rh
  name = G4_Rh
  specific = 4
FEATURE [App::DocumentObjectGroupPython] Pd_element001  label="Pd_element : 1"  # scripted group (container) (typed FeaturePython)
  n = 1
  ref = Pd_element
FEATURE [App::DocumentObjectGroupPython] G4_Pd  # scripted group (container) (typed FeaturePython)
  Dunit = g/cm3
  Dvalue = 12.02
  Group = -> [Pd_element001]
  conduct = 2
  density = 1
  expand = 3
  formula = Pd
  name = G4_Pd
  specific = 4
FEATURE [App::DocumentObjectGroupPython] Ag_element006  label="Ag_element : 004"  # scripted group (container) (typed FeaturePython)
  n = 1
  ref = Ag_element
FEATURE [App::DocumentObjectGroupPython] G4_Ag  # scripted group (container) (typed FeaturePython)
  Dunit = g/cm3
  Dvalue = 10.5
  Group = -> [Ag_element006]
  conduct = 2
  density = 1
  expand = 3
  formula = Ag
  name = G4_Ag
  specific = 4
FEATURE [App::DocumentObjectGroupPython] Cd_element003  label="Cd_element : 003"  # scripted group (container) (typed FeaturePython)
  n = 1
  ref = Cd_element
FEATURE [App::DocumentObjectGroupPython] G4_Cd  # scripted group (container) (typed FeaturePython)
  Dunit = g/cm3
  Dvalue = 8.65
  Group = -> [Cd_element003]
  conduct = 2
  density = 1
  expand = 3
  formula = Cd
  name = G4_Cd
  specific = 4
FEATURE [App::DocumentObjectGroupPython] In_element001  label="In_element : 1"  # scripted group (container) (typed FeaturePython)
  n = 1
  ref = In_element
FEATURE [App::DocumentObjectGroupPython] G4_In  # scripted group (container) (typed FeaturePython)
  Dunit = g/cm3
  Dvalue = 7.31
  Group = -> [In_element001]
  conduct = 2
  density = 1
  expand = 3
  formula = In
  name = G4_In
  specific = 4
FEATURE [App::DocumentObjectGroupPython] Sn_element001  label="Sn_element : 1"  # scripted group (container) (typed FeaturePython)
  n = 1
  ref = Sn_element
FEATURE [App::DocumentObjectGroupPython] G4_Sn  # scripted group (container) (typed FeaturePython)
  Dunit = g/cm3
  Dvalue = 7.31
  Group = -> [Sn_element001]
  conduct = 2
  density = 1
  expand = 3
  formula = Sn
  name = G4_Sn
  specific = 4
FEATURE [App::DocumentObjectGroupPython] Sb_element001  label="Sb_element : 1"  # scripted group (container) (typed FeaturePython)
  n = 1
  ref = Sb_element
FEATURE [App::DocumentObjectGroupPython] G4_Sb  # scripted group (container) (typed FeaturePython)
  Dunit = g/cm3
  Dvalue = 6.691
  Group = -> [Sb_element001]
  conduct = 2
  density = 1
  expand = 3
  formula = Sb
  name = G4_Sb
  specific = 4
FEATURE [App::DocumentObjectGroupPython] Te_element002  label="Te_element : 002"  # scripted group (container) (typed FeaturePython)
  n = 1
  ref = Te_element
FEATURE [App::DocumentObjectGroupPython] G4_Te  # scripted group (container) (typed FeaturePython)
  Dunit = g/cm3
  Dvalue = 6.24
  Group = -> [Te_element002]
  conduct = 2
  density = 1
  expand = 3
  formula = Te
  name = G4_Te
  specific = 4
FEATURE [App::DocumentObjectGroupPython] I_element010  label="I_element : 006"  # scripted group (container) (typed FeaturePython)
  n = 1
  ref = I_element
FEATURE [App::DocumentObjectGroupPython] G4_I  # scripted group (container) (typed FeaturePython)
  Dunit = g/cm3
  Dvalue = 4.93
  Group = -> [I_element010]
  conduct = 2
  density = 1
  expand = 3
  formula = I
  name = G4_I
  specific = 4
FEATURE [App::DocumentObjectGroupPython] Xe_element001  label="Xe_element : 1"  # scripted group (container) (typed FeaturePython)
  n = 1
  ref = Xe_element
FEATURE [App::DocumentObjectGroupPython] G4_Xe  # scripted group (container) (typed FeaturePython)
  Dunit = g/cm3
  Dvalue = 0.00548536
  Group = -> [Xe_element001]
  conduct = 2
  density = 1
  expand = 3
  formula = Xe
  name = G4_Xe
  specific = 4
FEATURE [App::DocumentObjectGroupPython] Cs_element003  label="Cs_element : 003"  # scripted group (container) (typed FeaturePython)
  n = 1
  ref = Cs_element
FEATURE [App::DocumentObjectGroupPython] G4_Cs  # scripted group (container) (typed FeaturePython)
  Dunit = g/cm3
  Dvalue = 1.873
  Group = -> [Cs_element003]
  conduct = 2
  density = 1
  expand = 3
  formula = Cs
  name = G4_Cs
  specific = 4
FEATURE [App::DocumentObjectGroupPython] Ba_element003  label="Ba_element : 003"  # scripted group (container) (typed FeaturePython)
  n = 1
  ref = Ba_element
FEATURE [App::DocumentObjectGroupPython] G4_Ba  # scripted group (container) (typed FeaturePython)
  Dunit = g/cm3
  Dvalue = 3.5
  Group = -> [Ba_element003]
  conduct = 2
  density = 1
  expand = 3
  formula = Ba
  name = G4_Ba
  specific = 4
FEATURE [App::DocumentObjectGroupPython] La_element003  label="La_element : 003"  # scripted group (container) (typed FeaturePython)
  n = 1
  ref = La_element
FEATURE [App::DocumentObjectGroupPython] G4_La  # scripted group (container) (typed FeaturePython)
  Dunit = g/cm3
  Dvalue = 6.154
  Group = -> [La_element003]
  conduct = 2
  density = 1
  expand = 3
  formula = La
  name = G4_La
  specific = 4
FEATURE [App::DocumentObjectGroupPython] Ce_element002  label="Ce_element : 1"  # scripted group (container) (typed FeaturePython)
  n = 1
  ref = Ce_element
FEATURE [App::DocumentObjectGroupPython] G4_Ce  # scripted group (container) (typed FeaturePython)
  Dunit = g/cm3
  Dvalue = 6.657
  Group = -> [Ce_element002]
  conduct = 2
  density = 1
  expand = 3
  formula = Ce
  name = G4_Ce
  specific = 4
FEATURE [App::DocumentObjectGroupPython] Pr_element001  label="Pr_element : 1"  # scripted group (container) (typed FeaturePython)
  n = 1
  ref = Pr_element
FEATURE [App::DocumentObjectGroupPython] G4_Pr  # scripted group (container) (typed FeaturePython)
  Dunit = g/cm3
  Dvalue = 6.71
  Group = -> [Pr_element001]
  conduct = 2
  density = 1
  expand = 3
  formula = Pr
  name = G4_Pr
  specific = 4
FEATURE [App::DocumentObjectGroupPython] Nd_element001  label="Nd_element : 1"  # scripted group (container) (typed FeaturePython)
  n = 1
  ref = Nd_element
FEATURE [App::DocumentObjectGroupPython] G4_Nd  # scripted group (container) (typed FeaturePython)
  Dunit = g/cm3
  Dvalue = 6.9
  Group = -> [Nd_element001]
  conduct = 2
  density = 1
  expand = 3
  formula = Nd
  name = G4_Nd
  specific = 4
FEATURE [App::DocumentObjectGroupPython] Pm_element001  label="Pm_element : 1"  # scripted group (container) (typed FeaturePython)
  n = 1
  ref = Pm_element
FEATURE [App::DocumentObjectGroupPython] G4_Pm  # scripted group (container) (typed FeaturePython)
  Dunit = g/cm3
  Dvalue = 7.22
  Group = -> [Pm_element001]
  conduct = 2
  density = 1
  expand = 3
  formula = Pm
  name = G4_Pm
  specific = 4
FEATURE [App::DocumentObjectGroupPython] Sm_element001  label="Sm_element : 1"  # scripted group (container) (typed FeaturePython)
  n = 1
  ref = Sm_element
FEATURE [App::DocumentObjectGroupPython] G4_Sm  # scripted group (container) (typed FeaturePython)
  Dunit = g/cm3
  Dvalue = 7.46
  Group = -> [Sm_element001]
  conduct = 2
  density = 1
  expand = 3
  formula = Sm
  name = G4_Sm
  specific = 4
FEATURE [App::DocumentObjectGroupPython] Eu_element001  label="Eu_element : 1"  # scripted group (container) (typed FeaturePython)
  n = 1
  ref = Eu_element
FEATURE [App::DocumentObjectGroupPython] G4_Eu  # scripted group (container) (typed FeaturePython)
  Dunit = g/cm3
  Dvalue = 5.243
  Group = -> [Eu_element001]
  conduct = 2
  density = 1
  expand = 3
  formula = Eu
  name = G4_Eu
  specific = 4
FEATURE [App::DocumentObjectGroupPython] Gd_element002  label="Gd_element : 1"  # scripted group (container) (typed FeaturePython)
  n = 1
  ref = Gd_element
FEATURE [App::DocumentObjectGroupPython] G4_Gd  # scripted group (container) (typed FeaturePython)
  Dunit = g/cm3
  Dvalue = 7.9004
  Group = -> [Gd_element002]
  conduct = 2
  density = 1
  expand = 3
  formula = Gd
  name = G4_Gd
  specific = 4
FEATURE [App::DocumentObjectGroupPython] Tb_element001  label="Tb_element : 1"  # scripted group (container) (typed FeaturePython)
  n = 1
  ref = Tb_element
FEATURE [App::DocumentObjectGroupPython] G4_Tb  # scripted group (container) (typed FeaturePython)
  Dunit = g/cm3
  Dvalue = 8.229
  Group = -> [Tb_element001]
  conduct = 2
  density = 1
  expand = 3
  formula = Tb
  name = G4_Tb
  specific = 4
FEATURE [App::DocumentObjectGroupPython] Dy_element001  label="Dy_element : 1"  # scripted group (container) (typed FeaturePython)
  n = 1
  ref = Dy_element
FEATURE [App::DocumentObjectGroupPython] G4_Dy  # scripted group (container) (typed FeaturePython)
  Dunit = g/cm3
  Dvalue = 8.55
  Group = -> [Dy_element001]
  conduct = 2
  density = 1
  expand = 3
  formula = Dy
  name = G4_Dy
  specific = 4
FEATURE [App::DocumentObjectGroupPython] Ho_element001  label="Ho_element : 1"  # scripted group (container) (typed FeaturePython)
  n = 1
  ref = Ho_element
FEATURE [App::DocumentObjectGroupPython] G4_Ho  # scripted group (container) (typed FeaturePython)
  Dunit = g/cm3
  Dvalue = 8.795
  Group = -> [Ho_element001]
  conduct = 2
  density = 1
  expand = 3
  formula = Ho
  name = G4_Ho
  specific = 4
FEATURE [App::DocumentObjectGroupPython] Er_element001  label="Er_element : 1"  # scripted group (container) (typed FeaturePython)
  n = 1
  ref = Er_element
FEATURE [App::DocumentObjectGroupPython] G4_Er  # scripted group (container) (typed FeaturePython)
  Dunit = g/cm3
  Dvalue = 9.066
  Group = -> [Er_element001]
  conduct = 2
  density = 1
  expand = 3
  formula = Er
  name = G4_Er
  specific = 4
FEATURE [App::DocumentObjectGroupPython] Tm_element001  label="Tm_element : 1"  # scripted group (container) (typed FeaturePython)
  n = 1
  ref = Tm_element
FEATURE [App::DocumentObjectGroupPython] G4_Tm  # scripted group (container) (typed FeaturePython)
  Dunit = g/cm3
  Dvalue = 9.321
  Group = -> [Tm_element001]
  conduct = 2
  density = 1
  expand = 3
  formula = Tm
  name = G4_Tm
  specific = 4
FEATURE [App::DocumentObjectGroupPython] Yb_element001  label="Yb_element : 1"  # scripted group (container) (typed FeaturePython)
  n = 1
  ref = Yb_element
FEATURE [App::DocumentObjectGroupPython] G4_Yb  # scripted group (container) (typed FeaturePython)
  Dunit = g/cm3
  Dvalue = 6.73
  Group = -> [Yb_element001]
  conduct = 2
  density = 1
  expand = 3
  formula = Yb
  name = G4_Yb
  specific = 4
FEATURE [App::DocumentObjectGroupPython] Lu_element001  label="Lu_element : 1"  # scripted group (container) (typed FeaturePython)
  n = 1
  ref = Lu_element
FEATURE [App::DocumentObjectGroupPython] G4_Lu  # scripted group (container) (typed FeaturePython)
  Dunit = g/cm3
  Dvalue = 9.84
  Group = -> [Lu_element001]
  conduct = 2
  density = 1
  expand = 3
  formula = Lu
  name = G4_Lu
  specific = 4
FEATURE [App::DocumentObjectGroupPython] Hf_element001  label="Hf_element : 1"  # scripted group (container) (typed FeaturePython)
  n = 1
  ref = Hf_element
FEATURE [App::DocumentObjectGroupPython] G4_Hf  # scripted group (container) (typed FeaturePython)
  Dunit = g/cm3
  Dvalue = 13.31
  Group = -> [Hf_element001]
  conduct = 2
  density = 1
  expand = 3
  formula = Hf
  name = G4_Hf
  specific = 4
FEATURE [App::DocumentObjectGroupPython] Ta_element001  label="Ta_element : 1"  # scripted group (container) (typed FeaturePython)
  n = 1
  ref = Ta_element
FEATURE [App::DocumentObjectGroupPython] G4_Ta  # scripted group (container) (typed FeaturePython)
  Dunit = g/cm3
  Dvalue = 16.654
  Group = -> [Ta_element001]
  conduct = 2
  density = 1
  expand = 3
  formula = Ta
  name = G4_Ta
  specific = 4
FEATURE [App::DocumentObjectGroupPython] W_element004  label="W_element : 004"  # scripted group (container) (typed FeaturePython)
  n = 1
  ref = W_element
FEATURE [App::DocumentObjectGroupPython] G4_W  # scripted group (container) (typed FeaturePython)
  Dunit = g/cm3
  Dvalue = 19.3
  Group = -> [W_element004]
  conduct = 2
  density = 1
  expand = 3
  formula = W
  name = G4_W
  specific = 4
FEATURE [App::DocumentObjectGroupPython] Re_element001  label="Re_element : 1"  # scripted group (container) (typed FeaturePython)
  n = 1
  ref = Re_element
FEATURE [App::DocumentObjectGroupPython] G4_Re  # scripted group (container) (typed FeaturePython)
  Dunit = g/cm3
  Dvalue = 21.02
  Group = -> [Re_element001]
  conduct = 2
  density = 1
  expand = 3
  formula = Re
  name = G4_Re
  specific = 4
FEATURE [App::DocumentObjectGroupPython] Os_element001  label="Os_element : 1"  # scripted group (container) (typed FeaturePython)
  n = 1
  ref = Os_element
FEATURE [App::DocumentObjectGroupPython] G4_Os  # scripted group (container) (typed FeaturePython)
  Dunit = g/cm3
  Dvalue = 22.57
  Group = -> [Os_element001]
  conduct = 2
  density = 1
  expand = 3
  formula = Os
  name = G4_Os
  specific = 4
FEATURE [App::DocumentObjectGroupPython] Ir_element001  label="Ir_element : 1"  # scripted group (container) (typed FeaturePython)
  n = 1
  ref = Ir_element
FEATURE [App::DocumentObjectGroupPython] G4_Ir  # scripted group (container) (typed FeaturePython)
  Dunit = g/cm3
  Dvalue = 22.42
  Group = -> [Ir_element001]
  conduct = 2
  density = 1
  expand = 3
  formula = Ir
  name = G4_Ir
  specific = 4
FEATURE [App::DocumentObjectGroupPython] Pt_element001  label="Pt_element : 1"  # scripted group (container) (typed FeaturePython)
  n = 1
  ref = Pt_element
FEATURE [App::DocumentObjectGroupPython] G4_Pt  # scripted group (container) (typed FeaturePython)
  Dunit = g/cm3
  Dvalue = 21.45
  Group = -> [Pt_element001]
  conduct = 2
  density = 1
  expand = 3
  formula = Pt
  name = G4_Pt
  specific = 4
FEATURE [App::DocumentObjectGroupPython] Au_element001  label="Au_element : 1"  # scripted group (container) (typed FeaturePython)
  n = 1
  ref = Au_element
FEATURE [App::DocumentObjectGroupPython] G4_Au  # scripted group (container) (typed FeaturePython)
  Dunit = g/cm3
  Dvalue = 19.32
  Group = -> [Au_element001]
  conduct = 2
  density = 1
  expand = 3
  formula = Au
  name = G4_Au
  specific = 4
FEATURE [App::DocumentObjectGroupPython] Hg_element002  label="Hg_element : 002"  # scripted group (container) (typed FeaturePython)
  n = 1
  ref = Hg_element
FEATURE [App::DocumentObjectGroupPython] G4_Hg  # scripted group (container) (typed FeaturePython)
  Dunit = g/cm3
  Dvalue = 13.546
  Group = -> [Hg_element002]
  conduct = 2
  density = 1
  expand = 3
  formula = Hg
  name = G4_Hg
  specific = 4
FEATURE [App::DocumentObjectGroupPython] Tl_element002  label="Tl_element : 002"  # scripted group (container) (typed FeaturePython)
  n = 1
  ref = Tl_element
FEATURE [App::DocumentObjectGroupPython] G4_Tl  # scripted group (container) (typed FeaturePython)
  Dunit = g/cm3
  Dvalue = 11.72
  Group = -> [Tl_element002]
  conduct = 2
  density = 1
  expand = 3
  formula = Tl
  name = G4_Tl
  specific = 4
FEATURE [App::DocumentObjectGroupPython] Pb_element003  label="Pb_element : 1"  # scripted group (container) (typed FeaturePython)
  n = 1
  ref = Pb_element
FEATURE [App::DocumentObjectGroupPython] G4_Pb  # scripted group (container) (typed FeaturePython)
  Dunit = g/cm3
  Dvalue = 11.35
  Group = -> [Pb_element003]
  conduct = 2
  density = 1
  expand = 3
  formula = Pb
  name = G4_Pb
  specific = 4
FEATURE [App::DocumentObjectGroupPython] Bi_element002  label="Bi_element : 1"  # scripted group (container) (typed FeaturePython)
  n = 1
  ref = Bi_element
FEATURE [App::DocumentObjectGroupPython] G4_Bi  # scripted group (container) (typed FeaturePython)
  Dunit = g/cm3
  Dvalue = 9.747
  Group = -> [Bi_element002]
  conduct = 2
  density = 1
  expand = 3
  formula = Bi
  name = G4_Bi
  specific = 4
FEATURE [App::DocumentObjectGroupPython] Po_element001  label="Po_element : 1"  # scripted group (container) (typed FeaturePython)
  n = 1
  ref = Po_element
FEATURE [App::DocumentObjectGroupPython] G4_Po  # scripted group (container) (typed FeaturePython)
  Dunit = g/cm3
  Dvalue = 9.32
  Group = -> [Po_element001]
  conduct = 2
  density = 1
  expand = 3
  formula = Po
  name = G4_Po
  specific = 4
FEATURE [App::DocumentObjectGroupPython] At_element001  label="At_element : 1"  # scripted group (container) (typed FeaturePython)
  n = 1
  ref = At_element
FEATURE [App::DocumentObjectGroupPython] G4_At  # scripted group (container) (typed FeaturePython)
  Dunit = g/cm3
  Dvalue = 9.32
  Group = -> [At_element001]
  conduct = 2
  density = 1
  expand = 3
  formula = At
  name = G4_At
  specific = 4
FEATURE [App::DocumentObjectGroupPython] Rn_element001  label="Rn_element : 1"  # scripted group (container) (typed FeaturePython)
  n = 1
  ref = Rn_element
FEATURE [App::DocumentObjectGroupPython] G4_Rn  # scripted group (container) (typed FeaturePython)
  Dunit = g/cm3
  Dvalue = 0.00900662
  Group = -> [Rn_element001]
  conduct = 2
  density = 1
  expand = 3
  formula = Rn
  name = G4_Rn
  specific = 4
FEATURE [App::DocumentObjectGroupPython] Fr_element001  label="Fr_element : 1"  # scripted group (container) (typed FeaturePython)
  n = 1
  ref = Fr_element
FEATURE [App::DocumentObjectGroupPython] G4_Fr  # scripted group (container) (typed FeaturePython)
  Dunit = g/cm3
  Dvalue = 1
  Group = -> [Fr_element001]
  conduct = 2
  density = 1
  expand = 3
  formula = Fr
  name = G4_Fr
  specific = 4
FEATURE [App::DocumentObjectGroupPython] Ra_element001  label="Ra_element : 1"  # scripted group (container) (typed FeaturePython)
  n = 1
  ref = Ra_element
FEATURE [App::DocumentObjectGroupPython] G4_Ra  # scripted group (container) (typed FeaturePython)
  Dunit = g/cm3
  Dvalue = 5
  Group = -> [Ra_element001]
  conduct = 2
  density = 1
  expand = 3
  formula = Ra
  name = G4_Ra
  specific = 4
FEATURE [App::DocumentObjectGroupPython] Ac_element001  label="Ac_element : 1"  # scripted group (container) (typed FeaturePython)
  n = 1
  ref = Ac_element
FEATURE [App::DocumentObjectGroupPython] G4_Ac  # scripted group (container) (typed FeaturePython)
  Dunit = g/cm3
  Dvalue = 10.07
  Group = -> [Ac_element001]
  conduct = 2
  density = 1
  expand = 3
  formula = Ac
  name = G4_Ac
  specific = 4
FEATURE [App::DocumentObjectGroupPython] Th_element001  label="Th_element : 1"  # scripted group (container) (typed FeaturePython)
  n = 1
  ref = Th_element
FEATURE [App::DocumentObjectGroupPython] G4_Th  # scripted group (container) (typed FeaturePython)
  Dunit = g/cm3
  Dvalue = 11.72
  Group = -> [Th_element001]
  conduct = 2
  density = 1
  expand = 3
  formula = Th
  name = G4_Th
  specific = 4
FEATURE [App::DocumentObjectGroupPython] Pa_element001  label="Pa_element : 1"  # scripted group (container) (typed FeaturePython)
  n = 1
  ref = Pa_element
FEATURE [App::DocumentObjectGroupPython] G4_Pa  # scripted group (container) (typed FeaturePython)
  Dunit = g/cm3
  Dvalue = 15.37
  Group = -> [Pa_element001]
  conduct = 2
  density = 1
  expand = 3
  formula = Pa
  name = G4_Pa
  specific = 4
FEATURE [App::DocumentObjectGroupPython] U_element004  label="U_element : 004"  # scripted group (container) (typed FeaturePython)
  n = 1
  ref = U_element
FEATURE [App::DocumentObjectGroupPython] G4_U  # scripted group (container) (typed FeaturePython)
  Dunit = g/cm3
  Dvalue = 18.95
  Group = -> [U_element004]
  conduct = 2
  density = 1
  expand = 3
  formula = U
  name = G4_U
  specific = 4
FEATURE [App::DocumentObjectGroupPython] Np_element001  label="Np_element : 1"  # scripted group (container) (typed FeaturePython)
  n = 1
  ref = Np_element
FEATURE [App::DocumentObjectGroupPython] G4_Np  # scripted group (container) (typed FeaturePython)
  Dunit = g/cm3
  Dvalue = 20.25
  Group = -> [Np_element001]
  conduct = 2
  density = 1
  expand = 3
  formula = Np
  name = G4_Np
  specific = 4
FEATURE [App::DocumentObjectGroupPython] Pu_element002  label="Pu_element : 002"  # scripted group (container) (typed FeaturePython)
  n = 1
  ref = Pu_element
FEATURE [App::DocumentObjectGroupPython] G4_Pu  # scripted group (container) (typed FeaturePython)
  Dunit = g/cm3
  Dvalue = 19.84
  Group = -> [Pu_element002]
  conduct = 2
  density = 1
  expand = 3
  formula = Pu
  name = G4_Pu
  specific = 4
FEATURE [App::DocumentObjectGroupPython] Am_element001  label="Am_element : 1"  # scripted group (container) (typed FeaturePython)
  n = 1
  ref = Am_element
FEATURE [App::DocumentObjectGroupPython] G4_Am  # scripted group (container) (typed FeaturePython)
  Dunit = g/cm3
  Dvalue = 13.67
  Group = -> [Am_element001]
  conduct = 2
  density = 1
  expand = 3
  formula = Am
  name = G4_Am
  specific = 4
FEATURE [App::DocumentObjectGroupPython] Cm_element001  label="Cm_element : 1"  # scripted group (container) (typed FeaturePython)
  n = 1
  ref = Cm_element
FEATURE [App::DocumentObjectGroupPython] G4_Cm  # scripted group (container) (typed FeaturePython)
  Dunit = g/cm3
  Dvalue = 13.51
  Group = -> [Cm_element001]
  conduct = 2
  density = 1
  expand = 3
  formula = Cm
  name = G4_Cm
  specific = 4
FEATURE [App::DocumentObjectGroupPython] Bk_element001  label="Bk_element : 1"  # scripted group (container) (typed FeaturePython)
  n = 1
  ref = Bk_element
FEATURE [App::DocumentObjectGroupPython] G4_Bk  # scripted group (container) (typed FeaturePython)
  Dunit = g/cm3
  Dvalue = 14
  Group = -> [Bk_element001]
  conduct = 2
  density = 1
  expand = 3
  formula = Bk
  name = G4_Bk
  specific = 4
FEATURE [App::DocumentObjectGroupPython] Cf_element001  label="Cf_element : 1"  # scripted group (container) (typed FeaturePython)
  n = 1
  ref = Cf_element
FEATURE [App::DocumentObjectGroupPython] G4_Cf  # scripted group (container) (typed FeaturePython)
  Dunit = g/cm3
  Dvalue = 10
  Group = -> [Cf_element001]
  conduct = 2
  density = 1
  expand = 3
  formula = Cf
  name = G4_Cf
  specific = 4
FEATURE [App::DocumentObjectGroupPython] Element  # scripted group (container) (typed FeaturePython)
  Group = -> [G4_H,G4_He,G4_Li,G4_Be,G4_B,G4_C,G4_N,G4_O,G4_F,G4_Ne,G4_Na,G4_Mg,G4_Al,G4_Si,G4_P,G4_S,G4_Cl,G4_Ar,G4_K,G4_Ca,G4_Sc,G4_Ti,G4_V,G4_Cr,G4_Mn,G4_Fe,G4_Co,G4_Ni,G4_Cu,G4_Zn,G4_Ga,G4_Ge,G4_As,G4_Se,G4_Br,G4_Kr,G4_Rb,G4_Sr,G4_Y,G4_Zr,G4_Nb,G4_Mo,G4_Tc,G4_Ru,G4_Rh,G4_Pd,G4_Ag,G4_Cd,G4_In,G4_Sn,G4_Sb,G4_Te,G4_I,G4_Xe,G4_Cs,G4_Ba,G4_La,G4_Ce,G4_Pr,G4_Nd,G4_Pm,G4_Sm,G4_Eu,G4_Gd,G4_Tb,G4_Dy,G4_Ho,G4_Er,+30 more]
FEATURE [App::DocumentObjectGroupPython] H_element114  label="H_element : 063"  # scripted group (container) (typed FeaturePython)
  n = 2
  ref = H_element
FEATURE [App::DocumentObjectGroupPython] G4_lH2  # scripted group (container) (typed FeaturePython)
  Dunit = g/cm3
  Dvalue = 0.0708
  Group = -> [H_element114]
  conduct = 2
  density = 1
  expand = 3
  formula = G4_lH2
  name = G4_lH2
  specific = 4
FEATURE [App::DocumentObjectGroupPython] N_element049  label="N_element : 022"  # scripted group (container) (typed FeaturePython)
  n = 2
  ref = N_element
FEATURE [App::DocumentObjectGroupPython] G4_lN2  # scripted group (container) (typed FeaturePython)
  Dunit = g/cm3
  Dvalue = 0.807
  Group = -> [N_element049]
  conduct = 2
  density = 1
  expand = 3
  formula = G4_lN2
  name = G4_lN2
  specific = 4
FEATURE [App::DocumentObjectGroupPython] O_element106  label="O_element : 060"  # scripted group (container) (typed FeaturePython)
  n = 2
  ref = O_element
FEATURE [App::DocumentObjectGroupPython] G4_lO2  # scripted group (container) (typed FeaturePython)
  Dunit = g/cm3
  Dvalue = 1.141
  Group = -> [O_element106]
  conduct = 2
  density = 1
  expand = 3
  formula = G4_lO2
  name = G4_lO2
  specific = 4
FEATURE [App::DocumentObjectGroupPython] Ar_element003  label="Ar_element : 002"  # scripted group (container) (typed FeaturePython)
  n = 1
  ref = Ar_element
FEATURE [App::DocumentObjectGroupPython] G4_lAr  # scripted group (container) (typed FeaturePython)
  Dunit = g/cm3
  Dvalue = 1.396
  Group = -> [Ar_element003]
  conduct = 2
  density = 1
  expand = 3
  formula = G4_lAr
  name = G4_lAr
  specific = 4
FEATURE [App::DocumentObjectGroupPython] Br_element008  label="Br_element : 005"  # scripted group (container) (typed FeaturePython)
  n = 1
  ref = Br_element
FEATURE [App::DocumentObjectGroupPython] G4_lBr  # scripted group (container) (typed FeaturePython)
  Dunit = g/cm3
  Dvalue = 3.1028
  Group = -> [Br_element008]
  conduct = 2
  density = 1
  expand = 3
  formula = G4_lBr
  name = G4_lBr
  specific = 4
FEATURE [App::DocumentObjectGroupPython] Kr_element002  label="Kr_element : 002"  # scripted group (container) (typed FeaturePython)
  n = 1
  ref = Kr_element
FEATURE [App::DocumentObjectGroupPython] G4_lKr  # scripted group (container) (typed FeaturePython)
  Dunit = g/cm3
  Dvalue = 2.418
  Group = -> [Kr_element002]
  conduct = 2
  density = 1
  expand = 3
  formula = G4_lKr
  name = G4_lKr
  specific = 4
FEATURE [App::DocumentObjectGroupPython] Xe_element002  label="Xe_element : 002"  # scripted group (container) (typed FeaturePython)
  n = 1
  ref = Xe_element
FEATURE [App::DocumentObjectGroupPython] G4_lXe  # scripted group (container) (typed FeaturePython)
  Dunit = g/cm3
  Dvalue = 2.953
  Group = -> [Xe_element002]
  conduct = 2
  density = 1
  expand = 3
  formula = G4_lXe
  name = G4_lXe
  specific = 4
FEATURE [App::DocumentObjectGroupPython] O_element107  label="O_element : 061"  # scripted group (container) (typed FeaturePython)
  n = 4
  ref = O_element
FEATURE [App::DocumentObjectGroupPython] Pb_element004  label="Pb_element : 002"  # scripted group (container) (typed FeaturePython)
  n = 1
  ref = Pb_element
FEATURE [App::DocumentObjectGroupPython] W_element005  label="W_element : 005"  # scripted group (container) (typed FeaturePython)
  n = 1
  ref = W_element
FEATURE [App::DocumentObjectGroupPython] G4_PbWO4  # scripted group (container) (typed FeaturePython)
  Dunit = g/cm3
  Dvalue = 8.28
  Group = -> [O_element107,Pb_element004,W_element005]
  conduct = 2
  density = 1
  expand = 3
  formula = G4_PbWO4
  name = G4_PbWO4
  specific = 4
FEATURE [App::DocumentObjectGroupPython] H_element115  label="H_element : 064"  # scripted group (container) (typed FeaturePython)
  n = 1
  ref = H_element
FEATURE [App::DocumentObjectGroupPython] G4_Galactic  # scripted group (container) (typed FeaturePython)
  Dunit = g/cm3
  Dvalue = 0
  Group = -> [H_element115]
  conduct = 2
  density = 1
  expand = 3
  formula = G4_Galactic
  name = G4_Galactic
  specific = 4
FEATURE [App::DocumentObjectGroupPython] C_element125  label="C_element : 071"  # scripted group (container) (typed FeaturePython)
  n = 1
  ref = C_element
FEATURE [App::DocumentObjectGroupPython] G4_GRAPHITE_POROUS  # scripted group (container) (typed FeaturePython)
  Dunit = g/cm3
  Dvalue = 1.7
  Group = -> [C_element125]
  conduct = 2
  density = 1
  expand = 3
  formula = G4_GRAPHITE_POROUS
  name = G4_GRAPHITE_POROUS
  specific = 4
FEATURE [App::DocumentObjectGroupPython] H_element116  label="H_element : 0.150"  # scripted group (container) (typed FeaturePython)
  n = 0.080538
FEATURE [App::DocumentObjectGroupPython] C_element126  label="C_element : 0.600"  # scripted group (container) (typed FeaturePython)
  n = 0.599848
FEATURE [App::DocumentObjectGroupPython] O_element108  label="O_element : 0.320"  # scripted group (container) (typed FeaturePython)
  n = 0.319614
FEATURE [App::DocumentObjectGroupPython] G4_LUCITE  # scripted group (container) (typed FeaturePython)
  Dunit = g/cm3
  Dvalue = 1.19
  Group = -> [H_element116,C_element126,O_element108]
  conduct = 2
  density = 1
  expand = 3
  formula = G4_LUCITE
  name = G4_LUCITE
  specific = 4
FEATURE [App::DocumentObjectGroupPython] Cu_element002  label="Cu_element : 62"  # scripted group (container) (typed FeaturePython)
  n = 62
  ref = Cu_element
FEATURE [App::DocumentObjectGroupPython] Zn_element002  label="Zn_element : 35"  # scripted group (container) (typed FeaturePython)
  n = 35
  ref = Zn_element
FEATURE [App::DocumentObjectGroupPython] Pb_element005  label="Pb_element : 3"  # scripted group (container) (typed FeaturePython)
  n = 3
  ref = Pb_element
FEATURE [App::DocumentObjectGroupPython] G4_BRASS  # scripted group (container) (typed FeaturePython)
  Dunit = g/cm3
  Dvalue = 8.52
  Group = -> [Cu_element002,Zn_element002,Pb_element005]
  conduct = 2
  density = 1
  expand = 3
  formula = G4_BRASS
  name = G4_BRASS
  specific = 4
FEATURE [App::DocumentObjectGroupPython] Cu_element003  label="Cu_element : 89"  # scripted group (container) (typed FeaturePython)
  n = 89
  ref = Cu_element
FEATURE [App::DocumentObjectGroupPython] Zn_element003  label="Zn_element : 9"  # scripted group (container) (typed FeaturePython)
  n = 9
  ref = Zn_element
FEATURE [App::DocumentObjectGroupPython] Pb_element006  label="Pb_element : 2"  # scripted group (container) (typed FeaturePython)
  n = 2
  ref = Pb_element
FEATURE [App::DocumentObjectGroupPython] G4_BRONZE  # scripted group (container) (typed FeaturePython)
  Dunit = g/cm3
  Dvalue = 8.82
  Group = -> [Cu_element003,Zn_element003,Pb_element006]
  conduct = 2
  density = 1
  expand = 3
  formula = G4_BRONZE
  name = G4_BRONZE
  specific = 4
FEATURE [App::DocumentObjectGroupPython] Fe_element008  label="Fe_element : 74"  # scripted group (container) (typed FeaturePython)
  n = 74
  ref = Fe_element
FEATURE [App::DocumentObjectGroupPython] Cr_element002  label="Cr_element : 18"  # scripted group (container) (typed FeaturePython)
  n = 18
  ref = Cr_element
FEATURE [App::DocumentObjectGroupPython] Ni_element002  label="Ni_element : 8"  # scripted group (container) (typed FeaturePython)
  n = 8
  ref = Ni_element
FEATURE [App::DocumentObjectGroupPython] G4_STAINLESS_STEEL  label="G4_STAINLESS-STEEL"  # scripted group (container) (typed FeaturePython)
  Dunit = g/cm3
  Dvalue = 8
  Group = -> [Fe_element008,Cr_element002,Ni_element002]
  conduct = 2
  density = 1
  expand = 3
  formula = G4_STAINLESS-STEEL
  name = G4_STAINLESS-STEEL
  specific = 4
FEATURE [App::DocumentObjectGroupPython] H_element117  label="H_element : 065"  # scripted group (container) (typed FeaturePython)
  n = 18
  ref = H_element
FEATURE [App::DocumentObjectGroupPython] C_element127  label="C_element : 072"  # scripted group (container) (typed FeaturePython)
  n = 12
  ref = C_element
FEATURE [App::DocumentObjectGroupPython] O_element109  label="O_element : 062"  # scripted group (container) (typed FeaturePython)
  n = 7
  ref = O_element
FEATURE [App::DocumentObjectGroupPython] G4_CR39  # scripted group (container) (typed FeaturePython)
  Dunit = g/cm3
  Dvalue = 1.32
  Group = -> [H_element117,C_element127,O_element109]
  conduct = 2
  density = 1
  expand = 3
  formula = G4_CR39
  name = G4_CR39
  specific = 4
FEATURE [App::DocumentObjectGroupPython] H_element118  label="H_element : 38"  # scripted group (container) (typed FeaturePython)
  n = 38
  ref = H_element
FEATURE [App::DocumentObjectGroupPython] C_element128  label="C_element : 073"  # scripted group (container) (typed FeaturePython)
  n = 18
  ref = C_element
FEATURE [App::DocumentObjectGroupPython] O_element110  label="O_element : 063"  # scripted group (container) (typed FeaturePython)
  n = 1
  ref = O_element
FEATURE [App::DocumentObjectGroupPython] G4_OCTADECANOL  # scripted group (container) (typed FeaturePython)
  Dunit = g/cm3
  Dvalue = 0.812
  Group = -> [H_element118,C_element128,O_element110]
  conduct = 2
  density = 1
  expand = 3
  formula = G4_OCTADECANOL
  name = G4_OCTADECANOL
  specific = 4
FEATURE [App::DocumentObjectGroupPython] HEP  # scripted group (container) (typed FeaturePython)
  Group = -> [G4_lH2,G4_lN2,G4_lO2,G4_lAr,G4_lBr,G4_lKr,G4_lXe,G4_PbWO4,G4_Galactic,G4_GRAPHITE_POROUS,G4_LUCITE,G4_BRASS,G4_BRONZE,G4_STAINLESS_STEEL,G4_CR39,G4_OCTADECANOL]
FEATURE [App::DocumentObjectGroupPython] C_element129  label="C_element : 074"  # scripted group (container) (typed FeaturePython)
  n = 14
  ref = C_element
FEATURE [App::DocumentObjectGroupPython] H_element119  label="H_element : 066"  # scripted group (container) (typed FeaturePython)
  n = 10
  ref = H_element
FEATURE [App::DocumentObjectGroupPython] O_element111  label="O_element : 064"  # scripted group (container) (typed FeaturePython)
  n = 2
  ref = O_element
FEATURE [App::DocumentObjectGroupPython] N_element050  label="N_element : 023"  # scripted group (container) (typed FeaturePython)
  n = 2
  ref = N_element
FEATURE [App::DocumentObjectGroupPython] G4_KEVLAR  # scripted group (container) (typed FeaturePython)
  Dunit = g/cm3
  Dvalue = 1.44
  Group = -> [C_element129,H_element119,O_element111,N_element050]
  conduct = 2
  density = 1
  expand = 3
  formula = G4_KEVLAR
  name = G4_KEVLAR
  specific = 4
FEATURE [App::DocumentObjectGroupPython] C_element130  label="C_element : 075"  # scripted group (container) (typed FeaturePython)
  n = 10
  ref = C_element
FEATURE [App::DocumentObjectGroupPython] H_element120  label="H_element : 067"  # scripted group (container) (typed FeaturePython)
  n = 8
  ref = H_element
FEATURE [App::DocumentObjectGroupPython] O_element112  label="O_element : 065"  # scripted group (container) (typed FeaturePython)
  n = 4
  ref = O_element
FEATURE [App::DocumentObjectGroupPython] G4_DACRON  # scripted group (container) (typed FeaturePython)
  Dunit = g/cm3
  Dvalue = 1.4
  Group = -> [C_element130,H_element120,O_element112]
  conduct = 2
  density = 1
  expand = 3
  formula = G4_DACRON
  name = G4_DACRON
  specific = 4
FEATURE [App::DocumentObjectGroupPython] C_element131  label="C_element : 076"  # scripted group (container) (typed FeaturePython)
  n = 4
  ref = C_element
FEATURE [App::DocumentObjectGroupPython] H_element121  label="H_element : 068"  # scripted group (container) (typed FeaturePython)
  n = 5
  ref = H_element
FEATURE [App::DocumentObjectGroupPython] Cl_element030  label="Cl_element : 016"  # scripted group (container) (typed FeaturePython)
  n = 1
  ref = Cl_element
FEATURE [App::DocumentObjectGroupPython] G4_NEOPRENE  # scripted group (container) (typed FeaturePython)
  Dunit = g/cm3
  Dvalue = 1.23
  Group = -> [C_element131,H_element121,Cl_element030]
  conduct = 2
  density = 1
  expand = 3
  formula = G4_NEOPRENE
  name = G4_NEOPRENE
  specific = 4
FEATURE [App::DocumentObjectGroupPython] Space  # scripted group (container) (typed FeaturePython)
  Group = -> [G4_KEVLAR,G4_DACRON,G4_NEOPRENE]
FEATURE [App::DocumentObjectGroupPython] H_element122  label="H_element : 069"  # scripted group (container) (typed FeaturePython)
  n = 5
  ref = H_element
FEATURE [App::DocumentObjectGroupPython] C_element132  label="C_element : 077"  # scripted group (container) (typed FeaturePython)
  n = 4
  ref = C_element
FEATURE [App::DocumentObjectGroupPython] N_element051  label="N_element : 3"  # scripted group (container) (typed FeaturePython)
  n = 3
  ref = N_element
FEATURE [App::DocumentObjectGroupPython] O_element113  label="O_element : 066"  # scripted group (container) (typed FeaturePython)
  n = 1
  ref = O_element
FEATURE [App::DocumentObjectGroupPython] G4_CYTOSINE  # scripted group (container) (typed FeaturePython)
  Dunit = g/cm3
  Dvalue = 1.55
  Group = -> [H_element122,C_element132,N_element051,O_element113]
  conduct = 2
  density = 1
  expand = 3
  formula = G4_CYTOSINE
  name = G4_CYTOSINE
  specific = 4
FEATURE [App::DocumentObjectGroupPython] H_element123  label="H_element : 070"  # scripted group (container) (typed FeaturePython)
  n = 6
  ref = H_element
FEATURE [App::DocumentObjectGroupPython] C_element133  label="C_element : 078"  # scripted group (container) (typed FeaturePython)
  n = 5
  ref = C_element
FEATURE [App::DocumentObjectGroupPython] N_element052  label="N_element : 024"  # scripted group (container) (typed FeaturePython)
  n = 2
  ref = N_element
FEATURE [App::DocumentObjectGroupPython] O_element114  label="O_element : 067"  # scripted group (container) (typed FeaturePython)
  n = 2
  ref = O_element
FEATURE [App::DocumentObjectGroupPython] G4_THYMINE  # scripted group (container) (typed FeaturePython)
  Dunit = g/cm3
  Dvalue = 1.23
  Group = -> [H_element123,C_element133,N_element052,O_element114]
  conduct = 2
  density = 1
  expand = 3
  formula = G4_THYMINE
  name = G4_THYMINE
  specific = 4
FEATURE [App::DocumentObjectGroupPython] H_element124  label="H_element : 071"  # scripted group (container) (typed FeaturePython)
  n = 4
  ref = H_element
FEATURE [App::DocumentObjectGroupPython] C_element134  label="C_element : 079"  # scripted group (container) (typed FeaturePython)
  n = 4
  ref = C_element
FEATURE [App::DocumentObjectGroupPython] N_element053  label="N_element : 025"  # scripted group (container) (typed FeaturePython)
  n = 2
  ref = N_element
FEATURE [App::DocumentObjectGroupPython] O_element115  label="O_element : 068"  # scripted group (container) (typed FeaturePython)
  n = 2
  ref = O_element
FEATURE [App::DocumentObjectGroupPython] G4_URACIL  # scripted group (container) (typed FeaturePython)
  Dunit = g/cm3
  Dvalue = 1.32
  Group = -> [H_element124,C_element134,N_element053,O_element115]
  conduct = 2
  density = 1
  expand = 3
  formula = G4_URACIL
  name = G4_URACIL
  specific = 4
FEATURE [App::DocumentObjectGroupPython] H_element125  label="H_element : 072"  # scripted group (container) (typed FeaturePython)
  n = 4
  ref = H_element
FEATURE [App::DocumentObjectGroupPython] C_element135  label="C_element : 080"  # scripted group (container) (typed FeaturePython)
  n = 5
  ref = C_element
FEATURE [App::DocumentObjectGroupPython] N_element054  label="N_element : 026"  # scripted group (container) (typed FeaturePython)
  n = 5
  ref = N_element
FEATURE [App::DocumentObjectGroupPython] G4_DNA_ADENINE  # scripted group (container) (typed FeaturePython)
  Dunit = g/cm3
  Dvalue = 1
  Group = -> [H_element125,C_element135,N_element054]
  conduct = 2
  density = 1
  expand = 3
  formula = G4_DNA_ADENINE
  name = G4_DNA_ADENINE
  specific = 4
FEATURE [App::DocumentObjectGroupPython] H_element126  label="H_element : 073"  # scripted group (container) (typed FeaturePython)
  n = 4
  ref = H_element
FEATURE [App::DocumentObjectGroupPython] C_element136  label="C_element : 081"  # scripted group (container) (typed FeaturePython)
  n = 5
  ref = C_element
FEATURE [App::DocumentObjectGroupPython] N_element055  label="N_element : 027"  # scripted group (container) (typed FeaturePython)
  n = 5
  ref = N_element
FEATURE [App::DocumentObjectGroupPython] O_element116  label="O_element : 069"  # scripted group (container) (typed FeaturePython)
  n = 1
  ref = O_element
FEATURE [App::DocumentObjectGroupPython] G4_DNA_GUANINE  # scripted group (container) (typed FeaturePython)
  Dunit = g/cm3
  Dvalue = 1
  Group = -> [H_element126,C_element136,N_element055,O_element116]
  conduct = 2
  density = 1
  expand = 3
  formula = G4_DNA_GUANINE
  name = G4_DNA_GUANINE
  specific = 4
FEATURE [App::DocumentObjectGroupPython] H_element127  label="H_element : 074"  # scripted group (container) (typed FeaturePython)
  n = 4
  ref = H_element
FEATURE [App::DocumentObjectGroupPython] C_element137  label="C_element : 082"  # scripted group (container) (typed FeaturePython)
  n = 4
  ref = C_element
FEATURE [App::DocumentObjectGroupPython] N_element056  label="N_element : 028"  # scripted group (container) (typed FeaturePython)
  n = 3
  ref = N_element
FEATURE [App::DocumentObjectGroupPython] O_element117  label="O_element : 070"  # scripted group (container) (typed FeaturePython)
  n = 1
  ref = O_element
FEATURE [App::DocumentObjectGroupPython] G4_DNA_CYTOSINE  # scripted group (container) (typed FeaturePython)
  Dunit = g/cm3
  Dvalue = 1
  Group = -> [H_element127,C_element137,N_element056,O_element117]
  conduct = 2
  density = 1
  expand = 3
  formula = G4_DNA_CYTOSINE
  name = G4_DNA_CYTOSINE
  specific = 4
FEATURE [App::DocumentObjectGroupPython] H_element128  label="H_element : 075"  # scripted group (container) (typed FeaturePython)
  n = 5
  ref = H_element
FEATURE [App::DocumentObjectGroupPython] C_element138  label="C_element : 083"  # scripted group (container) (typed FeaturePython)
  n = 5
  ref = C_element
FEATURE [App::DocumentObjectGroupPython] N_element057  label="N_element : 029"  # scripted group (container) (typed FeaturePython)
  n = 2
  ref = N_element
FEATURE [App::DocumentObjectGroupPython] O_element118  label="O_element : 071"  # scripted group (container) (typed FeaturePython)
  n = 2
  ref = O_element
FEATURE [App::DocumentObjectGroupPython] G4_DNA_THYMINE  # scripted group (container) (typed FeaturePython)
  Dunit = g/cm3
  Dvalue = 1
  Group = -> [H_element128,C_element138,N_element057,O_element118]
  conduct = 2
  density = 1
  expand = 3
  formula = G4_DNA_THYMINE
  name = G4_DNA_THYMINE
  specific = 4
FEATURE [App::DocumentObjectGroupPython] H_element129  label="H_element : 076"  # scripted group (container) (typed FeaturePython)
  n = 3
  ref = H_element
FEATURE [App::DocumentObjectGroupPython] C_element139  label="C_element : 084"  # scripted group (container) (typed FeaturePython)
  n = 4
  ref = C_element
FEATURE [App::DocumentObjectGroupPython] N_element058  label="N_element : 030"  # scripted group (container) (typed FeaturePython)
  n = 2
  ref = N_element
FEATURE [App::DocumentObjectGroupPython] O_element119  label="O_element : 072"  # scripted group (container) (typed FeaturePython)
  n = 2
  ref = O_element
FEATURE [App::DocumentObjectGroupPython] G4_DNA_URACIL  # scripted group (container) (typed FeaturePython)
  Dunit = g/cm3
  Dvalue = 1
  Group = -> [H_element129,C_element139,N_element058,O_element119]
  conduct = 2
  density = 1
  expand = 3
  formula = G4_DNA_URACIL
  name = G4_DNA_URACIL
  specific = 4
FEATURE [App::DocumentObjectGroupPython] H_element130  label="H_element : 077"  # scripted group (container) (typed FeaturePython)
  n = 10
  ref = H_element
FEATURE [App::DocumentObjectGroupPython] C_element140  label="C_element : 085"  # scripted group (container) (typed FeaturePython)
  n = 10
  ref = C_element
FEATURE [App::DocumentObjectGroupPython] N_element059  label="N_element : 031"  # scripted group (container) (typed FeaturePython)
  n = 5
  ref = N_element
FEATURE [App::DocumentObjectGroupPython] O_element120  label="O_element : 073"  # scripted group (container) (typed FeaturePython)
  n = 4
  ref = O_element
FEATURE [App::DocumentObjectGroupPython] G4_DNA_ADENOSINE  # scripted group (container) (typed FeaturePython)
  Dunit = g/cm3
  Dvalue = 1
  Group = -> [H_element130,C_element140,N_element059,O_element120]
  conduct = 2
  density = 1
  expand = 3
  formula = G4_DNA_ADENOSINE
  name = G4_DNA_ADENOSINE
  specific = 4
FEATURE [App::DocumentObjectGroupPython] H_element131  label="H_element : 078"  # scripted group (container) (typed FeaturePython)
  n = 10
  ref = H_element
FEATURE [App::DocumentObjectGroupPython] C_element141  label="C_element : 086"  # scripted group (container) (typed FeaturePython)
  n = 10
  ref = C_element
FEATURE [App::DocumentObjectGroupPython] N_element060  label="N_element : 032"  # scripted group (container) (typed FeaturePython)
  n = 5
  ref = N_element
FEATURE [App::DocumentObjectGroupPython] O_element121  label="O_element : 074"  # scripted group (container) (typed FeaturePython)
  n = 5
  ref = O_element
FEATURE [App::DocumentObjectGroupPython] G4_DNA_GUANOSINE  # scripted group (container) (typed FeaturePython)
  Dunit = g/cm3
  Dvalue = 1
  Group = -> [H_element131,C_element141,N_element060,O_element121]
  conduct = 2
  density = 1
  expand = 3
  formula = G4_DNA_GUANOSINE
  name = G4_DNA_GUANOSINE
  specific = 4
FEATURE [App::DocumentObjectGroupPython] H_element132  label="H_element : 079"  # scripted group (container) (typed FeaturePython)
  n = 10
  ref = H_element
FEATURE [App::DocumentObjectGroupPython] C_element142  label="C_element : 087"  # scripted group (container) (typed FeaturePython)
  n = 9
  ref = C_element
FEATURE [App::DocumentObjectGroupPython] N_element061  label="N_element : 033"  # scripted group (container) (typed FeaturePython)
  n = 3
  ref = N_element
FEATURE [App::DocumentObjectGroupPython] O_element122  label="O_element : 075"  # scripted group (container) (typed FeaturePython)
  n = 5
  ref = O_element
FEATURE [App::DocumentObjectGroupPython] G4_DNA_CYTIDINE  # scripted group (container) (typed FeaturePython)
  Dunit = g/cm3
  Dvalue = 1
  Group = -> [H_element132,C_element142,N_element061,O_element122]
  conduct = 2
  density = 1
  expand = 3
  formula = G4_DNA_CYTIDINE
  name = G4_DNA_CYTIDINE
  specific = 4
FEATURE [App::DocumentObjectGroupPython] H_element133  label="H_element : 080"  # scripted group (container) (typed FeaturePython)
  n = 9
  ref = H_element
FEATURE [App::DocumentObjectGroupPython] C_element143  label="C_element : 088"  # scripted group (container) (typed FeaturePython)
  n = 9
  ref = C_element
FEATURE [App::DocumentObjectGroupPython] N_element062  label="N_element : 034"  # scripted group (container) (typed FeaturePython)
  n = 2
  ref = N_element
FEATURE [App::DocumentObjectGroupPython] O_element123  label="O_element : 076"  # scripted group (container) (typed FeaturePython)
  n = 6
  ref = O_element
FEATURE [App::DocumentObjectGroupPython] G4_DNA_URIDINE  # scripted group (container) (typed FeaturePython)
  Dunit = g/cm3
  Dvalue = 1
  Group = -> [H_element133,C_element143,N_element062,O_element123]
  conduct = 2
  density = 1
  expand = 3
  formula = G4_DNA_URIDINE
  name = G4_DNA_URIDINE
  specific = 4
FEATURE [App::DocumentObjectGroupPython] H_element134  label="H_element : 081"  # scripted group (container) (typed FeaturePython)
  n = 11
  ref = H_element
FEATURE [App::DocumentObjectGroupPython] C_element144  label="C_element : 089"  # scripted group (container) (typed FeaturePython)
  n = 10
  ref = C_element
FEATURE [App::DocumentObjectGroupPython] N_element063  label="N_element : 035"  # scripted group (container) (typed FeaturePython)
  n = 2
  ref = N_element
FEATURE [App::DocumentObjectGroupPython] O_element124  label="O_element : 077"  # scripted group (container) (typed FeaturePython)
  n = 6
  ref = O_element
FEATURE [App::DocumentObjectGroupPython] G4_DNA_METHYLURIDINE  # scripted group (container) (typed FeaturePython)
  Dunit = g/cm3
  Dvalue = 1
  Group = -> [H_element134,C_element144,N_element063,O_element124]
  conduct = 2
  density = 1
  expand = 3
  formula = G4_DNA_METHYLURIDINE
  name = G4_DNA_METHYLURIDINE
  specific = 4
FEATURE [App::DocumentObjectGroupPython] P_element014  label="P_element : 003"  # scripted group (container) (typed FeaturePython)
  n = 1
  ref = P_element
FEATURE [App::DocumentObjectGroupPython] O_element125  label="O_element : 078"  # scripted group (container) (typed FeaturePython)
  n = 3
  ref = O_element
FEATURE [App::DocumentObjectGroupPython] G4_DNA_MONOPHOSPHATE  # scripted group (container) (typed FeaturePython)
  Dunit = g/cm3
  Dvalue = 1
  Group = -> [P_element014,O_element125]
  conduct = 2
  density = 1
  expand = 3
  formula = G4_DNA_MONOPHOSPHATE
  name = G4_DNA_MONOPHOSPHATE
  specific = 4
FEATURE [App::DocumentObjectGroupPython] H_element135  label="H_element : 082"  # scripted group (container) (typed FeaturePython)
  n = 10
  ref = H_element
FEATURE [App::DocumentObjectGroupPython] C_element145  label="C_element : 090"  # scripted group (container) (typed FeaturePython)
  n = 10
  ref = C_element
FEATURE [App::DocumentObjectGroupPython] N_element064  label="N_element : 036"  # scripted group (container) (typed FeaturePython)
  n = 5
  ref = N_element
FEATURE [App::DocumentObjectGroupPython] O_element126  label="O_element : 079"  # scripted group (container) (typed FeaturePython)
  n = 7
  ref = O_element
FEATURE [App::DocumentObjectGroupPython] P_element015  label="P_element : 004"  # scripted group (container) (typed FeaturePython)
  n = 1
  ref = P_element
FEATURE [App::DocumentObjectGroupPython] G4_DNA_A  # scripted group (container) (typed FeaturePython)
  Dunit = g/cm3
  Dvalue = 1
  Group = -> [H_element135,C_element145,N_element064,O_element126,P_element015]
  conduct = 2
  density = 1
  expand = 3
  formula = G4_DNA_A
  name = G4_DNA_A
  specific = 4
FEATURE [App::DocumentObjectGroupPython] H_element136  label="H_element : 083"  # scripted group (container) (typed FeaturePython)
  n = 10
  ref = H_element
FEATURE [App::DocumentObjectGroupPython] C_element146  label="C_element : 091"  # scripted group (container) (typed FeaturePython)
  n = 10
  ref = C_element
FEATURE [App::DocumentObjectGroupPython] N_element065  label="N_element : 037"  # scripted group (container) (typed FeaturePython)
  n = 5
  ref = N_element
FEATURE [App::DocumentObjectGroupPython] O_element127  label="O_element : 8"  # scripted group (container) (typed FeaturePython)
  n = 8
  ref = O_element
FEATURE [App::DocumentObjectGroupPython] P_element016  label="P_element : 005"  # scripted group (container) (typed FeaturePython)
  n = 1
  ref = P_element
FEATURE [App::DocumentObjectGroupPython] G4_DNA_G  # scripted group (container) (typed FeaturePython)
  Dunit = g/cm3
  Dvalue = 1
  Group = -> [H_element136,C_element146,N_element065,O_element127,P_element016]
  conduct = 2
  density = 1
  expand = 3
  formula = G4_DNA_G
  name = G4_DNA_G
  specific = 4
FEATURE [App::DocumentObjectGroupPython] H_element137  label="H_element : 084"  # scripted group (container) (typed FeaturePython)
  n = 10
  ref = H_element
FEATURE [App::DocumentObjectGroupPython] C_element147  label="C_element : 092"  # scripted group (container) (typed FeaturePython)
  n = 9
  ref = C_element
FEATURE [App::DocumentObjectGroupPython] N_element066  label="N_element : 038"  # scripted group (container) (typed FeaturePython)
  n = 3
  ref = N_element
FEATURE [App::DocumentObjectGroupPython] O_element128  label="O_element : 080"  # scripted group (container) (typed FeaturePython)
  n = 8
  ref = O_element
FEATURE [App::DocumentObjectGroupPython] P_element017  label="P_element : 006"  # scripted group (container) (typed FeaturePython)
  n = 1
  ref = P_element
FEATURE [App::DocumentObjectGroupPython] G4_DNA_C  # scripted group (container) (typed FeaturePython)
  Dunit = g/cm3
  Dvalue = 1
  Group = -> [H_element137,C_element147,N_element066,O_element128,P_element017]
  conduct = 2
  density = 1
  expand = 3
  formula = G4_DNA_C
  name = G4_DNA_C
  specific = 4
FEATURE [App::DocumentObjectGroupPython] H_element138  label="H_element : 085"  # scripted group (container) (typed FeaturePython)
  n = 9
  ref = H_element
FEATURE [App::DocumentObjectGroupPython] C_element148  label="C_element : 093"  # scripted group (container) (typed FeaturePython)
  n = 9
  ref = C_element
FEATURE [App::DocumentObjectGroupPython] N_element067  label="N_element : 039"  # scripted group (container) (typed FeaturePython)
  n = 2
  ref = N_element
FEATURE [App::DocumentObjectGroupPython] O_element129  label="O_element : 9"  # scripted group (container) (typed FeaturePython)
  n = 9
  ref = O_element
FEATURE [App::DocumentObjectGroupPython] P_element018  label="P_element : 007"  # scripted group (container) (typed FeaturePython)
  n = 1
  ref = P_element
FEATURE [App::DocumentObjectGroupPython] G4_DNA_U  # scripted group (container) (typed FeaturePython)
  Dunit = g/cm3
  Dvalue = 1
  Group = -> [H_element138,C_element148,N_element067,O_element129,P_element018]
  conduct = 2
  density = 1
  expand = 3
  formula = G4_DNA_U
  name = G4_DNA_U
  specific = 4
FEATURE [App::DocumentObjectGroupPython] H_element139  label="H_element : 086"  # scripted group (container) (typed FeaturePython)
  n = 11
  ref = H_element
FEATURE [App::DocumentObjectGroupPython] C_element149  label="C_element : 094"  # scripted group (container) (typed FeaturePython)
  n = 10
  ref = C_element
FEATURE [App::DocumentObjectGroupPython] N_element068  label="N_element : 040"  # scripted group (container) (typed FeaturePython)
  n = 2
  ref = N_element
FEATURE [App::DocumentObjectGroupPython] O_element130  label="O_element : 081"  # scripted group (container) (typed FeaturePython)
  n = 9
  ref = O_element
FEATURE [App::DocumentObjectGroupPython] P_element019  label="P_element : 008"  # scripted group (container) (typed FeaturePython)
  n = 1
  ref = P_element
FEATURE [App::DocumentObjectGroupPython] G4_DNA_MU  # scripted group (container) (typed FeaturePython)
  Dunit = g/cm3
  Dvalue = 1
  Group = -> [H_element139,C_element149,N_element068,O_element130,P_element019]
  conduct = 2
  density = 1
  expand = 3
  formula = G4_DNA_MU
  name = G4_DNA_MU
  specific = 4
FEATURE [App::DocumentObjectGroupPython] BioChemical  # scripted group (container) (typed FeaturePython)
  Group = -> [G4_CYTOSINE,G4_THYMINE,G4_URACIL,G4_DNA_ADENINE,G4_DNA_GUANINE,G4_DNA_CYTOSINE,G4_DNA_THYMINE,G4_DNA_URACIL,G4_DNA_ADENOSINE,G4_DNA_GUANOSINE,G4_DNA_CYTIDINE,G4_DNA_URIDINE,G4_DNA_METHYLURIDINE,G4_DNA_MONOPHOSPHATE,G4_DNA_A,G4_DNA_G,G4_DNA_C,G4_DNA_U,G4_DNA_MU]
FEATURE [App::DocumentObjectGroupPython] G4Materials  # scripted group (container) (typed FeaturePython)
  Group = -> [NIST,Element,HEP,Space,BioChemical]
  version = 1
FEATURE [App::DocumentObjectGroupPython] Geant4  # scripted group (container) (typed FeaturePython)
  Group = -> [G4Isotopes,G4Elements,G4Materials]
FEATURE [App::DocumentObjectGroupPython] Materials  # scripted group (container) (typed FeaturePython)
  Group = -> [Geant4]
FEATURE [Part::FeaturePython] GDMLBox_WorldBox  # WARN: FeaturePython — macro-defined, semantics opaque (R4)
  lunit = 2
  material = 5
  x = 403
  y = 429
  z = 130
FEATURE [Part::FeaturePython] GDMLBox_Box  # WARN: FeaturePython — macro-defined, semantics opaque (R4)
  Placement = pos=(30,0,0) rot=(0,0,1;0rad)
  lunit = 2
  material = 0
  x = 10
  y = 10
  z = 10
FEATURE [Part::FeaturePython] GDMLTorus  # WARN: FeaturePython — macro-defined, semantics opaque (R4)
  Placement = pos=(30,0,0) rot=(0,1,0;1.5708rad)
  aunit = deg
  deltaphi = 360
  lunit = 2
  material = 0
  rmax = 2
  rmin = 0
  rtor = 8
  startphi = 0
FEATURE [Part::MultiFuse] Fusion
  Shapes = -> [GDMLBox_Box,GDMLTorus]
FEATURE [Part::FeaturePython] Array  # Draft array (typed FeaturePython)
  AlwaysSyncPlacement = false
  Angle = 180
  ArrayType = 1
  Axis = (0,0,1)
  Base = -> Fusion
  Center = (-10,0,0)
  Count = 5
  ExpandArray = false
  Fuse = false
  IntervalAxis = (0,0,0)
  IntervalX = (50,0,0)
  IntervalY = (0,50,0)
  IntervalZ = (0,0,50)
  NumberCircles = 3
  NumberPolar = 5
  NumberX = 2
  NumberY = 2
  NumberZ = 1
  PlacementList = 5 placements: [(0,0,0),(-2.92893,7.07107,0),(-10,10,0),(-17.0711,7.07107,0),(-20,1.22465e-15,0)]
  RadialDistance = 50
  ScaleList = (5) [(1,1,1),(1,1,1),(1,1,1),(1,1,1),(1,1,1)]
  Symmetry = 1
  TangentialDistance = 25
FEATURE [Part::FeaturePython] Array001  # Draft array (typed FeaturePython)
  AlwaysSyncPlacement = false
  Angle = 360
  ArrayType = 0
  Axis = (0,0,1)
  Base = -> Array
  Center = (0,0,0)
  Count = 4
  ExpandArray = false
  Fuse = true
  IntervalAxis = (0,0,0)
  IntervalX = (120,0,0)
  IntervalY = (0,120,0)
  IntervalZ = (0,0,100)
  NumberCircles = 3
  NumberPolar = 5
  NumberX = 2
  NumberY = 2
  NumberZ = 1
  PlacementList = 4 placements: [(0,0,0),(0,120,0),(120,0,0),(120,120,0)]
  RadialDistance = 50
  ScaleList = (4) [(1,1,1),(1,1,1),(1,1,1),(1,1,1)]
  Symmetry = 1
  TangentialDistance = 25
FEATURE [App::Part] Part001
  Group = -> [Array,GDMLBox_Box,GDMLTorus,Fusion,Array001]
  Origin = -> Origin004
FEATURE [App::Part] worldVOL
  Group = -> [GDMLBox_WorldBox,Part001]
  Origin = -> Origin
